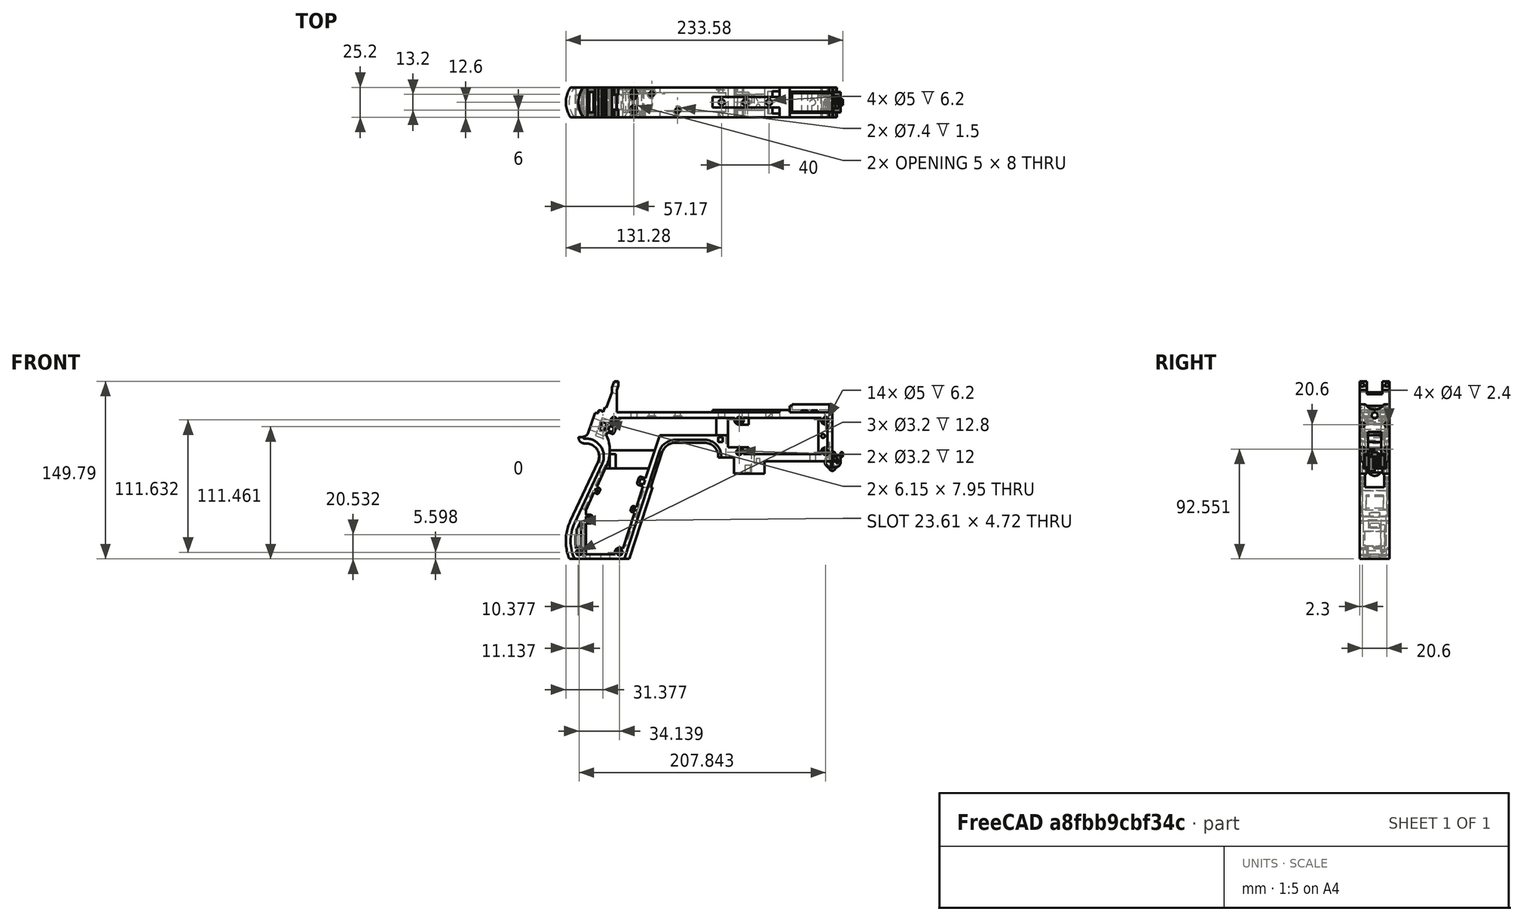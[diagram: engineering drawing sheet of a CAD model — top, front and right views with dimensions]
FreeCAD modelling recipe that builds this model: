
FCSTD DOCUMENT  (FreeCAD 1.0R39319 (Git))
Label: PICON-OF_ver_40
License: All rights reserved
LicenseURL: https://en.wikipedia.org/wiki/All_rights_reserved
objects: Sketcher::SketchObject×109, Part::Extrusion×52, Part::Cut×41, PartDesign::Pad×29, PartDesign::Pocket×18, PartDesign::Chamfer×15, PartDesign::Body×10, PartDesign::Fillet×6, PartDesign::SubtractivePipe×4, Part::Part2DObjectPython×4, PartDesign::SubtractiveLoft×4, PartDesign::Plane×2, PartDesign::SubShapeBinder×2, Part::Sweep×1, PartDesign::ShapeBinder×1, Part::MultiFuse×1, Mesh::Feature×1
note: 560 computed .brp shape members not serialized (recipe doc carries the construction recipe); baked Part::Feature solids carry a one-line shape summary decoded from their .brp

FEATURE [Sketcher::SketchObject] Sketch  label="corpo principale"
  ArcFitTolerance = 1e-06
  AttacherType = Attacher::AttachEngine3D
  AttachmentSupport = -> [XZ_Plane]
  FullyConstrained = true
  MakeInternals = false
  MapMode = 5
  Placement = pos=(0,0,0) rot=(1,0,0;1.5708rad)
  sketch-geometry (65):
    g0: LineSegment StartX=0 StartY=0 StartZ=0 EndX=-57.2 EndY=0 EndZ=0
    g1: LineSegment StartX=-57.2 StartY=0 StartZ=0 EndX=-57.2 EndY=-10.4 EndZ=0
    g2: LineSegment StartX=-57.2 StartY=-10.4 StartZ=0 EndX=-82.8 EndY=-10.4 EndZ=0
    g3: LineSegment StartX=-82.8 StartY=-10.4 StartZ=0 EndX=-82.8 EndY=3.2 EndZ=0
    g4: LineSegment StartX=-82.8 StartY=3.2 StartZ=0 EndX=-93.6 EndY=3.2 EndZ=0
    g5: LineSegment StartX=-93.6 StartY=3.2 StartZ=0 EndX=-93.6 EndY=4 EndZ=0
    g6: LineSegment StartX=-107.6 StartY=18 StartZ=0 EndX=-132.428 EndY=18 EndZ=0
    g7: LineSegment StartX=-145.743 StartY=8.32624 StartZ=0 EndX=-175.232 EndY=-82.4316 EndZ=0
    g8: LineSegment StartX=-175.232 StartY=-82.4316 StartZ=0 EndX=-217.232 EndY=-82.4316 EndZ=0
    g9: LineSegment StartX=-217.232 StartY=-52.1862 StartZ=0 EndX=-193.988 EndY=-2.33927 EndZ=0
    g10: LineSegment StartX=-206.196 StartY=23.0857 StartZ=0 EndX=-199.861 EndY=40.4914 EndZ=0
    g11: LineSegment StartX=-199.861 StartY=40.4914 StartZ=0 EndX=-197.061 EndY=40.4914 EndZ=0
    g12: LineSegment StartX=-197.061 StartY=40.4914 StartZ=0 EndX=-197.061 EndY=42.8914 EndZ=0
    g13: LineSegment StartX=-197.061 StartY=42.8914 StartZ=0 EndX=-194.261 EndY=42.8914 EndZ=0
    g14: LineSegment StartX=-194.261 StartY=42.8914 StartZ=0 EndX=-194.535 EndY=42.1397 EndZ=0
    g15: LineSegment StartX=-194.535 StartY=42.1397 StartZ=0 EndX=-193.031 EndY=41.5924 EndZ=0
    g16: LineSegment StartX=-193.031 StartY=41.5924 StartZ=0 EndX=-191.663 EndY=45.3512 EndZ=0
    g17: LineSegment StartX=-191.663 StartY=45.3512 StartZ=0 EndX=-190.536 EndY=44.9408 EndZ=0
    g18: LineSegment StartX=-190.536 StartY=44.9408 StartZ=0 EndX=-185.747 EndY=58.0965 EndZ=0
    g19: LineSegment StartX=-185.747 StartY=58.0965 StartZ=0 EndX=-185.747 EndY=62.0965 EndZ=0
    g20: LineSegment StartX=-185.747 StartY=62.0965 StartZ=0 EndX=-183.832 EndY=67.3588 EndZ=0
    g21: LineSegment StartX=-183.832 StartY=67.3588 StartZ=0 EndX=-180.232 EndY=67.3588 EndZ=0
    g22: LineSegment StartX=-180.232 StartY=67.3588 StartZ=0 EndX=-180.232 EndY=63.7588 EndZ=0
    g23: LineSegment StartX=-180.232 StartY=63.7588 StartZ=0 EndX=-181.6 EndY=60 EndZ=0
    g24: LineSegment StartX=-181.6 StartY=60 StartZ=0 EndX=-181.6 EndY=41.2 EndZ=0
    g25: LineSegment StartX=-181.6 StartY=41.2 StartZ=0 EndX=-100.8 EndY=41.2 EndZ=0
    g26: LineSegment StartX=-36 StartY=43.2 StartZ=0 EndX=-36 EndY=41.2 EndZ=0
    g27: LineSegment StartX=0 StartY=48 StartZ=0 EndX=0 EndY=0 EndZ=0
    g28: LineSegment StartX=-209.901 StartY=19.85 StartZ=0 EndX=-209.901 EndY=20.1 EndZ=0
    g29: LineSegment StartX=-208.001 StartY=22 StartZ=0 EndX=-207.747 EndY=22 EndZ=0
    g30: LineSegment StartX=-207.583 StartY=19 StartZ=0 EndX=-209.051 EndY=19 EndZ=0
    g31: ArcOfCircle CenterX=-208.001 CenterY=20.1 CenterZ=0 NormalX=0 NormalY=0 NormalZ=1 AngleXU=0 Radius=1.9 StartAngle=1.5708 EndAngle=3.14159
    g32: GeomPoint [constr] X=-209.901 Y=22 Z=0
    g33: ArcOfCircle CenterX=-209.051 CenterY=19.85 CenterZ=0 NormalX=0 NormalY=0 NormalZ=1 AngleXU=0 Radius=0.85 StartAngle=3.14159 EndAngle=4.71239
    g34: GeomPoint [constr] X=-209.901 Y=19 Z=0
    g35: ArcOfCircle CenterX=-207.747 CenterY=23.65 CenterZ=0 NormalX=0 NormalY=0 NormalZ=1 AngleXU=0 Radius=1.65 StartAngle=4.71239 EndAngle=5.93412
    g36: GeomPoint [constr] X=-206.591 Y=22 Z=0
    g37: LineSegment StartX=-4 StartY=6 StartZ=0 EndX=-4 EndY=36.4 EndZ=0
    g38: LineSegment StartX=-4 StartY=36.4 StartZ=0 EndX=-185.2 EndY=36.4 EndZ=0
    g39: LineSegment StartX=-185.2 StartY=36.4 StartZ=0 EndX=-190.441 EndY=22 EndZ=0
    g40: LineSegment StartX=-214.575 StartY=-78.4316 StartZ=0 EndX=-178.142 EndY=-78.4316 EndZ=0
    g41: LineSegment StartX=-178.142 StartY=-78.4316 StartZ=0 EndX=-145.51 EndY=22 EndZ=0
    g42: LineSegment StartX=-145.51 StartY=22 StartZ=0 EndX=-87.91 EndY=22 EndZ=0
    g43: LineSegment StartX=-87.91 StartY=22 StartZ=0 EndX=-87.91 EndY=11.6 EndZ=0
    g44: LineSegment StartX=-87.91 StartY=11.6 StartZ=0 EndX=-80.11 EndY=11.6 EndZ=0
    g45: LineSegment StartX=-80.11 StartY=11.6 StartZ=0 EndX=-80.11 EndY=6 EndZ=0
    g46: LineSegment StartX=-80.11 StartY=6 StartZ=0 EndX=-4 EndY=6 EndZ=0
    g47: LineSegment StartX=-190.363 StartY=-4.02975 StartZ=0 EndX=-213.607 EndY=-53.8767 EndZ=0
    g48: ArcOfCircle CenterX=-132.428 CenterY=4 CenterZ=0 NormalX=0 NormalY=0 NormalZ=1 AngleXU=0 Radius=14 StartAngle=1.5708 EndAngle=2.82743
    g49: GeomPoint [constr] X=-142.6 Y=18 Z=0
    g50: ArcOfCircle CenterX=-107.6 CenterY=4 CenterZ=0 NormalX=0 NormalY=0 NormalZ=1 AngleXU=0 Radius=14 StartAngle=0 EndAngle=1.5708
    g51: GeomPoint [constr] X=-93.6 Y=18 Z=0
    g52: ArcOfCircle CenterX=-184.801 CenterY=-67.3089 CenterZ=0 NormalX=0 NormalY=0 NormalZ=1 AngleXU=0 Radius=35.7833 StartAngle=2.70526 EndAngle=3.57792
    g53: ArcOfCircle CenterX=-207.583 CenterY=4 CenterZ=0 NormalX=0 NormalY=0 NormalZ=1 AngleXU=0 Radius=15 StartAngle=5.84685 EndAngle=7.85398
    g54: LineSegment [constr] StartX=-213.607 StartY=-53.8767 StartZ=0 EndX=-217.232 EndY=-52.1862 EndZ=0
    g55: ArcOfCircle CenterX=-184.801 CenterY=-67.3089 CenterZ=0 NormalX=0 NormalY=0 NormalZ=1 AngleXU=0 Radius=31.7833 StartAngle=2.70526 EndAngle=3.49911
    g56: ArcOfCircle CenterX=-218.095 CenterY=8.90192 CenterZ=0 NormalX=0 NormalY=0 NormalZ=1 AngleXU=0 Radius=30.5989 StartAngle=5.84685 EndAngle=6.72553
    g57: LineSegment StartX=-44.6 StartY=43.2 StartZ=0 EndX=-36 EndY=43.2 EndZ=0
    g58: LineSegment StartX=-100.8 StartY=41.2 StartZ=0 EndX=-44.6 EndY=41.2 EndZ=0
    g59: LineSegment StartX=-44.6 StartY=41.2 StartZ=0 EndX=-44.6 EndY=43.2 EndZ=0
    g60: LineSegment StartX=-2.4 StartY=48 StartZ=0 EndX=0 EndY=48 EndZ=0
    g61: LineSegment StartX=-36 StartY=41.2 StartZ=0 EndX=-2.4 EndY=41.2 EndZ=0
    g62: LineSegment StartX=-2.4 StartY=41.2 StartZ=0 EndX=-2.4 EndY=48 EndZ=0
    g63: LineSegment [constr] StartX=-181.6 StartY=36.4 StartZ=0 EndX=-152.209 EndY=36.4 EndZ=0
    g64: LineSegment [constr] StartX=-181.6 StartY=36.4 StartZ=0 EndX=-130.41 EndY=36.4 EndZ=0
  constraints (183):
    c: Coincident(g-1,g0)
    c: PointOnObject(g0,g-1)
    c: Coincident(g0,g1)
    c: Vertical(g1)
    c: Coincident(g1,g2)
    c: Horizontal(g2)
    c: Coincident(g2,g3)
    c: Vertical(g3)
    c: Coincident(g3,g4)
    c: Coincident(g4,g5)
    c: Vertical(g5)
    c: Horizontal(g6)
    c: Coincident(g7,g8)
    c: Horizontal(g8)
    c: Coincident(g10,g11)
    c: Horizontal(g11)
    c: Coincident(g11,g12)
    c: Vertical(g12)
    c: Coincident(g12,g13)
    c: Horizontal(g13)
    c: Coincident(g13,g14)
    c: Coincident(g14,g15)
    c: Coincident(g15,g16)
    c: Coincident(g16,g17)
    c: Coincident(g17,g18)
    c: Coincident(g18,g19)
    c: Vertical(g19)
    c: Coincident(g19,g20)
    c: Coincident(g20,g21)
    c: Horizontal(g21)
    c: Coincident(g21,g22)
    c: Vertical(g22)
    c: Coincident(g22,g23)
    c: Coincident(g23,g24)
    c: Vertical(g24)
    c: Coincident(g24,g25)
    c: Horizontal(g25)
    c: Coincident(g57,g26)
    c: Vertical(g26)
    c: Coincident(g26,g61)
    c: PointOnObject(g60,g-2)
    c: Coincident(g60,g27)
    c: Coincident(g27,g0)
    c: DistanceY(g27,g27) = 48
    c: DistanceY(g1,g1) = 10.4
    c: DistanceX(g0,g0) = 57.2
    c: DistanceX(g2,g2) = 25.6
    c: Horizontal(g4)
    c: DistanceY(g3,g3) = 13.6
    c: DistanceX(g4,g4) = 10.8
    c: DistanceY(g5,g51) = 14.8
    c: DistanceX(g49,g51) = 49
    c: Distance(g7,g49) = 105.6
    c: DistanceX(g61,g60) = 36
    c: DistanceX(g25,g25) = 80.8
    c: DistanceY(g24,g24) = 18.8
    c: DistanceY(g22,g22) = 3.6
    c: Distance(g23) = 4
    c: Angle(g-1,g23) = 1.22173
    c: DistanceX(g21,g21) = 3.6
    c: Distance(g20) = 5.6
    c: Angle(g-1,g20) = 1.22173
    c: DistanceY(g19,g19) = 4
    c: Distance(g18) = 14
    c: Angle(g-1,g18) = 1.22173
    c: Distance(g17) = 1.2
    c: Distance(g16) = 4
    c: Angle(g16) = 1.22173
    c: Perpendicular(g18,g17)
    c: Distance(g15) = 1.6
    c: Perpendicular(g16,g15)
    c: Distance(g14) = 0.8
    c: DistanceX(g13,g13) = 2.8
    c: Perpendicular(g15,g14)
    c: DistanceY(g12,g12) = 2.4
    c: DistanceX(g11,g11) = 2.8
    c: Distance(g9) = 55
    c: Angle(g9,g-1) = 2.00713
    c: Horizontal(g29)
    c: Vertical(g28)
    c: Horizontal(g30)
    c: PointOnObject(g32,g29)
    c: PointOnObject(g32,g28)
    c: Tangent(g29,g31) = 1.5708
    c: Tangent(g28,g31) = 1.5708
    c: PointOnObject(g34,g28)
    c: PointOnObject(g34,g30)
    c: Tangent(g28,g33) = 1.5708
    c: Tangent(g30,g33) = 1.5708
    c: PointOnObject(g36,g29)
    c: PointOnObject(g36,g10)
    c: Tangent(g29,g35) = -1.5708
    c: Tangent(g10,g35) = -1.5708
    c: Angle(g-1,g10) = 1.22173
    c: Radius(g35) = 1.65
    c: Vertical(g37)
    c: Coincident(g37,g38)
    c: Horizontal(g38)
    c: Coincident(g38,g39)
    c: Horizontal(g40)
    c: Coincident(g40,g41)
    c: Coincident(g41,g42)
    c: Horizontal(g42)
    c: Coincident(g42,g43)
    c: Vertical(g43)
    c: Coincident(g43,g44)
    c: Horizontal(g44)
    c: Coincident(g44,g45)
    c: Vertical(g45)
    c: Coincident(g45,g46)
    c: Coincident(g46,g37)
    c: Horizontal(g46)
    c: DistanceY(g0,g37) = 6
    c: DistanceX(g37,g0) = 4
    c: DistanceY(g37,g25) = 4.8
    c: DistanceX(g38,g38) = 181.2
    c: DistanceX(g42,g42) = 57.6
    c: DistanceY(g49,g41) = 4
    c: DistanceX(g41,g49) = 2.91
    c: DistanceY(g43,g43) = 10.4
    c: DistanceX(g44,g44) = 7.8
    c: DistanceY(g7,g40) = 4
    c: Distance(g47) = 55
    c: Angle(g-1,g39) = 1.22173
    c: PointOnObject(g49,g7)
    c: PointOnObject(g49,g6)
    c: Tangent(g7,g48) = -1.5708
    c: Tangent(g6,g48) = -1.5708
    c: PointOnObject(g51,g5)
    c: PointOnObject(g51,g6)
    c: Tangent(g5,g50) = -1.5708
    c: Tangent(g6,g50) = -1.5708
    c: Radius(g50) = 14
    c: Radius(g48) = 14
    c: DistanceX(g8,g8) = 42
    c: Angle(g7,g-1) = 1.88496
    c: Parallel(g41,g7)
    c: Parallel(g47,g9)
    c: Coincident(g52,g8)
    c: Tangent(g52,g9) = 1.5708
    c: DistanceX(g9,g8) = 0
    c: Tangent(g53,g9) = -1.5708
    c: Tangent(g53,g30) = -1.5708
    c: Diameter(g53) = 30
    c: DistanceY(g53,g0) = -4
    c: Coincident(g54,g47)
    c: Distance(g54) = 4
    c: Coincident(g54,g9)
    c: Coincident(g55,g40)
    c: Tangent(g55,g47) = -1.5708
    c: Coincident(g52,g55)
    c: Coincident(g56,g39)
    c: Tangent(g56,g47) = 1.5708
    c: Horizontal(g57)
    c: DistanceX(g57,g57) = 8.6
    c: Coincident(g58,g25)
    c: Horizontal(g58)
    c: Coincident(g59,g58)
    c: Vertical(g59)
    c: DistanceY(g58,g57) = 2
    c: DistanceX(g58,g58) = 56.2
    c: Coincident(g59,g57)
    c: DistanceY(g41,g36) = 0
    c: DistanceY(g36,g39) = 0
    c: DistanceY(g28,g28) = 0.25
    c: DistanceX(g30,g36) = 2.46
    c: DistanceX(g28,g29) = 1.9
    c: Coincident(g62,g60)
    c: Horizontal(g60)
    c: DistanceX(g62,g27) = 2.4
    c: Coincident(g61,g62)
    c: DistanceY(g26,g26) = 2
    c: Vertical(g62)
    c: DistanceY(g61,g60) = 6.8
    c: Horizontal(g61)
    c: Distance(g63) = 29.391
    c: PointOnObject(g63,g38)
    c: PointOnObject(g63,g38)
    c: Distance(g64) = 51.19
    c: PointOnObject(g64,g38)
    c: PointOnObject(g64,g38)
    c: DistanceX(g24,g63) = 0
    c: DistanceX(g24,g64) = 0
FEATURE [Part::Extrusion] Extrude  label="Extrude corpo principale"
  Base = -> Sketch
  Dir = (0,-1,2e-16)
  DirMode = 2
  FaceMakerClass = Part::FaceMakerBullseye
  FaceMakerMode = 3
  LengthFwd = 25.2
  LengthRev = 12.6
  Solid = true
  Symmetric = true
FEATURE [Sketcher::SketchObject] Sketch002  label="scavo grilletto"
  ArcFitTolerance = 1e-06
  AttachmentSupport = -> [XZ_Plane]
  ExternalGeometry = -> [Sketch]
  FullyConstrained = true
  MakeInternals = false
  MapMode = 5
  Placement = pos=(0,0,0) rot=(1,0,0;1.5708rad)
  sketch-geometry (4):
    g0: LineSegment StartX=-89.51 StartY=22 StartZ=0 EndX=-152.71 EndY=22 EndZ=0
    g1: LineSegment StartX=-152.71 StartY=22 StartZ=0 EndX=-167.006 EndY=-22 EndZ=0
    g2: LineSegment StartX=-167.006 StartY=-22 StartZ=0 EndX=-89.51 EndY=-22 EndZ=0
    g3: LineSegment StartX=-89.51 StartY=-22 StartZ=0 EndX=-89.51 EndY=22 EndZ=0
  constraints (12):
    c: Horizontal(g0)
    c: Coincident(g0,g1)
    c: Coincident(g1,g2)
    c: Horizontal(g2)
    c: Coincident(g2,g3)
    c: Coincident(g3,g0)
    c: Vertical(g3)
    c: Angle(g1,g0) = 1.88496
    c: DistanceY(g3,g3) = 44
    c: DistanceX(g0,g0) = 63.2
    c: DistanceX(g0,g-3) = 1.6
    c: DistanceY(g-3,g0) = 0
FEATURE [Sketcher::SketchObject] Sketch004  label="traiettoria arrotondamento impugnatura anteriore"
  ArcFitTolerance = 1e-06
  AttachmentSupport = -> [XZ_Plane]
  ExternalGeometry = -> [Sketch]
  FullyConstrained = true
  MakeInternals = false
  MapMode = 5
  Placement = pos=(0,0,0) rot=(1,0,0;1.5708rad)
  sketch-geometry (13):
    g0: LineSegment StartX=-175.232 StartY=-82.4316 StartZ=0 EndX=-145.743 EndY=8.32624 EndZ=0
    g1: LineSegment StartX=-93.6 StartY=3.2 StartZ=0 EndX=-93.6 EndY=4 EndZ=0
    g2: LineSegment StartX=-132.428 StartY=18 StartZ=0 EndX=-107.6 EndY=18 EndZ=0
    g3: ArcOfCircle CenterX=-132.428 CenterY=4 CenterZ=0 NormalX=0 NormalY=0 NormalZ=1 AngleXU=0 Radius=14 StartAngle=1.5708 EndAngle=2.82743
    g4: ArcOfCircle CenterX=-107.6 CenterY=4 CenterZ=0 NormalX=0 NormalY=0 NormalZ=1 AngleXU=0 Radius=14 StartAngle=0 EndAngle=1.5708
    g5: LineSegment StartX=-175.232 StartY=-82.4316 StartZ=0 EndX=-217.232 EndY=-82.4316 EndZ=0
    g6: LineSegment StartX=-217.232 StartY=-52.1862 StartZ=0 EndX=-193.988 EndY=-2.33927 EndZ=0
    g7: LineSegment StartX=-209.051 StartY=19 StartZ=0 EndX=-207.583 EndY=19 EndZ=0
    g8: LineSegment StartX=-209.901 StartY=20.1 StartZ=0 EndX=-209.901 EndY=19.85 EndZ=0
    g9: ArcOfCircle CenterX=-184.801 CenterY=-67.3089 CenterZ=0 NormalX=0 NormalY=0 NormalZ=1 AngleXU=0 Radius=35.7833 StartAngle=2.70526 EndAngle=3.57792
    g10: ArcOfCircle CenterX=-207.583 CenterY=4 CenterZ=0 NormalX=0 NormalY=0 NormalZ=1 AngleXU=0 Radius=15 StartAngle=5.84685 EndAngle=7.85398
    g11: ArcOfCircle CenterX=-209.051 CenterY=19.85 CenterZ=0 NormalX=0 NormalY=0 NormalZ=1 AngleXU=0 Radius=0.85 StartAngle=3.14159 EndAngle=4.71239
    g12: ArcOfCircle CenterX=-208.001 CenterY=20.1 CenterZ=0 NormalX=0 NormalY=0 NormalZ=1 AngleXU=0 Radius=1.9 StartAngle=1.5708 EndAngle=3.14159
  constraints (26):
    c: Coincident(g0,g-3)
    c: Coincident(g0,g-6)
    c: Coincident(g1,g-8)
    c: Coincident(g1,g-7)
    c: Coincident(g2,g-5)
    c: Coincident(g2,g-4)
    c: Coincident(g3,g2)
    c: Tangent(g3,g0) = 1.5708
    c: Coincident(g4,g1)
    c: Tangent(g4,g2) = 1.5708
    c: Coincident(g5,g0)
    c: Coincident(g5,g-9)
    c: Coincident(g6,g-12)
    c: Coincident(g6,g-11)
    c: Coincident(g7,g-15)
    c: Coincident(g7,g-14)
    c: Coincident(g8,g-16)
    c: Coincident(g8,g-17)
    c: Tangent(g9,g6) = 1.5708
    c: Coincident(g9,g5)
    c: Coincident(g10,g7)
    c: Tangent(g10,g6) = -1.5708
    c: Tangent(g11,g7) = -1.5708
    c: Coincident(g11,g8)
    c: Tangent(g12,g8) = -1.5708
    c: Coincident(g12,g-17)
FEATURE [PartDesign::Plane] DatumPlane  label="Piano per disegno arrotondamento impugnatura"
  AttachmentSupport = -> [Sketch]
  Length = 73.6581
  MapMode = 7
  Placement = pos=(-145.743,1.8e-15,8.32624) rot=(0.154555,0.154555,0.97582;1.59527rad)
  ResizeMode = 0
  Width = 303.511
FEATURE [Sketcher::SketchObject] Sketch005  label="forma arrotondamento impugnatura anteriore"
  ArcFitTolerance = 1e-06
  AttachmentSupport = -> [DatumPlane]
  FullyConstrained = true
  MakeInternals = false
  MapMode = 5
  Placement = pos=(-145.743,1.8e-15,8.32624) rot=(0.154555,0.154555,0.97582;1.59527rad)
  sketch-geometry (5):
    g0: GeomPoint [constr] X=0 Y=-4 Z=0
    g1: GeomPoint [constr] X=-12.6 Y=7.1e-15 Z=0
    g2: GeomPoint [constr] X=12.6 Y=4.97e-14 Z=0
    g3: LineSegment StartX=-12.6 StartY=7.1e-15 StartZ=0 EndX=12.6 EndY=4.97e-14 EndZ=0
    g4: ArcOfCircle CenterX=-3.88e-14 CenterY=17.845 CenterZ=0 NormalX=0 NormalY=0 NormalZ=1 AngleXU=0 Radius=21.845 StartAngle=4.09759 EndAngle=5.32718
  constraints (11):
    c: DistanceY(g0,g-1) = 4
    c: DistanceX(g-1,g0) = 0
    c: DistanceX(g1,g-1) = 12.6
    c: DistanceX(g-1,g2) = 12.6
    c: DistanceY(g-1,g2) = 0
    c: DistanceY(g-1,g1) = 0
    c: Coincident(g3,g1)
    c: Coincident(g3,g2)
    c: Coincident(g4,g1)
    c: Coincident(g4,g2)
    c: PointOnObject(g0,g4)
FEATURE [Part::Sweep] Sweep  label="Sweep impugnatura"
  Frenet = true
  Sections = -> [Sketch005]
  Solid = true
  Spine = -> Sketch [Edge32,Edge33,Edge34,Edge35,Edge36,Edge37,Edge38,Edge39,Edge40,Edge41,Edge42,Edge43,Edge44]
  Transition = 1
FEATURE [Sketcher::SketchObject] Sketch008  label="buchi e pulizie varie"
  ArcFitTolerance = 1e-06
  AttachmentSupport = -> [XZ_Plane]
  ExternalGeometry = -> [Sketch]
  FullyConstrained = true
  MakeInternals = false
  MapMode = 5
  Placement = pos=(0,0,0) rot=(1,0,0;1.5708rad)
  sketch-geometry (26):
    g0: LineSegment StartX=-96.278 StartY=20.155 StartZ=0 EndX=-92.278 EndY=20.155 EndZ=0
    g1: LineSegment StartX=-92.278 StartY=20.155 StartZ=0 EndX=-92.278 EndY=16.155 EndZ=0
    g2: LineSegment StartX=-92.278 StartY=16.155 StartZ=0 EndX=-96.278 EndY=16.155 EndZ=0
    g3: LineSegment StartX=-96.278 StartY=16.155 StartZ=0 EndX=-96.278 EndY=20.155 EndZ=0
    g4: LineSegment StartX=-222.232 StartY=-82.4316 StartZ=0 EndX=-170.232 EndY=-82.4316 EndZ=0
    g5: LineSegment StartX=-170.232 StartY=-82.4316 StartZ=0 EndX=-170.232 EndY=-86.4316 EndZ=0
    g6: LineSegment StartX=-170.232 StartY=-86.4316 StartZ=0 EndX=-222.232 EndY=-86.4316 EndZ=0
    g7: LineSegment StartX=-222.232 StartY=-86.4316 StartZ=0 EndX=-222.232 EndY=-82.4316 EndZ=0
    g8: LineSegment StartX=-213.901 StartY=20.1 StartZ=0 EndX=-213.901 EndY=26 EndZ=0
    g9: LineSegment StartX=-213.901 StartY=26 StartZ=0 EndX=-206.196 EndY=26 EndZ=0
    g10: LineSegment StartX=-17.4 StartY=42.8 StartZ=0 EndX=-12.4 EndY=42.8 EndZ=0
    g11: LineSegment StartX=-12.4 StartY=42.8 StartZ=0 EndX=-12.4 EndY=41.2 EndZ=0
    g12: LineSegment StartX=-12.4 StartY=41.2 StartZ=0 EndX=-17.4 EndY=41.2 EndZ=0
    g13: LineSegment StartX=-17.4 StartY=41.2 StartZ=0 EndX=-17.4 EndY=42.8 EndZ=0
    g14: LineSegment StartX=-25.9 StartY=42.8 StartZ=0 EndX=-20.9 EndY=42.8 EndZ=0
    g15: LineSegment StartX=-20.9 StartY=42.8 StartZ=0 EndX=-20.9 EndY=41.2 EndZ=0
    g16: LineSegment StartX=-20.9 StartY=41.2 StartZ=0 EndX=-25.9 EndY=41.2 EndZ=0
    g17: LineSegment StartX=-25.9 StartY=41.2 StartZ=0 EndX=-25.9 EndY=42.8 EndZ=0
    g18: GeomPoint [constr] X=-206.196 Y=23.0857 Z=0
    g19: GeomPoint [constr] X=-213.901 Y=20.1 Z=0
    g20: BSplineCurve PolesCount=4 KnotsCount=2 Degree=3 IsPeriodic=0
    g21-g24: Circle [constr] x4 (B-spline internal-alignment scaffolding for g20; pole/knot coordinates omitted)
    g25: LineSegment StartX=-206.196 StartY=26 StartZ=0 EndX=-206.196 EndY=23.0857 EndZ=0
  constraints (73):
    c: Horizontal(g0)
    c: Coincident(g1,g0)
    c: Vertical(g1)
    c: Coincident(g2,g1)
    c: Horizontal(g2)
    c: Coincident(g3,g2)
    c: Coincident(g3,g0)
    c: Vertical(g3)
    c: DistanceX(g0,g-4) = 4.368
    c: DistanceY(g0,g-4) = 1.845
    c: DistanceY(g1,g1) = 4
    c: DistanceX(g2,g2) = 4
    c: Horizontal(g4)
    c: Coincident(g5,g4)
    c: Vertical(g5)
    c: Coincident(g6,g5)
    c: Horizontal(g6)
    c: Coincident(g7,g6)
    c: Coincident(g7,g4)
    c: Vertical(g7)
    c: DistanceY(g7,g7) = 4
    c: DistanceX(g4,g-5) = 5
    c: DistanceX(g-5,g4) = 5
    c: DistanceY(g4,g-5) = 0
    c: Coincident(g9,g8)
    c: Parallel(g9,g-6)
    c: DistanceX(g8,g-8) = 4
    c: Horizontal(g10)
    c: Coincident(g11,g10)
    c: Vertical(g11)
    c: Coincident(g12,g11)
    c: Horizontal(g12)
    c: Coincident(g13,g12)
    c: Coincident(g13,g10)
    c: Vertical(g13)
    c: Horizontal(g14)
    c: Coincident(g15,g14)
    c: Vertical(g15)
    c: Coincident(g16,g15)
    c: Horizontal(g16)
    c: Coincident(g17,g16)
    c: Coincident(g17,g14)
    c: Vertical(g17)
    c: DistanceY(g11,g10) = 1.6
    c: DistanceX(g10,g10) = 5
    c: DistanceY(g15,g14) = 1.6
    c: DistanceX(g14,g14) = 5
    c: DistanceX(g15,g12) = 3.5
    c: DistanceX(g11,g-9) = 10
    c: DistanceY(g-9,g11) = 0
    c: DistanceY(g-9,g15) = 0
    c: Perpendicular(g8,g9)
    c: DistanceY(g-7,g9) = 4
    c: DistanceY(g8,g-8) = 0
    c: InternalAlignment(g18,g20)
    c: InternalAlignment(g19,g20)
    c: InternalAlignment(g21,g20)
    c: Weight(g21) = 1
    c: InternalAlignment(g22,g20)
    c: Equal(g22,g21)
    c: InternalAlignment(g23,g20)
    c: Equal(g23,g21)
    c: InternalAlignment(g24,g20)
    c: Equal(g24,g21)
    c: Coincident(g18,g-12)
    c: Coincident(g19,g8)
    c: Coincident(g25,g9)
    c: Coincident(g25,g20)
    c: Vertical(g25)
    c: DistanceY(g20,g23) = 0
    c: DistanceY(g22,g18) = 2.26
    c: DistanceX(g22,g18) = 0.93
    c: DistanceX(g20,g23) = 2.9
FEATURE [Part::Extrusion] Extrude004  label="Extrude Buchi e pulizie varie"
  Base = -> Sketch008
  Dir = (0,-1,2e-16)
  DirMode = 2
  FaceMakerClass = Part::FaceMakerBullseye
  FaceMakerMode = 3
  LengthFwd = 25.2
  LengthRev = 0
  Solid = true
  Symmetric = true
FEATURE [Sketcher::SketchObject] Sketch009  label="rinforzi"
  ArcFitTolerance = 1e-06
  AttachmentSupport = -> [XZ_Plane]
  ExternalGeometry = -> [Sketch]
  FullyConstrained = true
  MakeInternals = false
  MapMode = 5
  Placement = pos=(0,0,0) rot=(1,0,0;1.5708rad)
  sketch-geometry (9):
    g0: LineSegment StartX=-87.91 StartY=22 StartZ=0 EndX=-87.91 EndY=36.4 EndZ=0
    g1: LineSegment StartX=-87.91 StartY=36.4 StartZ=0 EndX=-97.91 EndY=36.4 EndZ=0
    g2: LineSegment StartX=-97.91 StartY=36.4 StartZ=0 EndX=-97.91 EndY=22 EndZ=0
    g3: LineSegment StartX=-97.91 StartY=22 StartZ=0 EndX=-87.91 EndY=22 EndZ=0
    g4: LineSegment StartX=-149.713 StartY=9.06563 StartZ=0 EndX=-154.586 EndY=-5.93437 EndZ=0
    g5: LineSegment StartX=-154.586 StartY=-5.93437 StartZ=0 EndX=-191.863 EndY=-5.93437 EndZ=0
    g6: LineSegment StartX=-191.863 StartY=-5.93437 StartZ=0 EndX=-191.863 EndY=9.06563 EndZ=0
    g7: LineSegment StartX=-191.863 StartY=9.06563 StartZ=0 EndX=-149.713 EndY=9.06563 EndZ=0
    g8: LineSegment [constr] StartX=-145.51 StartY=22 StartZ=0 EndX=-149.713 EndY=9.06563 EndZ=0
  constraints (25):
    c: Vertical(g0)
    c: Coincident(g1,g0)
    c: Horizontal(g1)
    c: Coincident(g2,g1)
    c: Vertical(g2)
    c: Coincident(g3,g2)
    c: Coincident(g3,g0)
    c: Horizontal(g3)
    c: Coincident(g0,g-4)
    c: DistanceX(g3,g3) = 10
    c: DistanceY(g0,g-3) = 0
    c: Coincident(g5,g4)
    c: Horizontal(g5)
    c: Coincident(g6,g5)
    c: Vertical(g6)
    c: Coincident(g7,g6)
    c: Coincident(g7,g4)
    c: Horizontal(g7)
    c: Distance(g8) = 13.6
    c: Parallel(g-6,g8)
    c: Coincident(g-6,g8)
    c: Parallel(g4,g-6)
    c: DistanceY(g4,g4) = 15
    c: Coincident(g4,g8)
    c: DistanceX(g-5,g5) = -1.5
FEATURE [Part::Extrusion] Extrude001  label="Extrude scavo grilletto"
  Base = -> Sketch002
  Dir = (0,-1,2e-16)
  DirMode = 2
  FaceMakerClass = Part::FaceMakerBullseye
  FaceMakerMode = 3
  LengthFwd = 16
  LengthRev = 0
  Solid = true
  Symmetric = true
FEATURE [Part::Extrusion] Extrude005  label="Extrude Rinforzi"
  Base = -> Sketch009
  Dir = (0,-1,2e-16)
  DirMode = 2
  FaceMakerClass = Part::FaceMakerBullseye
  FaceMakerMode = 3
  LengthFwd = 2
  LengthRev = 0
  Placement = pos=(0,12.6,0) rot=(0,0,1;0rad)
  Solid = true
  Symmetric = false
FEATURE [PartDesign::ShapeBinder] CopyCut
  TraceSupport = false
FEATURE [PartDesign::Plane] DatumPlane001
  AttachmentSupport = -> [CopyCut]
  Length = 283.944
  MapMode = 5
  Placement = pos=(0,12.6,0) rot=(0,0.707107,0.707107;3.14159rad)
  ResizeMode = 0
  Width = 188.15
FEATURE [Sketcher::SketchObject] Sketch010  label="buco neopixel"
  ArcFitTolerance = 1e-06
  AttachmentSupport = -> [XZ_Plane]
  ExternalGeometry = -> [Sketch]
  FullyConstrained = true
  MakeInternals = false
  MapMode = 5
  Placement = pos=(0,0,0) rot=(1,0,0;1.5708rad)
  sketch-geometry (5):
    g0: LineSegment [constr] StartX=-199.861 StartY=40.4914 StartZ=0 EndX=-201.368 EndY=36.3521 EndZ=0
    g1: LineSegment StartX=-201.368 StartY=36.3521 StartZ=0 EndX=-204.932 EndY=26.5605 EndZ=0
    g2: LineSegment StartX=-201.368 StartY=36.3521 StartZ=0 EndX=-180.2 EndY=28.6477 EndZ=0
    g3: LineSegment StartX=-180.2 StartY=28.6477 StartZ=0 EndX=-183.764 EndY=18.8561 EndZ=0
    g4: LineSegment StartX=-183.764 StartY=18.8561 StartZ=0 EndX=-204.932 EndY=26.5605 EndZ=0
  constraints (14):
    c: Parallel(g0,g-3)
    c: Distance(g0) = 4.405
    c: Coincident(g0,g-3)
    c: Coincident(g2,g1)
    c: Coincident(g3,g2)
    c: Coincident(g4,g3)
    c: Coincident(g4,g1)
    c: Parallel(g1,g-3)
    c: Distance(g1) = 10.42
    c: Coincident(g1,g0)
    c: Parallel(g2,g4)
    c: Perpendicular(g1,g2)
    c: DistanceX(g-4,g2) = 5
    c: Parallel(g3,g1)
FEATURE [Part::Extrusion] Extrude006  label="Extrude buco neopixel"
  Base = -> Sketch010
  Dir = (0,-1,2e-16)
  DirMode = 2
  FaceMakerClass = Part::FaceMakerBullseye
  FaceMakerMode = 3
  LengthFwd = 17.2
  LengthRev = 0
  Solid = true
  Symmetric = true
FEATURE [Sketcher::SketchObject] Sketch011  label="fermo grilletto"
  ArcFitTolerance = 1e-06
  AttachmentSupport = -> [XZ_Plane]
  ExternalGeometry = -> [Sketch]
  FullyConstrained = true
  MakeInternals = false
  MapMode = 5
  Placement = pos=(0,0,0) rot=(1,0,0;1.5708rad)
  sketch-geometry (18):
    g0: LineSegment [constr] StartX=-145.51 StartY=22 StartZ=0 EndX=-157.347 EndY=-14.4293 EndZ=0
    g1: LineSegment [constr] StartX=-157.347 StartY=-14.4293 StartZ=0 EndX=-157.841 EndY=-15.951 EndZ=0
    g2: LineSegment StartX=-161.151 StartY=-13.1932 StartZ=0 EndX=-155.825 EndY=-14.9237 EndZ=0
    g3: LineSegment StartX=-163.167 StartY=-14.2205 StartZ=0 EndX=-164.403 EndY=-18.0247 EndZ=0
    g4: LineSegment StartX=-163.376 StartY=-20.0408 StartZ=0 EndX=-158.05 EndY=-21.7713 EndZ=0
    g5: LineSegment StartX=-158.05 StartY=-21.7713 StartZ=0 EndX=-155.825 EndY=-14.9237 EndZ=0
    g6: LineSegment StartX=-161.645 StartY=-14.7149 StartZ=0 EndX=-157.841 EndY=-15.951 EndZ=0
    g7: LineSegment StartX=-157.841 StartY=-15.951 StartZ=0 EndX=-159.077 EndY=-19.7552 EndZ=0
    g8: LineSegment StartX=-159.077 StartY=-19.7552 StartZ=0 EndX=-162.881 EndY=-18.5191 EndZ=0
    g9: LineSegment StartX=-162.881 StartY=-18.5191 StartZ=0 EndX=-161.645 EndY=-14.7149 EndZ=0
    g10: LineSegment [constr] StartX=-161.645 StartY=-14.7149 StartZ=0 EndX=-161.151 EndY=-13.1932 EndZ=0
    g11: LineSegment [constr] StartX=-159.077 StartY=-19.7552 StartZ=0 EndX=-157.555 EndY=-20.2496 EndZ=0
    g12: LineSegment [constr] StartX=-159.077 StartY=-19.7552 StartZ=0 EndX=-159.572 EndY=-21.2769 EndZ=0
    g13: LineSegment [constr] StartX=-161.645 StartY=-14.7149 StartZ=0 EndX=-163.167 EndY=-14.2205 EndZ=0
    g14: ArcOfCircle CenterX=-161.645 CenterY=-14.7149 CenterZ=0 NormalX=0 NormalY=0 NormalZ=1 AngleXU=0 Radius=1.6 StartAngle=1.25664 EndAngle=2.82743
    g15: GeomPoint [constr] X=-162.673 Y=-12.6988 Z=0
    g16: ArcOfCircle CenterX=-162.881 CenterY=-18.5191 CenterZ=0 NormalX=0 NormalY=0 NormalZ=1 AngleXU=0 Radius=1.6 StartAngle=2.82743 EndAngle=4.39823
    g17: GeomPoint [constr] X=-164.897 Y=-19.5464 Z=0
  constraints (48):
    c: Parallel(g0,g-3)
    c: Distance(g0) = 38.304
    c: Coincident(g0,g-3)
    c: Parallel(g1,g-3)
    c: Distance(g1) = 1.6
    c: Coincident(g1,g0)
    c: Coincident(g5,g4)
    c: Coincident(g5,g2)
    c: Coincident(g7,g6)
    c: Coincident(g8,g7)
    c: Coincident(g9,g8)
    c: Coincident(g9,g6)
    c: Parallel(g7,g-3)
    c: Parallel(g9,g7)
    c: Perpendicular(g6,g7)
    c: Parallel(g6,g8)
    c: Distance(g6) = 4
    c: Distance(g9) = 4
    c: Parallel(g5,g7)
    c: Parallel(g9,g3)
    c: Parallel(g2,g6)
    c: Parallel(g4,g8)
    c: Parallel(g13,g6)
    c: Parallel(g10,g9)
    c: Parallel(g11,g8)
    c: Parallel(g12,g7)
    c: Distance(g10) = 1.6
    c: Distance(g13) = 1.6
    c: Distance(g12) = 1.6
    c: Distance(g11) = 1.6
    c: Coincident(g10,g6)
    c: Coincident(g13,g6)
    c: Coincident(g12,g7)
    c: Coincident(g11,g7)
    c: Distance(g10,g15) = 1.6
    c: Distance(g15,g13) = 1.6
    c: Distance(g4,g12) = 1.6
    c: Distance(g4,g11) = 1.6
    c: PointOnObject(g15,g2)
    c: Tangent(g3,g14) = -1.5708
    c: Tangent(g2,g14) = 1.5708
    c: PointOnObject(g17,g4)
    c: PointOnObject(g17,g3)
    c: Tangent(g4,g16) = -1.5708
    c: Tangent(g3,g16) = -1.5708
    c: Equal(g16,g14)
    c: Coincident(g16,g8)
    c: Coincident(g6,g1)
FEATURE [Part::Extrusion] Extrude007  label="Extrude fermo grilletto"
  Base = -> Sketch011
  Dir = (0,-1,2e-16)
  DirMode = 2
  FaceMakerClass = Part::FaceMakerBullseye
  FaceMakerMode = 3
  LengthFwd = 25.2
  LengthRev = 0
  Solid = true
  Symmetric = true
FEATURE [Sketcher::SketchObject] Sketch012  label="buco oled"
  ArcFitTolerance = 1e-06
  AttachmentSupport = -> [XZ_Plane]
  ExternalGeometry = -> [Sketch]
  FullyConstrained = true
  MakeInternals = false
  MapMode = 5
  Placement = pos=(0,0,0) rot=(1,0,0;1.5708rad)
  sketch-geometry (4):
    g0: LineSegment StartX=-185.747 StartY=58.0965 StartZ=0 EndX=-180.232 EndY=56.0891 EndZ=0
    g1: LineSegment StartX=-185.747 StartY=58.0965 StartZ=0 EndX=-185.747 EndY=67.3588 EndZ=0
    g2: LineSegment StartX=-185.747 StartY=67.3588 StartZ=0 EndX=-180.232 EndY=67.3588 EndZ=0
    g3: LineSegment StartX=-180.232 StartY=67.3588 StartZ=0 EndX=-180.232 EndY=56.0891 EndZ=0
  constraints (10):
    c: Coincident(g1,g0)
    c: Coincident(g2,g1)
    c: Coincident(g3,g2)
    c: Coincident(g3,g0)
    c: Parallel(g1,g-5)
    c: Perpendicular(g-3,g0)
    c: Parallel(g2,g-6)
    c: Parallel(g3,g-4)
    c: Coincident(g0,g-5)
    c: Coincident(g2,g-6)
FEATURE [Part::Extrusion] Extrude008  label="Extrude buco oled"
  Base = -> Sketch012
  Dir = (0,-1,2e-16)
  DirMode = 2
  FaceMakerClass = Part::FaceMakerBullseye
  FaceMakerMode = 3
  LengthFwd = 12.8
  LengthRev = 0
  Solid = true
  Symmetric = true
FEATURE [Sketcher::SketchObject] Sketch013  label="buco pompa"
  ArcFitTolerance = 1e-06
  AttachmentSupport = -> [XZ_Plane]
  ExternalGeometry = -> [Sketch]
  FullyConstrained = true
  MakeInternals = false
  MapMode = 5
  Placement = pos=(0,0,0) rot=(1,0,0;1.5708rad)
  sketch-geometry (8):
    g0: LineSegment StartX=-82.8 StartY=-10.4 StartZ=0 EndX=-82.8 EndY=-9.6 EndZ=0
    g1: LineSegment StartX=-82.8 StartY=-9.6 StartZ=0 EndX=-67.9 EndY=-9.6 EndZ=0
    g2: LineSegment StartX=-67.9 StartY=-9.6 StartZ=0 EndX=-67.9 EndY=6 EndZ=0
    g3: LineSegment StartX=-67.9 StartY=6 StartZ=0 EndX=-65.9 EndY=6 EndZ=0
    g4: LineSegment StartX=-65.9 StartY=6 StartZ=0 EndX=-65.9 EndY=-1.7 EndZ=0
    g5: LineSegment StartX=-65.9 StartY=-1.7 StartZ=0 EndX=-57.2 EndY=-1.7 EndZ=0
    g6: LineSegment StartX=-57.2 StartY=-1.7 StartZ=0 EndX=-57.2 EndY=-10.4 EndZ=0
    g7: LineSegment StartX=-57.2 StartY=-10.4 StartZ=0 EndX=-82.8 EndY=-10.4 EndZ=0
  constraints (22):
    c: Vertical(g0)
    c: Coincident(g1,g0)
    c: Horizontal(g1)
    c: Coincident(g2,g1)
    c: Vertical(g2)
    c: Coincident(g3,g2)
    c: Horizontal(g3)
    c: Coincident(g4,g3)
    c: Vertical(g4)
    c: Coincident(g5,g4)
    c: Horizontal(g5)
    c: Coincident(g6,g5)
    c: Vertical(g6)
    c: Coincident(g7,g6)
    c: Coincident(g7,g0)
    c: DistanceY(g0,g0) = 0.8
    c: DistanceY(g6,g6) = 8.7
    c: DistanceX(g1,g1) = 14.9
    c: DistanceX(g3,g3) = 2
    c: Coincident(g0,g-4)
    c: DistanceY(g2,g-6) = 0
    c: Coincident(g6,g-5)
FEATURE [Part::Extrusion] Extrude009  label="Extrude buco pompa"
  Base = -> Sketch013
  Dir = (0,-1,2e-16)
  DirMode = 2
  FaceMakerClass = Part::FaceMakerBullseye
  FaceMakerMode = 3
  LengthFwd = 13.2
  LengthRev = 0
  Solid = true
  Symmetric = true
FEATURE [Sketcher::SketchObject] Sketch014  label="buco frontale"
  ArcFitTolerance = 1e-06
  AttachmentSupport = -> [XZ_Plane]
  ExternalGeometry = -> [Sketch]
  FullyConstrained = true
  MakeInternals = false
  MapMode = 5
  Placement = pos=(0,0,0) rot=(1,0,0;1.5708rad)
  sketch-geometry (10):
    g0: LineSegment StartX=0 StartY=0 StartZ=0 EndX=0 EndY=24.671 EndZ=0
    g1: LineSegment StartX=0 StartY=24.671 StartZ=0 EndX=-4 EndY=24.671 EndZ=0
    g2: LineSegment StartX=-4 StartY=24.671 StartZ=0 EndX=-4 EndY=16 EndZ=0
    g3: LineSegment StartX=-4 StartY=16 StartZ=0 EndX=-2.4 EndY=16 EndZ=0
    g4: LineSegment StartX=-2.4 StartY=16 StartZ=0 EndX=-2.4 EndY=10 EndZ=0
    g5: LineSegment StartX=-2.4 StartY=10 StartZ=0 EndX=-12 EndY=10 EndZ=0
    g6: LineSegment StartX=-12 StartY=10 StartZ=0 EndX=-12 EndY=6 EndZ=0
    g7: LineSegment StartX=-12 StartY=6 StartZ=0 EndX=-2.4 EndY=6 EndZ=0
    g8: LineSegment StartX=-2.4 StartY=6 StartZ=0 EndX=-2.4 EndY=0 EndZ=0
    g9: LineSegment StartX=-2.4 StartY=0 StartZ=0 EndX=0 EndY=0 EndZ=0
  constraints (29):
    c: Vertical(g0)
    c: Coincident(g1,g0)
    c: Horizontal(g1)
    c: Coincident(g2,g1)
    c: Vertical(g2)
    c: Coincident(g3,g2)
    c: Horizontal(g3)
    c: Coincident(g4,g3)
    c: Vertical(g4)
    c: Coincident(g5,g4)
    c: Horizontal(g5)
    c: Coincident(g6,g5)
    c: Vertical(g6)
    c: Coincident(g7,g6)
    c: Coincident(g8,g7)
    c: Vertical(g8)
    c: Coincident(g9,g8)
    c: Coincident(g9,g0)
    c: Horizontal(g9)
    c: DistanceY(g0,g0) = 24.671
    c: Horizontal(g7)
    c: DistanceY(g6,g6) = 4
    c: DistanceY(g4,g4) = 6
    c: DistanceX(g9,g9) = 2.4
    c: Coincident(g0,g-1)
    c: DistanceY(g-3,g7) = 0
    c: DistanceX(g8,g4) = 0
    c: DistanceX(g-3,g1) = 0
    c: DistanceX(g6,g-3) = 8
FEATURE [Part::Extrusion] Extrude010  label="Extrude buco frontale"
  Base = -> Sketch014
  Dir = (0,-1,2e-16)
  DirMode = 2
  FaceMakerClass = Part::FaceMakerBullseye
  FaceMakerMode = 3
  LengthFwd = 11.2
  LengthRev = 0
  Solid = true
  Symmetric = true
FEATURE [Sketcher::SketchObject] Sketch015  label="guida rail"
  ArcFitTolerance = 1e-06
  AttachmentSupport = -> [XZ_Plane]
  ExternalGeometry = -> [Sketch]
  FullyConstrained = true
  MakeInternals = false
  MapMode = 5
  Placement = pos=(0,0,0) rot=(1,0,0;1.5708rad)
  sketch-geometry (4):
    g0: LineSegment StartX=-100.8 StartY=43.2 StartZ=0 EndX=-44.6 EndY=43.2 EndZ=0
    g1: LineSegment StartX=-44.6 StartY=43.2 StartZ=0 EndX=-44.6 EndY=41.2 EndZ=0
    g2: LineSegment StartX=-44.6 StartY=41.2 StartZ=0 EndX=-100.8 EndY=41.2 EndZ=0
    g3: LineSegment StartX=-100.8 StartY=41.2 StartZ=0 EndX=-100.8 EndY=43.2 EndZ=0
  constraints (9):
    c: Horizontal(g0)
    c: Coincident(g1,g0)
    c: Coincident(g2,g1)
    c: Coincident(g3,g2)
    c: Coincident(g3,g0)
    c: Vertical(g3)
    c: Coincident(g2,g-3)
    c: Coincident(g1,g-3)
    c: Coincident(g0,g-4)
FEATURE [Part::Extrusion] Extrude011  label="Extrude guida rail"
  Base = -> Sketch015
  Dir = (0,-1,2e-16)
  DirMode = 2
  FaceMakerClass = Part::FaceMakerBullseye
  FaceMakerMode = 3
  LengthFwd = 9
  LengthRev = 0
  Solid = true
  Symmetric = true
FEATURE [Sketcher::SketchObject] Sketch016  label="guide per coperture laterali"
  ArcFitTolerance = 1e-06
  AttachmentSupport = -> [XZ_Plane]
  ExternalGeometry = -> [Sketch]
  FullyConstrained = true
  MakeInternals = false
  MapMode = 5
  Placement = pos=(0,0,0) rot=(1,0,0;1.5708rad)
  sketch-geometry (14):
    g0: Circle CenterX=-5.6 CenterY=7.6 CenterZ=0 NormalX=0 NormalY=0 NormalZ=1 AngleXU=0 Radius=1.6
    g1: Circle CenterX=-5.6 CenterY=7.6 CenterZ=0 NormalX=0 NormalY=0 NormalZ=1 AngleXU=0 Radius=4
    g2: Circle CenterX=-5.6 CenterY=34.8 CenterZ=0 NormalX=0 NormalY=0 NormalZ=1 AngleXU=0 Radius=1.6
    g3: Circle CenterX=-5.6 CenterY=34.8 CenterZ=0 NormalX=0 NormalY=0 NormalZ=1 AngleXU=0 Radius=4
    g4: Circle CenterX=-184.08 CenterY=34.8 CenterZ=0 NormalX=0 NormalY=0 NormalZ=1 AngleXU=0 Radius=1.6
    g5: Circle CenterX=-184.08 CenterY=34.8 CenterZ=0 NormalX=0 NormalY=0 NormalZ=1 AngleXU=0 Radius=4
    g6: Circle CenterX=-179.305 CenterY=-76.8316 CenterZ=0 NormalX=0 NormalY=0 NormalZ=1 AngleXU=0 Radius=1.6
    g7: Circle CenterX=-179.305 CenterY=-76.8316 CenterZ=0 NormalX=0 NormalY=0 NormalZ=1 AngleXU=0 Radius=4
    g8: Circle CenterX=-213.443 CenterY=-76.8316 CenterZ=0 NormalX=0 NormalY=0 NormalZ=1 AngleXU=0 Radius=1.6
    g9: Circle CenterX=-213.443 CenterY=-76.8316 CenterZ=0 NormalX=0 NormalY=0 NormalZ=1 AngleXU=0 Radius=4
    g10: Circle CenterX=-78.51 CenterY=7.6 CenterZ=0 NormalX=0 NormalY=0 NormalZ=1 AngleXU=0 Radius=1.6
    g11: Circle CenterX=-78.51 CenterY=7.6 CenterZ=0 NormalX=0 NormalY=0 NormalZ=1 AngleXU=0 Radius=4
    g12: Circle CenterX=-78.51 CenterY=34.8 CenterZ=0 NormalX=0 NormalY=0 NormalZ=1 AngleXU=0 Radius=1.6
    g13: Circle CenterX=-78.51 CenterY=34.8 CenterZ=0 NormalX=0 NormalY=0 NormalZ=1 AngleXU=0 Radius=4
  constraints (35):
    c: Diameter(g0) = 3.2
    c: Diameter(g1) = 8
    c: Coincident(g0,g1)
    c: Diameter(g2) = 3.2
    c: Diameter(g3) = 8
    c: Coincident(g3,g2)
    c: Tangent(g2,g-7)
    c: Diameter(g4) = 3.2
    c: Diameter(g5) = 8
    c: Coincident(g5,g4)
    c: Tangent(g4,g-7)
    c: Tangent(g4,g-8)
    c: Diameter(g6) = 3.2
    c: Diameter(g7) = 8
    c: Coincident(g7,g6)
    c: Tangent(g6,g-9)
    c: Tangent(g6,g-10)
    c: Diameter(g8) = 3.2
    c: Diameter(g9) = 8
    c: Coincident(g9,g8)
    c: Tangent(g8,g-10)
    c: Tangent(g8,g-11)
    c: Diameter(g10) = 3.2
    c: Diameter(g11) = 8
    c: Diameter(g12) = 3.2
    c: Diameter(g13) = 8
    c: Coincident(g12,g13)
    c: Coincident(g10,g11)
    c: Tangent(g12,g-7)
    c: DistanceX(g12,g10) = 0
    c: Tangent(g2,g-6)
    c: Tangent(g0,g-6)
    c: Tangent(g0,g-3)
    c: Tangent(g10,g-3)
    c: Tangent(g10,g-4)
FEATURE [Part::Extrusion] Extrude012  label="extrude guide per coperture laterali"
  Base = -> Sketch016
  Dir = (0,-1,2e-16)
  DirMode = 2
  FaceMakerClass = Part::FaceMakerBullseye
  FaceMakerMode = 3
  LengthFwd = 25.2
  LengthRev = 0
  Solid = true
  Symmetric = true
FEATURE [Sketcher::SketchObject] Sketch017  label="supporto CAM"
  ArcFitTolerance = 1e-06
  AttachmentSupport = -> [XZ_Plane]
  ExternalGeometry = -> [Sketch]
  FullyConstrained = true
  MakeInternals = false
  MapMode = 5
  Placement = pos=(0,0,0) rot=(1,0,0;1.5708rad)
  sketch-geometry (6):
    g0: LineSegment StartX=-2.4 StartY=48 StartZ=0 EndX=-2.4 EndY=41.2 EndZ=0
    g1: LineSegment StartX=-2.4 StartY=48 StartZ=0 EndX=-34 EndY=48 EndZ=0
    g2: LineSegment StartX=-34 StartY=48 StartZ=0 EndX=-34 EndY=46.72 EndZ=0
    g3: LineSegment StartX=-34 StartY=46.72 StartZ=0 EndX=-36 EndY=46.72 EndZ=0
    g4: LineSegment StartX=-36 StartY=46.72 StartZ=0 EndX=-36 EndY=41.2 EndZ=0
    g5: LineSegment StartX=-36 StartY=41.2 StartZ=0 EndX=-2.4 EndY=41.2 EndZ=0
  constraints (15):
    c: Coincident(g1,g0)
    c: Horizontal(g1)
    c: Coincident(g2,g1)
    c: Vertical(g2)
    c: Coincident(g3,g2)
    c: Horizontal(g3)
    c: Coincident(g4,g3)
    c: Coincident(g5,g4)
    c: DistanceX(g1,g0) = 31.6
    c: Coincident(g5,g0)
    c: Vertical(g4)
    c: DistanceY(g2,g1) = 1.28
    c: Coincident(g0,g-3)
    c: Coincident(g0,g-3)
    c: Coincident(g4,g-4)
FEATURE [Part::Extrusion] Extrude013  label="Extrude supporto CAM"
  Base = -> Sketch017
  Dir = (0,-1,2e-16)
  DirMode = 2
  FaceMakerClass = Part::FaceMakerBullseye
  FaceMakerMode = 3
  LengthFwd = 17.8
  LengthRev = 0
  Solid = true
  Symmetric = true
FEATURE [Sketcher::SketchObject] Sketch018  label="Scavo CAM"
  ArcFitTolerance = 1e-06
  AttachmentSupport = -> [YZ_Plane]
  ExternalGeometry = -> [Sketch]
  FullyConstrained = true
  MakeInternals = false
  MapMode = 5
  Placement = pos=(0,0,0) rot=(0.57735,0.57735,0.57735;2.0944rad)
  sketch-geometry (4):
    g0: LineSegment StartX=-7.73 StartY=48 StartZ=0 EndX=7.73 EndY=48 EndZ=0
    g1: LineSegment [constr] StartX=1.07e-14 StartY=48 StartZ=0 EndX=0 EndY=43.5155 EndZ=0
    g2: ArcOfCircle CenterX=9e-15 CenterY=52.42 CenterZ=0 NormalX=0 NormalY=0 NormalZ=1 AngleXU=0 Radius=8.90445 StartAngle=3.66102 EndAngle=5.76376
    g3: Circle [constr] CenterX=9e-15 CenterY=52.42 CenterZ=0 NormalX=0 NormalY=0 NormalZ=1 AngleXU=0 Radius=8.9
  constraints (13):
    c: Horizontal(g0)
    c: DistanceY(g-3,g0) = 0
    c: DistanceX(g0,g0) = 15.46
    c: DistanceX(g0,g-3) = 7.73
    c: DistanceX(g-3) = 0
    c: Coincident(g1,g-3)
    c: PointOnObject(g1,g-2)
    c: Coincident(g2,g0)
    c: Coincident(g2,g0)
    c: PointOnObject(g1,g2)
    c: Diameter(g3) = 17.8
    c: DistanceY(g1,g3) = 4.42
    c: Coincident(g2,g3)
FEATURE [Part::Extrusion] Extrude014  label="Extrude Scavo CAM"
  Base = -> Sketch018
  Dir = (1,0,0)
  DirMode = 2
  FaceMakerClass = Part::FaceMakerBullseye
  FaceMakerMode = 3
  LengthFwd = -34
  LengthRev = 0
  Solid = true
  Symmetric = false
FEATURE [Sketcher::SketchObject] Sketch019  label="scavo rumble"
  ArcFitTolerance = 1e-06
  AttachmentSupport = -> [XZ_Plane]
  ExternalGeometry = -> [Sketch]
  FullyConstrained = true
  MakeInternals = false
  MapMode = 5
  Placement = pos=(0,0,0) rot=(1,0,0;1.5708rad)
  sketch-geometry (6):
    g0: LineSegment StartX=-164.266 StartY=-23.4275 StartZ=0 EndX=-159.13 EndY=-25.0962 EndZ=0
    g1: LineSegment StartX=-159.13 StartY=-25.0962 StartZ=0 EndX=-166.238 EndY=-46.9705 EndZ=0
    g2: LineSegment StartX=-166.238 StartY=-46.9705 StartZ=0 EndX=-171.373 EndY=-45.3018 EndZ=0
    g3: LineSegment StartX=-171.373 StartY=-45.3018 StartZ=0 EndX=-164.266 EndY=-23.4275 EndZ=0
    g4: LineSegment [constr] StartX=-145.51 StartY=22 StartZ=0 EndX=-160.652 EndY=-24.6018 EndZ=0
    g5: LineSegment [constr] StartX=-159.13 StartY=-25.0962 StartZ=0 EndX=-160.652 EndY=-24.6018 EndZ=0
  constraints (17):
    c: Coincident(g1,g0)
    c: Coincident(g2,g1)
    c: Coincident(g3,g2)
    c: Coincident(g3,g0)
    c: Parallel(g3,g-3)
    c: Parallel(g3,g1)
    c: Perpendicular(g3,g0)
    c: Perpendicular(g2,g3)
    c: Distance(g2,g0) = 23
    c: Parallel(g4,g-3)
    c: Distance(g4) = 49
    c: Coincident(g4,g-3)
    c: Parallel(g5,g0)
    c: Distance(g5) = 1.6
    c: Coincident(g5,g0)
    c: Distance(g5,g0) = 3.8
    c: Coincident(g5,g4)
FEATURE [Part::Extrusion] Extrude015  label="scavo rumble001"
  Base = -> Sketch019
  Dir = (0,-1,2e-16)
  DirMode = 2
  FaceMakerClass = Part::FaceMakerBullseye
  FaceMakerMode = 3
  LengthFwd = 21
  LengthRev = 0
  Solid = true
  Symmetric = true
FEATURE [Sketcher::SketchObject] Sketch020  label="fermo rumble"
  ArcFitTolerance = 1e-06
  AttachmentSupport = -> [XZ_Plane]
  ExternalGeometry = -> [Sketch019,Sketch]
  FullyConstrained = true
  MakeInternals = false
  MapMode = 5
  Placement = pos=(0,0,0) rot=(1,0,0;1.5708rad)
  sketch-geometry (16):
    g0: LineSegment [constr] StartX=-166.4 StartY=-42.2914 StartZ=0 EndX=-167.759 EndY=-46.4761 EndZ=0
    g1: LineSegment [constr] StartX=-167.759 StartY=-46.4761 StartZ=0 EndX=-166.238 EndY=-46.9705 EndZ=0
    g2: LineSegment StartX=-167.812 StartY=-39.5193 StartZ=0 EndX=-165.72 EndY=-40.1991 EndZ=0
    g3: LineSegment StartX=-165.72 StartY=-40.1991 StartZ=0 EndX=-166.4 EndY=-42.2914 EndZ=0
    g4: LineSegment StartX=-166.4 StartY=-42.2914 StartZ=0 EndX=-168.492 EndY=-41.6116 EndZ=0
    g5: LineSegment StartX=-168.492 StartY=-41.6116 StartZ=0 EndX=-167.812 EndY=-39.5193 EndZ=0
    g6: LineSegment StartX=-167.318 StartY=-37.9976 StartZ=0 EndX=-163.894 EndY=-39.11 EndZ=0
    g7: LineSegment StartX=-163.894 StartY=-39.11 StartZ=0 EndX=-165.501 EndY=-44.0555 EndZ=0
    g8: LineSegment StartX=-165.501 StartY=-44.0555 StartZ=0 EndX=-168.924 EndY=-42.9431 EndZ=0
    g9: LineSegment StartX=-169.952 StartY=-40.9269 StartZ=0 EndX=-169.334 EndY=-39.0248 EndZ=0
    g10: LineSegment [constr] StartX=-169.334 StartY=-39.0248 StartZ=0 EndX=-168.839 EndY=-37.5031 EndZ=0
    g11: LineSegment [constr] StartX=-168.839 StartY=-37.5031 StartZ=0 EndX=-167.318 EndY=-37.9976 EndZ=0
    g12: ArcOfCircle CenterX=-168.43 CenterY=-41.4214 CenterZ=0 NormalX=0 NormalY=0 NormalZ=1 AngleXU=0 Radius=1.6 StartAngle=2.82743 EndAngle=4.39823
    g13: GeomPoint [constr] X=-170.446 Y=-42.4486 Z=0
    g14: ArcOfCircle CenterX=-167.812 CenterY=-39.5193 CenterZ=0 NormalX=0 NormalY=0 NormalZ=1 AngleXU=0 Radius=1.6 StartAngle=1.25664 EndAngle=2.82743
    g15: GeomPoint [constr] X=-168.839 Y=-37.5031 Z=0
  constraints (42):
    c: Parallel(g0,g-4)
    c: Distance(g0) = 4.4
    c: Coincident(g1,g0)
    c: Perpendicular(g0,g1)
    c: Distance(g1) = 1.6
    c: Coincident(g1,g-5)
    c: Coincident(g3,g2)
    c: Coincident(g4,g3)
    c: Coincident(g5,g4)
    c: Coincident(g5,g2)
    c: Parallel(g3,g-4)
    c: Parallel(g3,g5)
    c: Perpendicular(g2,g3)
    c: Parallel(g4,g2)
    c: Distance(g2) = 2.2
    c: Distance(g3) = 2.2
    c: Coincident(g7,g6)
    c: Coincident(g8,g7)
    c: Parallel(g7,g-4)
    c: Parallel(g7,g9)
    c: Perpendicular(g6,g7)
    c: Parallel(g6,g8)
    c: Distance(g6,g15) = 5.2
    c: Distance(g7) = 5.2
    c: Coincident(g11,g10)
    c: Parallel(g10,g9)
    c: Parallel(g11,g6)
    c: Distance(g10) = 1.6
    c: Distance(g11) = 1.6
    c: Coincident(g10,g15)
    c: Distance(g11,g2) = 1.6
    c: Distance(g2,g10) = 1.6
    c: PointOnObject(g13,g8)
    c: PointOnObject(g13,g9)
    c: Tangent(g8,g12) = 1.5708
    c: Tangent(g9,g12) = 1.5708
    c: PointOnObject(g15,g9)
    c: Tangent(g6,g14) = 1.5708
    c: Tangent(g9,g14) = 1.5708
    c: Equal(g12,g14)
    c: Coincident(g6,g11)
    c: Coincident(g3,g0)
FEATURE [Part::Extrusion] Extrude016  label="Extrude fermo rumble"
  Base = -> Sketch020
  Dir = (0,-1,2e-16)
  DirMode = 2
  FaceMakerClass = Part::FaceMakerBullseye
  FaceMakerMode = 3
  LengthFwd = 25.2
  LengthRev = 0
  Solid = true
  Symmetric = true
FEATURE [Sketcher::SketchObject] Sketch021  label="perno fermo rumble001"
  ArcFitTolerance = 1e-06
  AttachmentSupport = -> [XZ_Plane001]
  FullyConstrained = true
  MakeInternals = false
  MapMode = 5
  Placement = pos=(0,0,0) rot=(1,0,0;1.5708rad)
  sketch-geometry (16):
    g0: LineSegment StartX=0 StartY=0.45 StartZ=0 EndX=0 EndY=1.55 EndZ=0
    g1: LineSegment StartX=0.45 StartY=2 StartZ=0 EndX=1.55 EndY=2 EndZ=0
    g2: LineSegment StartX=2 StartY=1.55 StartZ=0 EndX=2 EndY=0.45 EndZ=0
    g3: LineSegment StartX=1.55 StartY=0 StartZ=0 EndX=0.45 EndY=0 EndZ=0
    g4: ArcOfCircle [constr] CenterX=0.45 CenterY=1.55 CenterZ=0 NormalX=0 NormalY=0 NormalZ=1 AngleXU=0 Radius=0.45 StartAngle=1.5708 EndAngle=3.14159
    g5: GeomPoint [constr] X=0 Y=2 Z=0
    g6: LineSegment StartX=0.45 StartY=2 StartZ=0 EndX=0 EndY=1.55 EndZ=0
    g7: ArcOfCircle [constr] CenterX=1.55 CenterY=1.55 CenterZ=0 NormalX=0 NormalY=0 NormalZ=1 AngleXU=0 Radius=0.45 StartAngle=0 EndAngle=1.5708
    g8: GeomPoint [constr] X=2 Y=2 Z=0
    g9: LineSegment StartX=2 StartY=1.55 StartZ=0 EndX=1.55 EndY=2 EndZ=0
    g10: ArcOfCircle [constr] CenterX=1.55 CenterY=0.45 CenterZ=0 NormalX=0 NormalY=0 NormalZ=1 AngleXU=0 Radius=0.45 StartAngle=4.71239 EndAngle=6.28319
    g11: GeomPoint [constr] X=2 Y=0 Z=0
    g12: LineSegment StartX=1.55 StartY=0 StartZ=0 EndX=2 EndY=0.45 EndZ=0
    g13: ArcOfCircle [constr] CenterX=0.45 CenterY=0.45 CenterZ=0 NormalX=0 NormalY=0 NormalZ=1 AngleXU=0 Radius=0.45 StartAngle=3.14159 EndAngle=4.71239
    g14: GeomPoint [constr] X=0 Y=0 Z=0
    g15: LineSegment StartX=0 StartY=0.45 StartZ=0 EndX=0.45 EndY=0 EndZ=0
  constraints (35):
    c: Coincident(g14,g-1)
    c: PointOnObject(g5,g-2)
    c: Horizontal(g1)
    c: Vertical(g2)
    c: Horizontal(g3)
    c: DistanceX(g5,g8) = 2
    c: DistanceY(g11,g8) = 2
    c: PointOnObject(g5,g0)
    c: PointOnObject(g5,g1)
    c: Tangent(g0,g4) = 1.5708
    c: Tangent(g1,g4) = 1.5708
    c: Coincident(g6,g0)
    c: Coincident(g6,g1)
    c: PointOnObject(g8,g2)
    c: PointOnObject(g8,g1)
    c: Tangent(g2,g7) = 1.5708
    c: Tangent(g1,g7) = 1.5708
    c: Coincident(g9,g2)
    c: Coincident(g9,g1)
    c: PointOnObject(g11,g2)
    c: PointOnObject(g11,g3)
    c: Tangent(g2,g10) = 1.5708
    c: Tangent(g3,g10) = 1.5708
    c: Coincident(g12,g2)
    c: Coincident(g12,g3)
    c: PointOnObject(g14,g0)
    c: PointOnObject(g14,g3)
    c: Tangent(g0,g13) = 1.5708
    c: Tangent(g3,g13) = 1.5708
    c: Coincident(g15,g0)
    c: Coincident(g15,g3)
    c: Equal(g6,g9)
    c: Equal(g9,g12)
    c: Equal(g12,g15)
    c: DistanceX(g14,g3) = 0.45
FEATURE [Sketcher::SketchObject] Sketch022  label="fori per M3x5(OD)x6(L)"
  ArcFitTolerance = 1e-06
  AttachmentSupport = -> [XZ_Plane]
  ExternalGeometry = -> [Sketch016]
  FullyConstrained = true
  MakeInternals = false
  MapMode = 5
  Placement = pos=(0,0,0) rot=(1,0,0;1.5708rad)
  sketch-geometry (7):
    g0: Circle CenterX=-5.6 CenterY=34.8 CenterZ=0 NormalX=0 NormalY=0 NormalZ=1 AngleXU=0 Radius=2.5
    g1: Circle CenterX=-5.6 CenterY=7.6 CenterZ=0 NormalX=0 NormalY=0 NormalZ=1 AngleXU=0 Radius=2.5
    g2: Circle CenterX=-78.51 CenterY=34.8 CenterZ=0 NormalX=0 NormalY=0 NormalZ=1 AngleXU=0 Radius=2.5
    g3: Circle CenterX=-78.51 CenterY=7.6 CenterZ=0 NormalX=0 NormalY=0 NormalZ=1 AngleXU=0 Radius=2.5
    g4: Circle CenterX=-184.08 CenterY=34.8 CenterZ=0 NormalX=0 NormalY=0 NormalZ=1 AngleXU=0 Radius=2.5
    g5: Circle CenterX=-179.305 CenterY=-76.8316 CenterZ=0 NormalX=0 NormalY=0 NormalZ=1 AngleXU=0 Radius=2.5
    g6: Circle CenterX=-213.443 CenterY=-76.8316 CenterZ=0 NormalX=0 NormalY=0 NormalZ=1 AngleXU=0 Radius=2.5
  constraints (14):
    c: Diameter(g0) = 5
    c: Diameter(g1) = 5
    c: Diameter(g2) = 5
    c: Diameter(g3) = 5
    c: Diameter(g4) = 5
    c: Diameter(g5) = 5
    c: Diameter(g6) = 5
    c: Coincident(g0,g-8)
    c: Coincident(g1,g-9)
    c: Coincident(g2,g-6)
    c: Coincident(g3,g-7)
    c: Coincident(g4,g-5)
    c: Coincident(g5,g-4)
    c: Coincident(g6,g-3)
FEATURE [Part::Extrusion] Extrude018  label="Extrude fori M3x5x6 - dx"
  Base = -> Sketch022
  Dir = (0,-1,2e-16)
  DirMode = 2
  FaceMakerClass = Part::FaceMakerBullseye
  FaceMakerMode = 3
  LengthFwd = 6.2
  LengthRev = 0
  Placement = pos=(0,-9.5,0) rot=(0,0,1;0rad)
  Solid = true
  Symmetric = true
FEATURE [Part::Extrusion] Extrude019  label="Extrude fori M3x5x6 - sx"
  Base = -> Sketch022
  Dir = (0,-1,2e-16)
  DirMode = 2
  FaceMakerClass = Part::FaceMakerBullseye
  FaceMakerMode = 3
  LengthFwd = 6.2
  LengthRev = 0
  Placement = pos=(0,9.5,0) rot=(0,0,1;0rad)
  Solid = true
  Symmetric = true
FEATURE [Sketcher::SketchObject] Sketch023  label="foro anteriore M3x5x6"
  ArcFitTolerance = 1e-06
  AttachmentSupport = -> [YZ_Plane]
  FullyConstrained = true
  MakeInternals = false
  MapMode = 5
  Placement = pos=(0,0,0) rot=(0.57735,0.57735,0.57735;2.0944rad)
  sketch-geometry (2):
    g0: LineSegment [constr] StartX=0 StartY=0 StartZ=0 EndX=0 EndY=38.6 EndZ=0
    g1: Circle CenterX=0 CenterY=38.6 CenterZ=0 NormalX=0 NormalY=0 NormalZ=1 AngleXU=0 Radius=2.5
  constraints (5):
    c: Coincident(g0,g-1)
    c: PointOnObject(g0,g-2)
    c: DistanceY(g0,g0) = 38.6
    c: Diameter(g1) = 5
    c: Coincident(g1,g0)
FEATURE [Part::Extrusion] Extrude020  label="Extrude foro anteriore M3x5x6"
  Base = -> Sketch023
  Dir = (1,0,0)
  DirMode = 2
  FaceMakerClass = Part::FaceMakerBullseye
  FaceMakerMode = 3
  LengthFwd = -6.2
  LengthRev = 0
  Solid = true
  Symmetric = false
FEATURE [Sketcher::SketchObject] Sketch024  label="fori per viti frontale"
  ArcFitTolerance = 1e-06
  AttachmentSupport = -> [YZ_Plane]
  FullyConstrained = true
  MakeInternals = false
  MapMode = 5
  Placement = pos=(0,0,0) rot=(0.57735,0.57735,0.57735;2.0944rad)
  sketch-geometry (9):
    g0: LineSegment [constr] StartX=-10.3 StartY=30.721 StartZ=0 EndX=10.3 EndY=30.721 EndZ=0
    g1: LineSegment [constr] StartX=10.3 StartY=30.721 StartZ=0 EndX=10.3 EndY=10.121 EndZ=0
    g2: LineSegment [constr] StartX=10.3 StartY=10.121 StartZ=0 EndX=-10.3 EndY=10.121 EndZ=0
    g3: LineSegment [constr] StartX=-10.3 StartY=10.121 StartZ=0 EndX=-10.3 EndY=30.721 EndZ=0
    g4: LineSegment [constr] StartX=0 StartY=0 StartZ=0 EndX=0 EndY=10.121 EndZ=0
    g5: Circle CenterX=-10.3 CenterY=30.721 CenterZ=0 NormalX=0 NormalY=0 NormalZ=1 AngleXU=0 Radius=2
    g6: Circle CenterX=10.3 CenterY=30.721 CenterZ=0 NormalX=0 NormalY=0 NormalZ=1 AngleXU=0 Radius=2
    g7: Circle CenterX=-10.3 CenterY=10.121 CenterZ=0 NormalX=0 NormalY=0 NormalZ=1 AngleXU=0 Radius=2
    g8: Circle CenterX=10.3 CenterY=10.121 CenterZ=0 NormalX=0 NormalY=0 NormalZ=1 AngleXU=0 Radius=2
  constraints (22):
    c: Horizontal(g0)
    c: Coincident(g1,g0)
    c: Vertical(g1)
    c: Coincident(g2,g1)
    c: Horizontal(g2)
    c: Coincident(g3,g2)
    c: Coincident(g3,g0)
    c: Vertical(g3)
    c: DistanceX(g0,g0) = 20.6
    c: DistanceY(g3,g3) = 20.6
    c: Coincident(g4,g-1)
    c: PointOnObject(g4,g-2)
    c: DistanceY(g4,g4) = 10.121
    c: Symmetric(g2,g2,g4)
    c: Diameter(g5) = 4
    c: Diameter(g6) = 4
    c: Diameter(g7) = 4
    c: Diameter(g8) = 4
    c: Coincident(g5,g0)
    c: Coincident(g6,g0)
    c: Coincident(g7,g2)
    c: Coincident(g8,g1)
FEATURE [Part::Extrusion] Extrude021  label="Extrude fori per viti frontale"
  Base = -> Sketch024
  Dir = (1,0,0)
  DirMode = 2
  FaceMakerClass = Part::FaceMakerBullseye
  FaceMakerMode = 3
  LengthFwd = -2.4
  LengthRev = 0
  Solid = true
  Symmetric = false
FEATURE [Sketcher::SketchObject] Sketch025  label="foro per filo CAM"
  ArcFitTolerance = 1e-06
  AttachmentSupport = -> [XZ_Plane]
  ExternalGeometry = -> [Sketch]
  FullyConstrained = true
  MakeInternals = false
  MapMode = 5
  Placement = pos=(0,0,0) rot=(1,0,0;1.5708rad)
  sketch-geometry (4):
    g0: LineSegment StartX=-44.6 StartY=41.2 StartZ=0 EndX=-44.6 EndY=36.4 EndZ=0
    g1: LineSegment StartX=-44.6 StartY=36.4 StartZ=0 EndX=-54.6 EndY=36.4 EndZ=0
    g2: LineSegment StartX=-54.6 StartY=36.4 StartZ=0 EndX=-50.4 EndY=41.2 EndZ=0
    g3: LineSegment StartX=-50.4 StartY=41.2 StartZ=0 EndX=-44.6 EndY=41.2 EndZ=0
  constraints (11):
    c: Vertical(g0)
    c: Coincident(g1,g0)
    c: Horizontal(g1)
    c: Coincident(g2,g1)
    c: Coincident(g3,g2)
    c: Coincident(g3,g0)
    c: Horizontal(g3)
    c: Coincident(g0,g-3)
    c: DistanceY(g0,g-4) = 0
    c: DistanceX(g3,g3) = 5.8
    c: DistanceX(g1,g1) = 10
FEATURE [Part::Extrusion] Extrude022  label="Extrude foro per filo CAM dx"
  Base = -> Sketch025
  Dir = (0,-1,2e-16)
  DirMode = 2
  FaceMakerClass = Part::FaceMakerBullseye
  FaceMakerMode = 3
  LengthFwd = 4.9
  LengthRev = 0
  Placement = pos=(0,6.95,0) rot=(0,0,1;0rad)
  Solid = true
  Symmetric = true
FEATURE [Part::Extrusion] Extrude023  label="Extrude foro per filo CAM sx"
  Base = -> Sketch025
  Dir = (0,-1,2e-16)
  DirMode = 2
  FaceMakerClass = Part::FaceMakerBullseye
  FaceMakerMode = 3
  LengthFwd = 4.9
  LengthRev = 0
  Placement = pos=(0,-6.95,0) rot=(0,0,1;0rad)
  Solid = true
  Symmetric = true
FEATURE [Sketcher::SketchObject] Sketch026  label="foro sotto anteriore M3x5x6"
  ArcFitTolerance = 1e-06
  AttachmentSupport = -> [XY_Plane]
  FullyConstrained = true
  MakeInternals = false
  MapMode = 5
  sketch-geometry (2):
    g0: LineSegment [constr] StartX=0 StartY=0 StartZ=0 EndX=-16.5 EndY=0 EndZ=0
    g1: Circle CenterX=-16.5 CenterY=0 CenterZ=0 NormalX=0 NormalY=0 NormalZ=1 AngleXU=0 Radius=2.5
  constraints (5):
    c: Distance(g0) = 16.5
    c: Coincident(g0,g-1)
    c: PointOnObject(g0,g-1)
    c: Diameter(g1) = 5
    c: Coincident(g0,g1)
FEATURE [Sketcher::SketchObject] Sketch027  label="foro sotto posteriore M3x5x6"
  ArcFitTolerance = 1e-06
  AttachmentSupport = -> [XY_Plane]
  ExternalGeometry = -> [Sketch]
  FullyConstrained = true
  MakeInternals = false
  MapMode = 5
  sketch-geometry (2):
    g0: LineSegment [constr] StartX=-82.8 StartY=2e-16 StartZ=0 EndX=-71.3 EndY=2e-16 EndZ=0
    g1: Circle CenterX=-71.3 CenterY=2e-16 CenterZ=0 NormalX=0 NormalY=0 NormalZ=1 AngleXU=0 Radius=2.5
  constraints (5):
    c: Distance(g0) = 11.5
    c: Coincident(g0,g-3)
    c: PointOnObject(g0,g-3)
    c: Diameter(g1) = 5
    c: Coincident(g1,g0)
FEATURE [Sketcher::SketchObject] Sketch029  label="fori sotto impugnatura"
  ArcFitTolerance = 1e-06
  AttachmentSupport = -> [XY_Plane]
  ExternalGeometry = -> [Sketch]
  FullyConstrained = true
  MakeInternals = false
  MapMode = 5
  sketch-geometry (15):
    g0: LineSegment [constr] StartX=-175.232 StartY=-1.83e-14 StartZ=0 EndX=-191.232 EndY=0 EndZ=0
    g1: Circle CenterX=-191.232 CenterY=0 CenterZ=0 NormalX=0 NormalY=0 NormalZ=1 AngleXU=0 Radius=3.95
    g2: LineSegment [constr] StartX=-175.232 StartY=-1.83e-14 StartZ=0 EndX=-204.275 EndY=0 EndZ=0
    g3: LineSegment StartX=-204.275 StartY=3.525 StartZ=0 EndX=-204.275 EndY=-3.525 EndZ=0
    g4: LineSegment StartX=-205.4 StartY=-4.65 StartZ=0 EndX=-206.65 EndY=-4.65 EndZ=0
    g5: LineSegment StartX=-207.775 StartY=-3.525 StartZ=0 EndX=-207.775 EndY=3.525 EndZ=0
    g6: LineSegment StartX=-206.65 StartY=4.65 StartZ=0 EndX=-205.4 EndY=4.65 EndZ=0
    g7: ArcOfCircle CenterX=-206.65 CenterY=3.525 CenterZ=0 NormalX=0 NormalY=0 NormalZ=1 AngleXU=0 Radius=1.125 StartAngle=1.5708 EndAngle=3.14159
    g8: GeomPoint [constr] X=-207.775 Y=4.65 Z=0
    g9: ArcOfCircle CenterX=-205.4 CenterY=3.525 CenterZ=0 NormalX=0 NormalY=0 NormalZ=1 AngleXU=0 Radius=1.125 StartAngle=0 EndAngle=1.5708
    g10: GeomPoint [constr] X=-204.275 Y=4.65 Z=0
    g11: ArcOfCircle CenterX=-205.4 CenterY=-3.525 CenterZ=0 NormalX=0 NormalY=0 NormalZ=1 AngleXU=0 Radius=1.125 StartAngle=4.71239 EndAngle=6.28319
    g12: GeomPoint [constr] X=-204.275 Y=-4.65 Z=0
    g13: ArcOfCircle CenterX=-206.65 CenterY=-3.525 CenterZ=0 NormalX=0 NormalY=0 NormalZ=1 AngleXU=0 Radius=1.125 StartAngle=3.14159 EndAngle=4.71239
    g14: GeomPoint [constr] X=-207.775 Y=-4.65 Z=0
  constraints (35):
    c: Distance(g0) = 16
    c: Coincident(g0,g-3)
    c: PointOnObject(g0,g-1)
    c: Diameter(g1) = 7.9
    c: Coincident(g1,g0)
    c: Coincident(g2,g0)
    c: PointOnObject(g2,g-1)
    c: Vertical(g3)
    c: Horizontal(g4)
    c: Vertical(g5)
    c: Horizontal(g6)
    c: DistanceY(g12,g10) = 9.3
    c: DistanceX(g8,g10) = 3.5
    c: Symmetric(g10,g12,g2)
    c: PointOnObject(g8,g5)
    c: PointOnObject(g8,g6)
    c: Tangent(g5,g7) = 1.5708
    c: Tangent(g6,g7) = 1.5708
    c: PointOnObject(g10,g3)
    c: PointOnObject(g10,g6)
    c: Tangent(g3,g9) = 1.5708
    c: Tangent(g6,g9) = 1.5708
    c: PointOnObject(g12,g3)
    c: PointOnObject(g12,g4)
    c: Tangent(g3,g11) = 1.5708
    c: Tangent(g4,g11) = 1.5708
    c: PointOnObject(g14,g4)
    c: PointOnObject(g14,g5)
    c: Tangent(g4,g13) = 1.5708
    c: Tangent(g5,g13) = 1.5708
    c: Equal(g7,g9)
    c: Equal(g9,g11)
    c: Equal(g11,g13)
    c: DistanceX(g6,g6) = 1.25
    c: DistanceX(g-5,g5) = 6.8
FEATURE [Sketcher::SketchObject] Sketch030  label="fori superiori per solenoide e oled"
  ArcFitTolerance = 1e-06
  AttachmentSupport = -> [XY_Plane]
  ExternalGeometry = -> [Sketch]
  FullyConstrained = true
  MakeInternals = false
  MapMode = 5
  sketch-geometry (33):
    g0: LineSegment [constr] StartX=-181.6 StartY=1.12e-14 StartZ=0 EndX=-169.91 EndY=0 EndZ=0
    g1: LineSegment [constr] StartX=-169.91 StartY=0 StartZ=0 EndX=-169.91 EndY=-2.6 EndZ=0
    g2: LineSegment [constr] StartX=-169.91 StartY=0 StartZ=0 EndX=-169.91 EndY=2.6 EndZ=0
    g3: LineSegment StartX=-169.91 StartY=4.975 StartZ=0 EndX=-169.91 EndY=8.225 EndZ=0
    g4: LineSegment StartX=-167.535 StartY=10.6 StartZ=0 EndX=-167.285 EndY=10.6 EndZ=0
    g5: LineSegment StartX=-164.91 StartY=8.225 StartZ=0 EndX=-164.91 EndY=4.975 EndZ=0
    g6: LineSegment StartX=-167.285 StartY=2.6 StartZ=0 EndX=-167.535 EndY=2.6 EndZ=0
    g7: LineSegment StartX=-169.91 StartY=-4.975 StartZ=0 EndX=-169.91 EndY=-8.225 EndZ=0
    g8: LineSegment StartX=-167.535 StartY=-10.6 StartZ=0 EndX=-167.285 EndY=-10.6 EndZ=0
    g9: LineSegment StartX=-164.91 StartY=-8.225 StartZ=0 EndX=-164.91 EndY=-4.975 EndZ=0
    g10: LineSegment StartX=-167.285 StartY=-2.6 StartZ=0 EndX=-167.535 EndY=-2.6 EndZ=0
    g11: ArcOfCircle CenterX=-167.535 CenterY=8.225 CenterZ=0 NormalX=0 NormalY=0 NormalZ=1 AngleXU=0 Radius=2.375 StartAngle=1.5708 EndAngle=3.14159
    g12: GeomPoint [constr] X=-169.91 Y=10.6 Z=0
    g13: ArcOfCircle CenterX=-167.285 CenterY=8.225 CenterZ=0 NormalX=0 NormalY=0 NormalZ=1 AngleXU=0 Radius=2.375 StartAngle=0 EndAngle=1.5708
    g14: GeomPoint [constr] X=-164.91 Y=10.6 Z=0
    g15: ArcOfCircle CenterX=-167.285 CenterY=4.975 CenterZ=0 NormalX=0 NormalY=0 NormalZ=1 AngleXU=0 Radius=2.375 StartAngle=4.71239 EndAngle=6.28319
    g16: GeomPoint [constr] X=-164.91 Y=2.6 Z=0
    g17: ArcOfCircle CenterX=-167.535 CenterY=4.975 CenterZ=0 NormalX=0 NormalY=0 NormalZ=1 AngleXU=0 Radius=2.375 StartAngle=3.14159 EndAngle=4.71239
    g18: GeomPoint [constr] X=-169.91 Y=2.6 Z=0
    g19: ArcOfCircle CenterX=-167.535 CenterY=-4.975 CenterZ=0 NormalX=0 NormalY=0 NormalZ=1 AngleXU=0 Radius=2.375 StartAngle=1.5708 EndAngle=3.14159
    g20: GeomPoint [constr] X=-169.91 Y=-2.6 Z=0
    g21: ArcOfCircle CenterX=-167.285 CenterY=-4.975 CenterZ=0 NormalX=0 NormalY=0 NormalZ=1 AngleXU=0 Radius=2.375 StartAngle=0 EndAngle=1.5708
    g22: GeomPoint [constr] X=-164.91 Y=-2.6 Z=0
    g23: ArcOfCircle CenterX=-167.285 CenterY=-8.225 CenterZ=0 NormalX=0 NormalY=0 NormalZ=1 AngleXU=0 Radius=2.375 StartAngle=4.71239 EndAngle=6.28319
    g24: GeomPoint [constr] X=-164.91 Y=-10.6 Z=0
    g25: ArcOfCircle CenterX=-167.535 CenterY=-8.225 CenterZ=0 NormalX=0 NormalY=0 NormalZ=1 AngleXU=0 Radius=2.375 StartAngle=3.14159 EndAngle=4.71239
    g26: GeomPoint [constr] X=-169.91 Y=-10.6 Z=0
    g27: LineSegment [constr] StartX=-181.6 StartY=1.12e-14 StartZ=0 EndX=-152.209 EndY=0 EndZ=0
    g28: LineSegment [constr] StartX=-181.6 StartY=1.12e-14 StartZ=0 EndX=-130.41 EndY=0 EndZ=0
    g29: LineSegment [constr] StartX=-152.209 StartY=0 StartZ=0 EndX=-152.209 EndY=6.95 EndZ=0
    g30: LineSegment [constr] StartX=-130.41 StartY=0 StartZ=0 EndX=-130.41 EndY=-6.95 EndZ=0
    g31: Circle CenterX=-152.209 CenterY=6.95 CenterZ=0 NormalX=0 NormalY=0 NormalZ=1 AngleXU=0 Radius=2.1
    g32: Circle CenterX=-130.41 CenterY=-6.95 CenterZ=0 NormalX=0 NormalY=0 NormalZ=1 AngleXU=0 Radius=2.1
  constraints (79):
    c: Distance(g0) = 11.69
    c: PointOnObject(g0,g-1)
    c: Coincident(g-4,g0)
    c: Distance(g1) = 2.6
    c: Coincident(g1,g0)
    c: Vertical(g1)
    c: Distance(g2) = 2.6
    c: Coincident(g2,g0)
    c: Vertical(g2)
    c: Distance(g18,g12) = 8
    c: Coincident(g18,g2)
    c: Vertical(g3)
    c: Distance(g14,g12) = 5
    c: Horizontal(g4)
    c: Distance(g16,g14) = 8
    c: Vertical(g5)
    c: Distance(g26,g20) = 8
    c: Coincident(g20,g1)
    c: Vertical(g7)
    c: Distance(g26,g24) = 5
    c: Horizontal(g8)
    c: Distance(g24,g22) = 8
    c: Vertical(g9)
    c: PointOnObject(g12,g3)
    c: PointOnObject(g12,g4)
    c: Tangent(g3,g11) = 1.5708
    c: Tangent(g4,g11) = 1.5708
    c: PointOnObject(g14,g5)
    c: PointOnObject(g14,g4)
    c: Tangent(g5,g13) = 1.5708
    c: Tangent(g4,g13) = 1.5708
    c: PointOnObject(g16,g5)
    c: PointOnObject(g16,g6)
    c: Tangent(g5,g15) = 1.5708
    c: Tangent(g6,g15) = 1.5708
    c: PointOnObject(g18,g3)
    c: PointOnObject(g18,g6)
    c: Tangent(g3,g17) = 1.5708
    c: Tangent(g6,g17) = 1.5708
    c: Equal(g11,g13)
    c: Equal(g13,g15)
    c: Equal(g15,g17)
    c: DistanceX(g4,g4) = 0.25
    c: PointOnObject(g20,g7)
    c: PointOnObject(g20,g10)
    c: Tangent(g7,g19) = -1.5708
    c: Tangent(g10,g19) = -1.5708
    c: PointOnObject(g22,g9)
    c: PointOnObject(g22,g10)
    c: Tangent(g9,g21) = -1.5708
    c: Tangent(g10,g21) = -1.5708
    c: PointOnObject(g24,g9)
    c: PointOnObject(g24,g8)
    c: Tangent(g9,g23) = -1.5708
    c: Tangent(g8,g23) = -1.5708
    c: PointOnObject(g26,g8)
    c: PointOnObject(g26,g7)
    c: Tangent(g8,g25) = -1.5708
    c: Tangent(g7,g25) = -1.5708
    c: Equal(g19,g21)
    c: Equal(g21,g23)
    c: Equal(g23,g25)
    c: DistanceX(g10,g10) = 0.25
    c: Distance(g27) = 29.391
    c: Coincident(g27,g0)
    c: PointOnObject(g27,g-1)
    c: Distance(g28) = 51.19
    c: Coincident(g28,g0)
    c: PointOnObject(g28,g-1)
    c: Distance(g29) = 6.95
    c: Coincident(g29,g27)
    c: Vertical(g29)
    c: Distance(g30) = 6.95
    c: Coincident(g30,g28)
    c: Vertical(g30)
    c: Diameter(g31) = 4.2
    c: Diameter(g32) = 4.2
    c: Coincident(g32,g30)
    c: Coincident(g31,g29)
FEATURE [Sketcher::SketchObject] Sketch031  label="fori inferiori switch pompa"
  ArcFitTolerance = 1e-06
  AttachmentSupport = -> [XY_Plane]
  ExternalGeometry = -> [Sketch]
  FullyConstrained = true
  MakeInternals = false
  MapMode = 5
  sketch-geometry (4):
    g0: LineSegment [constr] StartX=-57.2 StartY=1.9e-15 StartZ=0 EndX=-62.45 EndY=1.9e-15 EndZ=0
    g1: LineSegment [constr] StartX=-62.45 StartY=3.25 StartZ=0 EndX=-62.45 EndY=-3.25 EndZ=0
    g2: Circle CenterX=-62.45 CenterY=3.25 CenterZ=0 NormalX=0 NormalY=0 NormalZ=1 AngleXU=0 Radius=1.6
    g3: Circle CenterX=-62.45 CenterY=-3.25 CenterZ=0 NormalX=0 NormalY=0 NormalZ=1 AngleXU=0 Radius=1.6
  constraints (10):
    c: Distance(g0) = 5.25
    c: Coincident(g0,g-3)
    c: PointOnObject(g0,g-3)
    c: Vertical(g1)
    c: DistanceY(g1,g1) = 6.5
    c: Symmetric(g1,g1,g0)
    c: Diameter(g2) = 3.2
    c: Diameter(g3) = 3.2
    c: Coincident(g2,g1)
    c: Coincident(g3,g1)
FEATURE [Sketcher::SketchObject] Sketch032  label="spazio per PILA 18650"
  ArcFitTolerance = 1e-06
  AttachmentSupport = -> [XY_Plane]
  ExternalGeometry = -> [Sketch]
  FullyConstrained = true
  MakeInternals = false
  MapMode = 5
  sketch-geometry (2):
    g0: LineSegment [constr] StartX=-178.142 StartY=-1.74e-14 StartZ=0 EndX=-191.142 EndY=-1.83e-14 EndZ=0
    g1: Circle CenterX=-191.142 CenterY=-1.83e-14 CenterZ=0 NormalX=0 NormalY=0 NormalZ=1 AngleXU=0 Radius=10.9
  constraints (5):
    c: Distance(g0) = 13
    c: Coincident(g0,g-3)
    c: PointOnObject(g0,g-4)
    c: Diameter(g1) = 21.8
    c: Coincident(g1,g0)
FEATURE [Part::Extrusion] Extrude030  label="Extrude spazio per PILA 18650"
  Base = -> Sketch032
  Dir = (0,0,1)
  DirLink = -> Sketch [Edge45]
  DirMode = 2
  FaceMakerClass = Part::FaceMakerBullseye
  FaceMakerMode = 3
  LengthFwd = 76
  LengthRev = 0
  Placement = pos=(6,0,-70) rot=(0,0,1;0rad)
  Solid = true
  Symmetric = false
FEATURE [Sketcher::SketchObject] Sketch033  label="fermo per scheda micro"
  ArcFitTolerance = 1e-06
  AttachmentSupport = -> [XZ_Plane]
  ExternalGeometry = -> [Sketch]
  FullyConstrained = true
  MakeInternals = false
  MapMode = 5
  Placement = pos=(0,0,0) rot=(1,0,0;1.5708rad)
  sketch-geometry (12):
    g0: LineSegment StartX=-11.6 StartY=6 StartZ=0 EndX=-4 EndY=6 EndZ=0
    g1: LineSegment StartX=-4 StartY=6 StartZ=0 EndX=-4 EndY=36.4 EndZ=0
    g2: LineSegment StartX=-4 StartY=36.4 StartZ=0 EndX=-11.6 EndY=36.4 EndZ=0
    g3: LineSegment StartX=-11.6 StartY=36.4 StartZ=0 EndX=-11.6 EndY=6 EndZ=0
    g4: LineSegment StartX=-80.11 StartY=11.6 StartZ=0 EndX=-70.51 EndY=11.6 EndZ=0
    g5: LineSegment StartX=-70.51 StartY=11.6 StartZ=0 EndX=-70.51 EndY=6 EndZ=0
    g6: LineSegment StartX=-70.51 StartY=6 StartZ=0 EndX=-80.11 EndY=6 EndZ=0
    g7: LineSegment StartX=-80.11 StartY=6 StartZ=0 EndX=-80.11 EndY=11.6 EndZ=0
    g8: LineSegment StartX=-78.51 StartY=36.4 StartZ=0 EndX=-70.51 EndY=36.4 EndZ=0
    g9: LineSegment StartX=-70.51 StartY=36.4 StartZ=0 EndX=-70.51 EndY=30.8 EndZ=0
    g10: LineSegment StartX=-70.51 StartY=30.8 StartZ=0 EndX=-78.51 EndY=30.8 EndZ=0
    g11: LineSegment StartX=-78.51 StartY=30.8 StartZ=0 EndX=-78.51 EndY=36.4 EndZ=0
  constraints (33):
    c: Horizontal(g0)
    c: Coincident(g1,g0)
    c: Coincident(g2,g1)
    c: Horizontal(g2)
    c: Coincident(g3,g2)
    c: Coincident(g3,g0)
    c: Vertical(g3)
    c: DistanceX(g2,g2) = 7.6
    c: Coincident(g1,g-3)
    c: Coincident(g0,g-3)
    c: Horizontal(g4)
    c: Coincident(g5,g4)
    c: Vertical(g5)
    c: Coincident(g6,g5)
    c: Horizontal(g6)
    c: Coincident(g7,g6)
    c: Coincident(g7,g4)
    c: Vertical(g7)
    c: DistanceY(g5,g5) = 5.6
    c: DistanceX(g4,g4) = 9.6
    c: Coincident(g9,g8)
    c: Vertical(g9)
    c: Coincident(g10,g9)
    c: Horizontal(g10)
    c: Coincident(g11,g10)
    c: Coincident(g11,g8)
    c: Vertical(g11)
    c: DistanceY(g9,g9) = 5.6
    c: DistanceX(g10,g10) = 8
    c: Coincident(g4,g-4)
    c: DistanceX(g4,g10) = 1.6
    c: Horizontal(g8)
    c: DistanceY(g8,g1) = 0
FEATURE [Sketcher::SketchObject] Sketch034  label="buchi guida rail"
  ArcFitTolerance = 1e-06
  AttachmentSupport = -> [XY_Plane]
  ExternalGeometry = -> [Sketch]
  FullyConstrained = true
  MakeInternals = false
  MapMode = 5
  sketch-geometry (6):
    g0: LineSegment [constr] StartX=-100.8 StartY=9.1e-15 StartZ=0 EndX=-93.3 EndY=0 EndZ=0
    g1: LineSegment [constr] StartX=-93.3 StartY=0 StartZ=0 EndX=-73.3 EndY=0 EndZ=0
    g2: LineSegment [constr] StartX=-73.3 StartY=0 StartZ=0 EndX=-53.3 EndY=0 EndZ=0
    g3: Circle CenterX=-93.3 CenterY=0 CenterZ=0 NormalX=0 NormalY=0 NormalZ=1 AngleXU=0 Radius=2.5
    g4: Circle CenterX=-73.3 CenterY=0 CenterZ=0 NormalX=0 NormalY=0 NormalZ=1 AngleXU=0 Radius=2.5
    g5: Circle CenterX=-53.3 CenterY=0 CenterZ=0 NormalX=0 NormalY=0 NormalZ=1 AngleXU=0 Radius=2.5
  constraints (15):
    c: Distance(g0) = 7.5
    c: Coincident(g0,g-3)
    c: PointOnObject(g0,g-1)
    c: Distance(g1) = 20
    c: Coincident(g1,g0)
    c: PointOnObject(g1,g-1)
    c: Distance(g2) = 20
    c: Coincident(g2,g1)
    c: PointOnObject(g2,g-1)
    c: Diameter(g3) = 5
    c: Diameter(g4) = 5
    c: Diameter(g5) = 5
    c: Coincident(g3,g0)
    c: Coincident(g4,g1)
    c: Coincident(g5,g2)
FEATURE [Part::Extrusion] Extrude032  label="Extrude buchi guida rail"
  Base = -> Sketch034
  Dir = (0,0,1)
  DirMode = 2
  FaceMakerClass = Part::FaceMakerBullseye
  FaceMakerMode = 3
  LengthFwd = -6.2
  LengthRev = 0
  Placement = pos=(0,0,43.2) rot=(0,0,1;0rad)
  Solid = true
  Symmetric = false
FEATURE [Part::Extrusion] Extrude033  label="Extrude fori superiori per solenoide e oled001"
  Base = -> Sketch030
  Dir = (0,0,1)
  DirMode = 2
  FaceMakerClass = Part::FaceMakerBullseye
  FaceMakerMode = 3
  LengthFwd = -4.8
  LengthRev = 0
  Placement = pos=(0,0,41.2) rot=(0,0,1;0rad)
  Solid = true
  Symmetric = false
FEATURE [Part::Extrusion] Extrude034  label="Extrude fori sotto impugnatura001"
  Base = -> Sketch029
  Dir = (0,0,1)
  DirMode = 2
  FaceMakerClass = Part::FaceMakerBullseye
  FaceMakerMode = 3
  LengthFwd = 5
  LengthRev = 0
  Placement = pos=(0,0,-83) rot=(0,0,1;0rad)
  Solid = true
  Symmetric = false
FEATURE [Part::Extrusion] Extrude035  label="Extrude fori inferiori switch pompa001"
  Base = -> Sketch031
  Dir = (0,0,1)
  DirMode = 2
  FaceMakerClass = Part::FaceMakerBullseye
  FaceMakerMode = 3
  LengthFwd = 4
  LengthRev = 0
  Placement = pos=(0,0,-1.7) rot=(0,0,1;0rad)
  Solid = true
  Symmetric = false
FEATURE [Part::Extrusion] Extrude036  label="Extrude foro sotto posteriore M3x5x007"
  Base = -> Sketch027
  Dir = (0,0,1)
  DirMode = 2
  FaceMakerClass = Part::FaceMakerBullseye
  FaceMakerMode = 3
  LengthFwd = 6.2
  LengthRev = 0
  Placement = pos=(0,0,-9.6) rot=(0,0,1;0rad)
  Solid = true
  Symmetric = false
FEATURE [Part::Extrusion] Extrude037  label="Extrude foro sotto anteriore M3x5x007"
  Base = -> Sketch026
  Dir = (0,0,1)
  DirMode = 2
  FaceMakerClass = Part::FaceMakerBullseye
  FaceMakerMode = 3
  LengthFwd = 6.2
  LengthRev = 0
  Solid = true
  Symmetric = false
FEATURE [Sketcher::SketchObject] Sketch035  label="foro per fissaggio micro"
  ArcFitTolerance = 1e-06
  AttachmentSupport = -> [XZ_Plane]
  ExternalGeometry = -> [Sketch,Sketch033]
  FullyConstrained = true
  MakeInternals = false
  MapMode = 5
  Placement = pos=(0,0,0) rot=(1,0,0;1.5708rad)
  sketch-geometry (3):
    g0: Circle CenterX=-7.8 CenterY=21.2 CenterZ=0 NormalX=0 NormalY=0 NormalZ=1 AngleXU=0 Radius=1.6
    g1: GeomPoint [constr] X=-4 Y=21.2 Z=0
    g2: LineSegment [constr] StartX=-4 StartY=21.2 StartZ=0 EndX=-11.6 EndY=21.2 EndZ=0
  constraints (6):
    c: Diameter(g0) = 3.2
    c: Symmetric(g-3,g-3,g1)
    c: Coincident(g2,g1)
    c: Horizontal(g2)
    c: DistanceX(g-4,g2) = 0
    c: Symmetric(g2,g1,g0)
FEATURE [Part::Extrusion] Extrude038  label="Extrude foro per fissaggio micro"
  Base = -> Sketch035
  Dir = (0,-1,2e-16)
  DirMode = 2
  FaceMakerClass = Part::FaceMakerBullseye
  FaceMakerMode = 3
  LengthFwd = 3
  LengthRev = 0
  Placement = pos=(0,8.6,0) rot=(0,0,1;0rad)
  Solid = true
  Symmetric = false
FEATURE [Sketcher::SketchObject] Sketch036  label="supporto per alimentatore"
  ArcFitTolerance = 1e-06
  AttachmentSupport = -> [XZ_Plane]
  ExternalGeometry = -> [Sketch,Sketch016,Sketch022]
  FullyConstrained = true
  MakeInternals = false
  MapMode = 5
  Placement = pos=(0,0,0) rot=(1,0,0;1.5708rad)
  sketch-geometry (5):
    g0: LineSegment StartX=-211.843 StartY=-50.0944 StartZ=0 EndX=-211.843 EndY=-80.4316 EndZ=0
    g1: LineSegment StartX=-211.843 StartY=-50.0944 StartZ=0 EndX=-207.775 EndY=-41.3701 EndZ=0
    g2: LineSegment [constr] StartX=-209.443 StartY=-50.0944 StartZ=0 EndX=-209.443 EndY=-80.4316 EndZ=0
    g3: LineSegment StartX=-207.775 StartY=-41.3701 StartZ=0 EndX=-207.775 EndY=-80.4316 EndZ=0
    g4: LineSegment StartX=-211.843 StartY=-80.4316 StartZ=0 EndX=-207.775 EndY=-80.4316 EndZ=0
  constraints (15):
    c: Vertical(g0)
    c: Coincident(g1,g0)
    c: Vertical(g2)
    c: Tangent(g2,g-5)
    c: Coincident(g3,g1)
    c: Vertical(g3)
    c: DistanceY(g-3,g3) = -2
    c: Tangent(g1,g-8)
    c: DistanceY(g-3,g0) = -2
    c: Coincident(g4,g0)
    c: Coincident(g4,g3)
    c: Tangent(g0,g-6)
    c: DistanceY(g-3,g2) = -2
    c: DistanceY(g2,g0) = 0
    c: DistanceX(g-3,g3) = 6.8
FEATURE [Part::Extrusion] Extrude039  label="Extrude039 supporto alimentatore"
  Base = -> Sketch036
  Dir = (0,-1,2e-16)
  DirMode = 2
  FaceMakerClass = Part::FaceMakerBullseye
  FaceMakerMode = 3
  LengthFwd = 25.2
  LengthRev = 0
  Solid = true
  Symmetric = true
FEATURE [Sketcher::SketchObject] Sketch037  label="scavo per alimentatore"
  ArcFitTolerance = 1e-06
  AttachmentSupport = -> [XZ_Plane]
  ExternalGeometry = -> [Sketch036]
  FullyConstrained = true
  MakeInternals = false
  MapMode = 5
  Placement = pos=(0,0,0) rot=(1,0,0;1.5708rad)
  sketch-geometry (4):
    g0: LineSegment StartX=-209.575 StartY=-50.4316 StartZ=0 EndX=-209.575 EndY=-80.4316 EndZ=0
    g1: LineSegment StartX=-209.575 StartY=-50.4316 StartZ=0 EndX=-207.775 EndY=-50.4316 EndZ=0
    g2: LineSegment StartX=-207.775 StartY=-50.4316 StartZ=0 EndX=-207.775 EndY=-80.4316 EndZ=0
    g3: LineSegment StartX=-207.775 StartY=-80.4316 StartZ=0 EndX=-209.575 EndY=-80.4316 EndZ=0
  constraints (11):
    c: Vertical(g0)
    c: Coincident(g1,g0)
    c: Horizontal(g1)
    c: Coincident(g2,g1)
    c: Vertical(g2)
    c: Coincident(g3,g2)
    c: Coincident(g3,g0)
    c: Horizontal(g3)
    c: DistanceX(g1,g1) = 1.8
    c: Coincident(g2,g-3)
    c: DistanceY(g2,g2) = 30
FEATURE [Part::Extrusion] Extrude040  label="Extrude040 scavo alimentatore"
  Base = -> Sketch037
  Dir = (0,-1,2e-16)
  DirMode = 2
  FaceMakerClass = Part::FaceMakerBullseye
  FaceMakerMode = 3
  LengthFwd = 19.5
  LengthRev = 0
  Solid = true
  Symmetric = true
FEATURE [Part::Extrusion] Extrude031  label="Extrude fermo per scheda micro"
  Base = -> Sketch033
  Dir = (0,-1,2e-16)
  DirMode = 2
  FaceMakerClass = Part::FaceMakerBullseye
  FaceMakerMode = 3
  LengthFwd = 3
  LengthRev = 0
  Placement = pos=(0,8.6,0) rot=(0,0,1;0rad)
  Solid = true
  Symmetric = false
FEATURE [Sketcher::SketchObject] Sketch038  label="scavo driver solenoide"
  ArcFitTolerance = 1e-06
  AttachmentSupport = -> [XZ_Plane]
  ExternalGeometry = -> [Sketch,Sketch036]
  FullyConstrained = true
  MakeInternals = false
  MapMode = 5
  Placement = pos=(0,0,0) rot=(1,0,0;1.5708rad)
  sketch-geometry (7):
    g0: LineSegment StartX=-190.448 StartY=-4.2115 StartZ=0 EndX=-191.898 EndY=-3.53531 EndZ=0
    g1: LineSegment StartX=-191.898 StartY=-3.53531 StartZ=0 EndX=-209.225 EndY=-40.6939 EndZ=0
    g2: LineSegment StartX=-190.448 StartY=-4.2115 StartZ=0 EndX=-187.004 EndY=-5.81745 EndZ=0
    g3: LineSegment StartX=-187.004 StartY=-5.81745 StartZ=0 EndX=-204.331 EndY=-42.9761 EndZ=0
    g4: LineSegment StartX=-204.331 StartY=-42.9761 StartZ=0 EndX=-207.775 EndY=-41.3701 EndZ=0
    g5: LineSegment [constr] StartX=-209.225 StartY=-40.6939 StartZ=0 EndX=-207.775 EndY=-41.3701 EndZ=0
    g6: LineSegment StartX=-209.225 StartY=-40.6939 StartZ=0 EndX=-207.775 EndY=-41.3701 EndZ=0
  constraints (19):
    c: Coincident(g1,g0)
    c: Coincident(g3,g2)
    c: Coincident(g4,g3)
    c: Distance(g2) = 3.8
    c: Distance(g1) = 41
    c: Coincident(g5,g1)
    c: Distance(g5) = 1.6
    c: Coincident(g-4,g5)
    c: Perpendicular(g5,g-3)
    c: Parallel(g1,g-3)
    c: Perpendicular(g1,g0)
    c: Distance(g0) = 1.6
    c: Coincident(g6,g1)
    c: Coincident(g6,g5)
    c: Parallel(g3,g-3)
    c: Perpendicular(g3,g4)
    c: Perpendicular(g2,g3)
    c: Coincident(g2,g0)
    c: Coincident(g4,g5)
FEATURE [Part::Extrusion] Extrude041  label="Extrude scavo driver solenoide"
  Base = -> Sketch038
  Dir = (0,-1,2e-16)
  DirMode = 2
  FaceMakerClass = Part::FaceMakerBullseye
  FaceMakerMode = 3
  LengthFwd = 20.8
  LengthRev = 0
  Solid = true
  Symmetric = true
FEATURE [Sketcher::SketchObject] Sketch039  label="scavo per cavo usb per micro"
  ArcFitTolerance = 1e-06
  AttachmentSupport = -> [XZ_Plane]
  ExternalGeometry = -> [Sketch,Sketch016]
  FullyConstrained = true
  MakeInternals = false
  MapMode = 5
  Placement = pos=(0,0,0) rot=(1,0,0;1.5708rad)
  sketch-geometry (4):
    g0: LineSegment StartX=-82.51 StartY=36.4 StartZ=0 EndX=-74.51 EndY=36.4 EndZ=0
    g1: LineSegment StartX=-74.51 StartY=36.4 StartZ=0 EndX=-74.51 EndY=30.8 EndZ=0
    g2: LineSegment StartX=-74.51 StartY=30.8 StartZ=0 EndX=-82.51 EndY=30.8 EndZ=0
    g3: LineSegment StartX=-82.51 StartY=30.8 StartZ=0 EndX=-82.51 EndY=36.4 EndZ=0
  constraints (11):
    c: Coincident(g1,g0)
    c: Vertical(g1)
    c: Coincident(g2,g1)
    c: Horizontal(g2)
    c: Coincident(g3,g2)
    c: Coincident(g3,g0)
    c: Vertical(g3)
    c: Tangent(g0,g-3)
    c: Tangent(g2,g-4)
    c: Tangent(g3,g-4)
    c: Tangent(g1,g-4)
FEATURE [Part::Extrusion] Extrude042  label="Extrude scavo per cavo usb per micro"
  Base = -> Sketch039
  Dir = (0,-1,2e-16)
  DirMode = 2
  FaceMakerClass = Part::FaceMakerBullseye
  FaceMakerMode = 3
  LengthFwd = 11.2
  LengthRev = 0
  Solid = true
  Symmetric = true
FEATURE [Sketcher::SketchObject] Sketch040  label="scavo saldature alimentatore connettore 5v"
  ArcFitTolerance = 1e-06
  AttachmentSupport = -> [XZ_Plane]
  ExternalGeometry = -> [Sketch037]
  FullyConstrained = true
  MakeInternals = false
  MapMode = 5
  Placement = pos=(0,0,0) rot=(1,0,0;1.5708rad)
  sketch-geometry (4):
    g0: LineSegment StartX=-211.175 StartY=-52.4316 StartZ=0 EndX=-211.175 EndY=-56.4316 EndZ=0
    g1: LineSegment StartX=-211.175 StartY=-52.4316 StartZ=0 EndX=-209.575 EndY=-52.4316 EndZ=0
    g2: LineSegment StartX=-209.575 StartY=-52.4316 StartZ=0 EndX=-209.575 EndY=-56.4316 EndZ=0
    g3: LineSegment StartX=-209.575 StartY=-56.4316 StartZ=0 EndX=-211.175 EndY=-56.4316 EndZ=0
  constraints (11):
    c: Vertical(g0)
    c: Coincident(g1,g0)
    c: Horizontal(g1)
    c: Coincident(g2,g1)
    c: Coincident(g3,g2)
    c: Coincident(g3,g0)
    c: Horizontal(g3)
    c: DistanceX(g1,g1) = 1.6
    c: DistanceY(g2,g2) = 4
    c: Tangent(g2,g-3)
    c: DistanceY(g1,g-3) = 2
FEATURE [Part::Extrusion] Extrude043  label="Extrude scavo saldature alimentatore connettore 5v"
  Base = -> Sketch040
  Dir = (0,-1,2e-16)
  DirMode = 2
  FaceMakerClass = Part::FaceMakerBullseye
  FaceMakerMode = 3
  LengthFwd = 8
  LengthRev = 0
  Solid = true
  Symmetric = true
FEATURE [Sketcher::SketchObject] Sketch041  label="scavo saldature alimentatore connettore 5v verticali"
  ArcFitTolerance = 1e-06
  AttachmentSupport = -> [XZ_Plane]
  ExternalGeometry = -> [Sketch037]
  FullyConstrained = true
  MakeInternals = false
  MapMode = 5
  Placement = pos=(0,0,0) rot=(1,0,0;1.5708rad)
  sketch-geometry (4):
    g0: LineSegment StartX=-211.175 StartY=-53.6316 StartZ=0 EndX=-209.575 EndY=-53.6316 EndZ=0
    g1: LineSegment StartX=-209.575 StartY=-53.6316 StartZ=0 EndX=-209.575 EndY=-76.6316 EndZ=0
    g2: LineSegment StartX=-209.575 StartY=-76.6316 StartZ=0 EndX=-211.175 EndY=-76.6316 EndZ=0
    g3: LineSegment StartX=-211.175 StartY=-76.6316 StartZ=0 EndX=-211.175 EndY=-53.6316 EndZ=0
  constraints (11):
    c: Horizontal(g0)
    c: Coincident(g1,g0)
    c: Coincident(g2,g1)
    c: Horizontal(g2)
    c: Coincident(g3,g2)
    c: Coincident(g3,g0)
    c: Vertical(g3)
    c: DistanceY(g3,g3) = 23
    c: DistanceX(g0,g0) = 1.6
    c: Tangent(g1,g-3)
    c: DistanceY(g0,g-3) = 3.2
FEATURE [Part::Extrusion] Extrude044  label="Extrude scavo saldature alimentatore connettore 5v verticali"
  Base = -> Sketch041
  Dir = (0,-1,2e-16)
  DirMode = 2
  FaceMakerClass = Part::FaceMakerBullseye
  FaceMakerMode = 3
  LengthFwd = 3.2
  LengthRev = 0
  Placement = pos=(0,8.3,0) rot=(0,0,1;0rad)
  Solid = true
  Symmetric = false
FEATURE [Sketcher::SketchObject] Sketch042  label="fermi per driver solenoide e alimentatore"
  ArcFitTolerance = 1e-06
  AttachmentSupport = -> [XZ_Plane]
  ExternalGeometry = -> [Sketch036,Sketch037,Sketch,Sketch038]
  FullyConstrained = true
  MakeInternals = false
  MapMode = 5
  Placement = pos=(0,0,0) rot=(1,0,0;1.5708rad)
  sketch-geometry (27):
    g0: LineSegment StartX=-199.238 StartY=-23.0627 StartZ=0 EndX=-200.168 EndY=-25.0566 EndZ=0
    g1: LineSegment StartX=-200.168 StartY=-25.0566 StartZ=0 EndX=-198.174 EndY=-25.9863 EndZ=0
    g2: LineSegment StartX=-198.174 StartY=-25.9863 StartZ=0 EndX=-197.244 EndY=-23.9925 EndZ=0
    g3: LineSegment StartX=-197.244 StartY=-23.9925 StartZ=0 EndX=-199.238 EndY=-23.0627 EndZ=0
    g4: LineSegment StartX=-200.012 StartY=-20.9364 StartZ=0 EndX=-202.294 EndY=-25.8305 EndZ=0
    g5: LineSegment StartX=-202.294 StartY=-25.8305 StartZ=0 EndX=-198.85 EndY=-27.4364 EndZ=0
    g6: LineSegment StartX=-196.724 StartY=-26.6625 StartZ=0 EndX=-195.794 EndY=-24.6687 EndZ=0
    g7: LineSegment StartX=-196.568 StartY=-22.5424 StartZ=0 EndX=-200.012 EndY=-20.9364 EndZ=0
    g8: LineSegment [constr] StartX=-197.4 StartY=-28.1126 StartZ=0 EndX=-196.724 EndY=-26.6625 EndZ=0
    g9: LineSegment [constr] StartX=-197.4 StartY=-28.1126 StartZ=0 EndX=-198.85 EndY=-27.4364 EndZ=0
    g10: ArcOfCircle CenterX=-197.244 CenterY=-23.9925 CenterZ=0 NormalX=0 NormalY=0 NormalZ=1 AngleXU=0 Radius=1.6 StartAngle=5.84685 EndAngle=7.41765
    g11: GeomPoint [constr] X=-195.118 Y=-23.2186 Z=0
    g12: ArcOfCircle CenterX=-198.174 CenterY=-25.9863 CenterZ=0 NormalX=0 NormalY=0 NormalZ=1 AngleXU=0 Radius=1.6 StartAngle=4.27606 EndAngle=5.84685
    g13: GeomPoint [constr] X=-197.4 Y=-28.1126 Z=0
    g14: LineSegment StartX=-207.775 StartY=-46.8316 StartZ=0 EndX=-207.775 EndY=-50.8316 EndZ=0
    g15: LineSegment StartX=-207.775 StartY=-46.8316 StartZ=0 EndX=-203.775 EndY=-46.8316 EndZ=0
    g16: LineSegment StartX=-203.775 StartY=-46.8316 StartZ=0 EndX=-203.775 EndY=-50.8316 EndZ=0
    g17: LineSegment StartX=-207.775 StartY=-50.8316 StartZ=0 EndX=-203.775 EndY=-50.8316 EndZ=0
    g18: LineSegment StartX=-209.375 StartY=-52.4316 StartZ=0 EndX=-203.775 EndY=-52.4316 EndZ=0
    g19: LineSegment StartX=-202.175 StartY=-50.8316 StartZ=0 EndX=-202.175 EndY=-46.8316 EndZ=0
    g20: LineSegment StartX=-203.775 StartY=-45.2316 StartZ=0 EndX=-209.375 EndY=-45.2316 EndZ=0
    g21: LineSegment StartX=-209.375 StartY=-45.2316 StartZ=0 EndX=-209.375 EndY=-52.4316 EndZ=0
    g22: ArcOfCircle CenterX=-203.775 CenterY=-46.8316 CenterZ=0 NormalX=0 NormalY=0 NormalZ=1 AngleXU=0 Radius=1.6 StartAngle=1.8e-15 EndAngle=1.5708
    g23: GeomPoint [constr] X=-202.175 Y=-45.2316 Z=0
    g24: ArcOfCircle CenterX=-203.775 CenterY=-50.8316 CenterZ=0 NormalX=0 NormalY=0 NormalZ=1 AngleXU=0 Radius=1.6 StartAngle=4.71239 EndAngle=6.28319
    g25: GeomPoint [constr] X=-202.175 Y=-52.4316 Z=0
    g26: LineSegment [constr] StartX=-207.775 StartY=-50.4316 StartZ=0 EndX=-207.775 EndY=-50.8316 EndZ=0
  constraints (69):
    c: Coincident(g1,g0)
    c: Coincident(g2,g1)
    c: Coincident(g3,g2)
    c: Coincident(g3,g0)
    c: Parallel(g0,g2)
    c: Perpendicular(g3,g0)
    c: Perpendicular(g1,g0)
    c: Coincident(g5,g4)
    c: Coincident(g7,g4)
    c: Distance(g3) = 2.2
    c: Distance(g2) = 2.2
    c: Parallel(g6,g2)
    c: Parallel(g6,g4)
    c: Perpendicular(g5,g6)
    c: Perpendicular(g7,g6)
    c: Distance(g13,g11) = 5.4
    c: Distance(g5,g13) = 5.4
    c: Coincident(g9,g8)
    c: Distance(g8) = 1.6
    c: Distance(g9) = 1.6
    c: Perpendicular(g9,g8)
    c: Parallel(g8,g6)
    c: Coincident(g8,g13)
    c: Distance(g8,g1) = 1.6
    c: Distance(g9,g1) = 1.6
    c: Tangent(g0,g-5)
    c: Distance(g0,g-6) = 18
    c: PointOnObject(g11,g7)
    c: PointOnObject(g11,g6)
    c: Tangent(g7,g10) = -1.5708
    c: Tangent(g6,g10) = -1.5708
    c: PointOnObject(g13,g5)
    c: Tangent(g5,g12) = -1.5708
    c: Tangent(g6,g12) = -1.5708
    c: Equal(g10,g12)
    c: Coincident(g10,g2)
    c: Vertical(g14)
    c: Coincident(g15,g14)
    c: Horizontal(g15)
    c: Coincident(g16,g15)
    c: Vertical(g16)
    c: Coincident(g17,g14)
    c: Coincident(g17,g16)
    c: Horizontal(g17)
    c: Distance(g16) = 4
    c: Distance(g15) = 4
    c: Horizontal(g18)
    c: Vertical(g19)
    c: Horizontal(g20)
    c: Coincident(g21,g20)
    c: Coincident(g21,g18)
    c: Vertical(g21)
    c: Distance(g20,g23) = 7.2
    c: Distance(g25,g23) = 7.2
    c: DistanceY(g18,g14) = 1.6
    c: DistanceX(g18,g14) = 1.6
    c: PointOnObject(g23,g20)
    c: PointOnObject(g23,g19)
    c: Tangent(g20,g22) = -1.5708
    c: Tangent(g19,g22) = -1.5708
    c: PointOnObject(g25,g19)
    c: Tangent(g18,g24) = -1.5708
    c: Tangent(g19,g24) = -1.5708
    c: Equal(g22,g24)
    c: Coincident(g22,g15)
    c: Vertical(g26)
    c: Distance(g26) = 0.4
    c: Coincident(g26,g-4)
    c: Coincident(g14,g26)
FEATURE [Part::Extrusion] Extrude045  label="Extrude fermi per driver solenoide e alimentatore"
  Base = -> Sketch042
  Dir = (0,-1,2e-16)
  DirMode = 2
  FaceMakerClass = Part::FaceMakerBullseye
  FaceMakerMode = 3
  LengthFwd = 25.2
  LengthRev = 0
  Solid = true
  Symmetric = true
FEATURE [Sketcher::SketchObject] Sketch043  label="scavo pulizia fermo alimentatore"
  ArcFitTolerance = 1e-06
  AttachmentSupport = -> [XZ_Plane]
  ExternalGeometry = -> [Sketch042,Sketch036,Sketch037]
  FullyConstrained = true
  MakeInternals = false
  MapMode = 5
  Placement = pos=(0,0,0) rot=(1,0,0;1.5708rad)
  sketch-geometry (6):
    g0: LineSegment StartX=-209.375 StartY=-52.4316 StartZ=0 EndX=-209.375 EndY=-50.4316 EndZ=0
    g1: LineSegment StartX=-209.375 StartY=-50.4316 StartZ=0 EndX=-207.775 EndY=-50.4316 EndZ=0
    g2: LineSegment StartX=-207.775 StartY=-50.4316 StartZ=0 EndX=-207.775 EndY=-45.2316 EndZ=0
    g3: LineSegment StartX=-207.775 StartY=-45.2316 StartZ=0 EndX=-202.175 EndY=-45.2316 EndZ=0
    g4: LineSegment StartX=-202.175 StartY=-45.2316 StartZ=0 EndX=-202.175 EndY=-52.4316 EndZ=0
    g5: LineSegment StartX=-202.175 StartY=-52.4316 StartZ=0 EndX=-209.375 EndY=-52.4316 EndZ=0
  constraints (13):
    c: Vertical(g0)
    c: Coincident(g1,g0)
    c: Coincident(g2,g1)
    c: Coincident(g3,g2)
    c: Coincident(g4,g3)
    c: Coincident(g5,g4)
    c: Coincident(g5,g0)
    c: Horizontal(g5)
    c: Coincident(g0,g-6)
    c: Tangent(g1,g-8)
    c: Tangent(g2,g-4)
    c: Tangent(g3,g-7)
    c: Tangent(g4,g-3)
FEATURE [Part::Extrusion] Extrude046  label="Extrude scavo pulizia fermo alimentatore"
  Base = -> Sketch043
  Dir = (0,-1,2e-16)
  DirMode = 2
  FaceMakerClass = Part::FaceMakerBullseye
  FaceMakerMode = 3
  LengthFwd = 19.5
  LengthRev = 0
  Solid = true
  Symmetric = true
FEATURE [Sketcher::SketchObject] Sketch044  label="buchini per fissaggio oled"
  ArcFitTolerance = 1e-06
  AttachmentSupport = -> [YZ_Plane]
  ExternalGeometry = -> [Sketch]
  FullyConstrained = true
  MakeInternals = false
  MapMode = 5
  Placement = pos=(0,0,0) rot=(0.57735,0.57735,0.57735;2.0944rad)
  sketch-geometry (5):
    g0: LineSegment [constr] StartX=1.5e-14 StartY=67.3588 StartZ=0 EndX=0 EndY=64.3588 EndZ=0
    g1: LineSegment [constr] StartX=0 StartY=64.3588 StartZ=0 EndX=10.4 EndY=64.3588 EndZ=0
    g2: LineSegment [constr] StartX=0 StartY=64.3588 StartZ=0 EndX=-10.4 EndY=64.3588 EndZ=0
    g3: Circle CenterX=10.4 CenterY=64.3588 CenterZ=0 NormalX=0 NormalY=0 NormalZ=1 AngleXU=0 Radius=1.5
    g4: Circle CenterX=-10.4 CenterY=64.3588 CenterZ=0 NormalX=0 NormalY=0 NormalZ=1 AngleXU=0 Radius=1.5
  constraints (13):
    c: Distance(g0) = 3
    c: PointOnObject(g0,g-2)
    c: Coincident(g1,g0)
    c: Horizontal(g1)
    c: Coincident(g2,g0)
    c: Horizontal(g2)
    c: DistanceX(g1,g1) = 10.4
    c: Coincident(g3,g1)
    c: Diameter(g4) = 3
    c: Coincident(g4,g2)
    c: Coincident(g0,g-7)
    c: Equal(g1,g2)
    c: Equal(g4,g3)
FEATURE [Part::Extrusion] Extrude047  label="Extrude buchini per fissaggio oled"
  Base = -> Sketch044
  Dir = (1,0,0)
  DirMode = 2
  FaceMakerClass = Part::FaceMakerBullseye
  FaceMakerMode = 3
  LengthFwd = 10
  LengthRev = 0
  Placement = pos=(-186,0,0) rot=(0,0,1;0rad)
  Solid = true
  Symmetric = false
FEATURE [Sketcher::SketchObject] Sketch046  label="scavo 5x5 neopixel"
  ArcFitTolerance = 1e-06
  AttachmentSupport = -> [YZ_Plane002]
  FullyConstrained = true
  MakeInternals = false
  MapMode = 5
  Placement = pos=(0,0,0) rot=(0.57735,0.57735,0.57735;2.0944rad)
  sketch-geometry (4):
    g0: LineSegment StartX=-2.7 StartY=2.7 StartZ=0 EndX=2.7 EndY=2.7 EndZ=0
    g1: LineSegment StartX=2.7 StartY=2.7 StartZ=0 EndX=2.7 EndY=-2.7 EndZ=0
    g2: LineSegment StartX=2.7 StartY=-2.7 StartZ=0 EndX=-2.7 EndY=-2.7 EndZ=0
    g3: LineSegment StartX=-2.7 StartY=-2.7 StartZ=0 EndX=-2.7 EndY=2.7 EndZ=0
  constraints (11):
    c: Horizontal(g0)
    c: Coincident(g1,g0)
    c: Vertical(g1)
    c: Coincident(g2,g1)
    c: Horizontal(g2)
    c: Coincident(g3,g2)
    c: Coincident(g3,g0)
    c: Vertical(g3)
    c: DistanceX(g0,g0) = 5.4
    c: DistanceY(g1,g1) = 5.4
    c: Symmetric(g0,g1,g-1)
FEATURE [Sketcher::SketchObject] Sketch047  label="scavo 10x10 neopixel corpo"
  ArcFitTolerance = 1e-06
  AttachmentOffset = pos=(0,0,1) rot=(0,0,1;0rad)
  AttachmentSupport = -> [YZ_Plane002]
  FullyConstrained = true
  MakeInternals = false
  MapMode = 5
  Placement = pos=(1,0,0) rot=(0.57735,0.57735,0.57735;2.0944rad)
  sketch-geometry (4):
    g0: LineSegment StartX=-5 StartY=5.1 StartZ=0 EndX=5 EndY=5.1 EndZ=0
    g1: LineSegment StartX=5 StartY=5.1 StartZ=0 EndX=5 EndY=-5.1 EndZ=0
    g2: LineSegment StartX=5 StartY=-5.1 StartZ=0 EndX=-5 EndY=-5.1 EndZ=0
    g3: LineSegment StartX=-5 StartY=-5.1 StartZ=0 EndX=-5 EndY=5.1 EndZ=0
  constraints (11):
    c: Horizontal(g0)
    c: Coincident(g1,g0)
    c: Vertical(g1)
    c: Coincident(g2,g1)
    c: Horizontal(g2)
    c: Coincident(g3,g2)
    c: Coincident(g3,g0)
    c: Vertical(g3)
    c: DistanceX(g0,g0) = 10
    c: DistanceY(g1,g1) = 10.2
    c: Symmetric(g0,g2,g-1)
FEATURE [Sketcher::SketchObject] Sketch048  label="buco per perno blocco neopixel"
  ArcFitTolerance = 1e-06
  AttachmentSupport = -> [XZ_Plane002]
  FullyConstrained = true
  MakeInternals = false
  MapMode = 5
  Placement = pos=(0,0,0) rot=(1,0,0;1.5708rad)
  sketch-geometry (4):
    g0: LineSegment StartX=3 StartY=1.2 StartZ=0 EndX=3 EndY=-1.2 EndZ=0
    g1: LineSegment StartX=3 StartY=-1.2 StartZ=0 EndX=5.4 EndY=-1.2 EndZ=0
    g2: LineSegment StartX=5.4 StartY=-1.2 StartZ=0 EndX=5.4 EndY=1.2 EndZ=0
    g3: LineSegment StartX=5.4 StartY=1.2 StartZ=0 EndX=3 EndY=1.2 EndZ=0
  constraints (11):
    c: Coincident(g1,g0)
    c: Horizontal(g1)
    c: Coincident(g2,g1)
    c: Vertical(g2)
    c: Coincident(g3,g2)
    c: Coincident(g3,g0)
    c: Horizontal(g3)
    c: DistanceX(g1,g1) = 2.4
    c: DistanceY(g2,g2) = 2.4
    c: Symmetric(g0,g0,g-1)
    c: DistanceX(g-1,g0) = 3
FEATURE [Sketcher::SketchObject] Sketch045  label="blocco principale per neopixel"
  ArcFitTolerance = 1e-06
  AttachmentSupport = -> [XZ_Plane002]
  ExternalGeometry = -> [Sketch048]
  FullyConstrained = true
  MakeInternals = false
  MapMode = 5
  Placement = pos=(0,0,0) rot=(1,0,0;1.5708rad)
  sketch-geometry (6):
    g0: LineSegment StartX=0 StartY=5.1 StartZ=0 EndX=0 EndY=-5.1 EndZ=0
    g1: LineSegment StartX=0 StartY=-5.1 StartZ=0 EndX=3 EndY=-5.1 EndZ=0
    g2: LineSegment StartX=7 StartY=-1.1 StartZ=0 EndX=7 EndY=5.1 EndZ=0
    g3: LineSegment StartX=7 StartY=5.1 StartZ=0 EndX=0 EndY=5.1 EndZ=0
    g4: ArcOfCircle CenterX=3 CenterY=-1.1 CenterZ=0 NormalX=0 NormalY=0 NormalZ=1 AngleXU=0 Radius=4 StartAngle=4.71239 EndAngle=6.28319
    g5: GeomPoint [constr] X=7 Y=-5.1 Z=0
  constraints (15):
    c: Vertical(g0)
    c: Coincident(g1,g0)
    c: Horizontal(g1)
    c: Vertical(g2)
    c: Coincident(g3,g2)
    c: Coincident(g3,g0)
    c: Horizontal(g3)
    c: DistanceY(g0,g0) = 10.2
    c: Symmetric(g0,g0,g-1)
    c: DistanceX(g3,g3) = 7
    c: PointOnObject(g5,g2)
    c: PointOnObject(g5,g1)
    c: Tangent(g2,g4) = -1.5708
    c: Tangent(g1,g4) = -1.5708
    c: DistanceX(g-3,g1) = 0
FEATURE [Sketcher::SketchObject] Sketch049  label="rinforzi esterni per corpo neopoixel"
  ArcFitTolerance = 1e-06
  AttachmentSupport = -> [XZ_Plane002]
  ExternalGeometry = -> [Sketch045]
  FullyConstrained = true
  MakeInternals = false
  MapMode = 5
  Placement = pos=(0,0,0) rot=(1,0,0;1.5708rad)
  sketch-geometry (8):
    g0: LineSegment StartX=1 StartY=-4.1 StartZ=0 EndX=2 EndY=-4.1 EndZ=0
    g1: LineSegment StartX=2 StartY=-4.1 StartZ=0 EndX=2 EndY=-5.1 EndZ=0
    g2: LineSegment StartX=2 StartY=-5.1 StartZ=0 EndX=1 EndY=-5.1 EndZ=0
    g3: LineSegment StartX=1 StartY=-5.1 StartZ=0 EndX=1 EndY=-4.1 EndZ=0
    g4: LineSegment StartX=1 StartY=5.1 StartZ=0 EndX=2 EndY=5.1 EndZ=0
    g5: LineSegment StartX=2 StartY=5.1 StartZ=0 EndX=2 EndY=4.1 EndZ=0
    g6: LineSegment StartX=2 StartY=4.1 StartZ=0 EndX=1 EndY=4.1 EndZ=0
    g7: LineSegment StartX=1 StartY=4.1 StartZ=0 EndX=1 EndY=5.1 EndZ=0
  constraints (24):
    c: Horizontal(g0)
    c: Coincident(g1,g0)
    c: Vertical(g1)
    c: Coincident(g2,g1)
    c: Horizontal(g2)
    c: Coincident(g3,g2)
    c: Coincident(g3,g0)
    c: Vertical(g3)
    c: Horizontal(g4)
    c: Coincident(g5,g4)
    c: Vertical(g5)
    c: Coincident(g6,g5)
    c: Horizontal(g6)
    c: Coincident(g7,g6)
    c: Coincident(g7,g4)
    c: Vertical(g7)
    c: DistanceX(g4,g4) = 1
    c: DistanceY(g5,g5) = 1
    c: DistanceX(g0,g0) = 1
    c: DistanceY(g1,g1) = 1
    c: DistanceX(g-3,g4) = 1
    c: DistanceY(g-3,g4) = 0
    c: DistanceX(g-4,g2) = 1
    c: DistanceY(g2,g-4) = 0
FEATURE [Sketcher::SketchObject] Sketch052  label="scavo saldature driver solenoide"
  ArcFitTolerance = 1e-06
  AttachmentSupport = -> [XZ_Plane]
  ExternalGeometry = -> [Sketch038]
  FullyConstrained = true
  MakeInternals = false
  MapMode = 5
  Placement = pos=(0,0,0) rot=(1,0,0;1.5708rad)
  sketch-geometry (4):
    g0: LineSegment StartX=-193.348 StartY=-2.85912 StartZ=0 EndX=-195.038 EndY=-6.48435 EndZ=0
    g1: LineSegment StartX=-195.038 StartY=-6.48435 StartZ=0 EndX=-193.588 EndY=-7.16054 EndZ=0
    g2: LineSegment StartX=-193.588 StartY=-7.16054 StartZ=0 EndX=-191.898 EndY=-3.53531 EndZ=0
    g3: LineSegment StartX=-191.898 StartY=-3.53531 StartZ=0 EndX=-193.348 EndY=-2.85912 EndZ=0
  constraints (11):
    c: Coincident(g1,g0)
    c: Coincident(g2,g1)
    c: Coincident(g3,g2)
    c: Coincident(g3,g0)
    c: Parallel(g2,g0)
    c: Perpendicular(g2,g3)
    c: Perpendicular(g1,g2,g1) = 1.5708
    c: Parallel(g2,g-3)
    c: Distance(g2) = 4
    c: Distance(g3) = 1.6
    c: Coincident(g2,g-3)
FEATURE [Part::Extrusion] Extrude055  label="Extrude scavo saldature driver solenoide"
  Base = -> Sketch052
  Dir = (0,-1,2e-16)
  DirMode = 2
  FaceMakerClass = Part::FaceMakerBullseye
  FaceMakerMode = 3
  LengthFwd = 6
  LengthRev = 0
  Solid = true
  Symmetric = true
FEATURE [Sketcher::SketchObject] Sketch053  label="scavo saldature rumble"
  ArcFitTolerance = 1e-06
  AttachmentSupport = -> [XZ_Plane]
  ExternalGeometry = -> [Sketch019]
  FullyConstrained = true
  MakeInternals = false
  MapMode = 5
  Placement = pos=(0,0,0) rot=(1,0,0;1.5708rad)
  sketch-geometry (4):
    g0: LineSegment StartX=-165.001 StartY=-43.1663 StartZ=0 EndX=-166.238 EndY=-46.9705 EndZ=0
    g1: LineSegment StartX=-166.238 StartY=-46.9705 StartZ=0 EndX=-165.096 EndY=-47.3413 EndZ=0
    g2: LineSegment StartX=-165.096 StartY=-47.3413 StartZ=0 EndX=-163.86 EndY=-43.5371 EndZ=0
    g3: LineSegment StartX=-163.86 StartY=-43.5371 StartZ=0 EndX=-165.001 EndY=-43.1663 EndZ=0
  constraints (11):
    c: Coincident(g1,g0)
    c: Coincident(g2,g1)
    c: Coincident(g3,g2)
    c: Coincident(g3,g0)
    c: Parallel(g0,g2)
    c: Perpendicular(g3,g0)
    c: Perpendicular(g1,g0)
    c: Parallel(g0,g-3)
    c: Distance(g0) = 4
    c: Distance(g1) = 1.2
    c: Coincident(g0,g-3)
FEATURE [Part::Extrusion] Extrude056  label="Extrude scavo saldature rumble"
  Base = -> Sketch053
  Dir = (0,-1,2e-16)
  DirMode = 2
  FaceMakerClass = Part::FaceMakerBullseye
  FaceMakerMode = 3
  LengthFwd = 8.4
  LengthRev = 0
  Solid = true
  Symmetric = true
FEATURE [Sketcher::SketchObject] Sketch054  label="scavo saldature alimentatore connettore USB"
  ArcFitTolerance = 1e-06
  AttachmentSupport = -> [XZ_Plane]
  ExternalGeometry = -> [Sketch037]
  FullyConstrained = true
  MakeInternals = false
  MapMode = 5
  Placement = pos=(0,0,0) rot=(1,0,0;1.5708rad)
  sketch-geometry (4):
    g0: LineSegment StartX=-209.575 StartY=-80.4316 StartZ=0 EndX=-210.375 EndY=-80.4316 EndZ=0
    g1: LineSegment StartX=-210.375 StartY=-80.4316 StartZ=0 EndX=-210.375 EndY=-72.4316 EndZ=0
    g2: LineSegment StartX=-210.375 StartY=-72.4316 StartZ=0 EndX=-209.575 EndY=-72.4316 EndZ=0
    g3: LineSegment StartX=-209.575 StartY=-72.4316 StartZ=0 EndX=-209.575 EndY=-80.4316 EndZ=0
  constraints (11):
    c: Horizontal(g0)
    c: Coincident(g1,g0)
    c: Vertical(g1)
    c: Coincident(g2,g1)
    c: Horizontal(g2)
    c: Coincident(g3,g2)
    c: Coincident(g3,g0)
    c: Vertical(g3)
    c: DistanceX(g0,g0) = 0.8
    c: DistanceY(g3,g3) = 8
    c: Coincident(g0,g-4)
FEATURE [Part::Extrusion] Extrude057  label="Extrude scavo saldature alimentatore connettore USB"
  Base = -> Sketch054
  Dir = (0,-1,2e-16)
  DirMode = 2
  FaceMakerClass = Part::FaceMakerBullseye
  FaceMakerMode = 3
  LengthFwd = 11
  LengthRev = 0
  Solid = true
  Symmetric = true
FEATURE [Sketcher::SketchObject] Sketch055  label="buco interno per micro switch"
  ArcFitTolerance = 1e-06
  AttachmentSupport = -> [XZ_Plane]
  ExternalGeometry = -> [Sketch]
  FullyConstrained = true
  MakeInternals = false
  MapMode = 5
  Placement = pos=(0,0,0) rot=(1,0,0;1.5708rad)
  sketch-geometry (11):
    g0: LineSegment [constr] StartX=-194.483 StartY=34.2854 StartZ=0 EndX=-196.022 EndY=30.0568 EndZ=0
    g1: LineSegment [constr] StartX=-196.022 StartY=30.0568 StartZ=0 EndX=-197.561 EndY=25.8282 EndZ=0
    g2: LineSegment [constr] StartX=-196.022 StartY=30.0568 StartZ=0 EndX=-194.143 EndY=29.3727 EndZ=0
    g3: LineSegment [constr] StartX=-196.022 StartY=30.0568 StartZ=0 EndX=-197.902 EndY=30.7408 EndZ=0
    g4: LineSegment StartX=-196.362 StartY=34.9694 StartZ=0 EndX=-192.604 EndY=33.6014 EndZ=0
    g5: LineSegment StartX=-199.441 StartY=26.5122 StartZ=0 EndX=-195.682 EndY=25.1441 EndZ=0
    g6: LineSegment StartX=-192.604 StartY=33.6014 StartZ=0 EndX=-195.682 EndY=25.1441 EndZ=0
    g7: LineSegment StartX=-196.362 StartY=34.9694 StartZ=0 EndX=-199.441 EndY=26.5122 EndZ=0
    g8: GeomPoint [constr] X=-187.821 Y=29.2 Z=0
    g9: LineSegment [constr] StartX=-188.505 StartY=27.3206 StartZ=0 EndX=-196.022 EndY=30.0568 EndZ=0
    g10: LineSegment [constr] StartX=-187.821 StartY=29.2 StartZ=0 EndX=-188.505 EndY=27.3206 EndZ=0
  constraints (27):
    c: Coincident(g2,g0)
    c: Parallel(g0,g-3)
    c: Tangent(g1,g0) = -1.5708
    c: Perpendicular(g0,g2)
    c: Tangent(g2,g3)
    c: Distance(g0,g1) = 9
    c: Equal(g0,g1)
    c: Distance(g3,g2) = 4
    c: Equal(g2,g3)
    c: Parallel(g3,g4)
    c: Symmetric(g4,g4,g0)
    c: Parallel(g6,g1)
    c: Parallel(g7,g1)
    c: Symmetric(g6,g6,g2)
    c: Symmetric(g5,g5,g1)
    c: Symmetric(g7,g7,g3)
    c: Coincident(g7,g4)
    c: Coincident(g6,g4)
    c: Coincident(g5,g6)
    c: Symmetric(g-3,g-3,g8)
    c: Perpendicular(g-3,g9)
    c: Distance(g9) = 8
    c: Coincident(g3,g9)
    c: Coincident(g10,g8)
    c: Parallel(g10,g-3)
    c: Distance(g10) = 2
    c: Coincident(g10,g9)
FEATURE [Sketcher::SketchObject] Sketch056  label="buco esterno per micro switch"
  ArcFitTolerance = 1e-06
  AttachmentSupport = -> [XZ_Plane]
  ExternalGeometry = -> [Sketch055]
  FullyConstrained = true
  MakeInternals = false
  MapMode = 5
  Placement = pos=(0,0,0) rot=(1,0,0;1.5708rad)
  sketch-geometry (17):
    g0: GeomPoint [constr] X=-194.143 Y=29.3727 Z=0
    g1: GeomPoint [constr] X=-194.483 Y=34.2854 Z=0
    g2: GeomPoint [constr] X=-197.902 Y=30.7408 Z=0
    g3: GeomPoint [constr] X=-197.561 Y=25.8282 Z=0
    g4: GeomPoint [constr] X=-196.022 Y=30.0568 Z=0
    g5: LineSegment [constr] StartX=-194.483 StartY=34.2854 StartZ=0 EndX=-196.022 EndY=30.0568 EndZ=0
    g6: LineSegment [constr] StartX=-196.022 StartY=30.0568 StartZ=0 EndX=-197.561 EndY=25.8282 EndZ=0
    g7: LineSegment [constr] StartX=-197.902 StartY=30.7408 StartZ=0 EndX=-196.022 EndY=30.0568 EndZ=0
    g8: LineSegment [constr] StartX=-196.022 StartY=30.0568 StartZ=0 EndX=-194.143 EndY=29.3727 EndZ=0
    g9: LineSegment [constr] StartX=-195.338 StartY=31.9362 StartZ=0 EndX=-196.022 EndY=30.0568 EndZ=0
    g10: LineSegment [constr] StartX=-196.022 StartY=30.0568 StartZ=0 EndX=-196.706 EndY=28.1774 EndZ=0
    g11: LineSegment [constr] StartX=-196.022 StartY=30.0568 StartZ=0 EndX=-196.821 EndY=30.3475 EndZ=0
    g12: LineSegment [constr] StartX=-196.022 StartY=30.0568 StartZ=0 EndX=-195.223 EndY=29.7661 EndZ=0
    g13: LineSegment StartX=-194.539 StartY=31.6454 StartZ=0 EndX=-195.907 EndY=27.8867 EndZ=0
    g14: LineSegment StartX=-196.137 StartY=32.2269 StartZ=0 EndX=-197.505 EndY=28.4681 EndZ=0
    g15: LineSegment StartX=-196.137 StartY=32.2269 StartZ=0 EndX=-194.539 EndY=31.6454 EndZ=0
    g16: LineSegment StartX=-197.505 StartY=28.4681 StartZ=0 EndX=-195.907 EndY=27.8867 EndZ=0
  constraints (34):
    c: Symmetric(g-5,g-5,g1)
    c: Symmetric(g-5,g-6,g0)
    c: Symmetric(g-6,g-6,g3)
    c: Symmetric(g-5,g-6,g2)
    c: Coincident(g5,g1)
    c: Coincident(g5,g4)
    c: Coincident(g6,g4)
    c: Coincident(g6,g3)
    c: Equal(g5,g6)
    c: Coincident(g7,g2)
    c: Coincident(g7,g4)
    c: Coincident(g8,g4)
    c: Coincident(g8,g0)
    c: Equal(g7,g8)
    c: Coincident(g11,g9)
    c: Coincident(g12,g9)
    c: Tangent(g10,g9) = -1.5708
    c: Perpendicular(g11,g9)
    c: Parallel(g9,g-4)
    c: Equal(g9,g10)
    c: Parallel(g12,g11)
    c: Equal(g11,g12)
    c: Distance(g11,g12) = 1.7
    c: Distance(g9,g10) = 4
    c: Symmetric(g13,g13,g12)
    c: Parallel(g13,g9)
    c: Symmetric(g14,g14,g11)
    c: Symmetric(g15,g15,g9)
    c: Parallel(g15,g11)
    c: Symmetric(g16,g16,g10)
    c: Coincident(g16,g14)
    c: Coincident(g15,g14)
    c: Coincident(g13,g15)
    c: Coincident(g9,g4)
FEATURE [Sketcher::SketchObject] Sketch057  label="buco interno per SWITCH"
  ArcFitTolerance = 1e-06
  AttachmentSupport = -> [XZ_Plane]
  ExternalGeometry = -> [Sketch]
  FullyConstrained = true
  MakeInternals = false
  MapMode = 5
  Placement = pos=(0,0,0) rot=(1,0,0;1.5708rad)
  sketch-geometry (10):
    g0: GeomPoint [constr] X=-187.821 Y=29.2 Z=0
    g1: LineSegment [constr] StartX=-188.505 StartY=27.3206 StartZ=0 EndX=-193.203 EndY=29.0307 EndZ=0
    g2: LineSegment [constr] StartX=-190.809 StartY=35.6086 StartZ=0 EndX=-195.597 EndY=22.4529 EndZ=0
    g3: GeomPoint [constr] X=-193.203 Y=29.0307 Z=0
    g4: LineSegment [constr] StartX=-196.492 StartY=30.2278 StartZ=0 EndX=-189.914 EndY=27.8336 EndZ=0
    g5: LineSegment StartX=-194.098 StartY=36.8056 StartZ=0 EndX=-187.52 EndY=34.4115 EndZ=0
    g6: LineSegment StartX=-194.098 StartY=36.8056 StartZ=0 EndX=-198.886 EndY=23.6499 EndZ=0
    g7: LineSegment StartX=-187.52 StartY=34.4115 StartZ=0 EndX=-192.308 EndY=21.2558 EndZ=0
    g8: LineSegment StartX=-198.886 StartY=23.6499 StartZ=0 EndX=-192.308 EndY=21.2558 EndZ=0
    g9: LineSegment [constr] StartX=-187.821 StartY=29.2 StartZ=0 EndX=-188.505 EndY=27.3206 EndZ=0
  constraints (23):
    c: Symmetric(g-3,g-3,g0)
    c: Perpendicular(g1,g-3)
    c: Parallel(g2,g-3)
    c: Symmetric(g2,g2,g3)
    c: Perpendicular(g2,g4)
    c: Symmetric(g4,g4,g3)
    c: Distance(g2) = 14
    c: Distance(g4) = 7
    c: Distance(g1) = 5
    c: Parallel(g5,g4)
    c: Parallel(g7,g2)
    c: Symmetric(g5,g5,g2)
    c: Symmetric(g6,g6,g4)
    c: Symmetric(g7,g7,g4)
    c: Symmetric(g8,g8,g2)
    c: Coincident(g6,g5)
    c: Coincident(g7,g5)
    c: Coincident(g8,g7)
    c: Coincident(g3,g1)
    c: Coincident(g9,g0)
    c: Parallel(g9,g-3)
    c: Distance(g9) = 2
    c: Coincident(g1,g9)
FEATURE [Sketcher::SketchObject] Sketch058  label="buco esterno per SWITCH"
  ArcFitTolerance = 1e-06
  AttachmentSupport = -> [XZ_Plane]
  ExternalGeometry = -> [Sketch057]
  FullyConstrained = true
  MakeInternals = false
  MapMode = 5
  Placement = pos=(0,0,0) rot=(1,0,0;1.5708rad)
  sketch-geometry (12):
    g0: GeomPoint [constr] X=-190.809 Y=35.6086 Z=0
    g1: GeomPoint [constr] X=-196.492 Y=30.2278 Z=0
    g2: GeomPoint [constr] X=-189.914 Y=27.8336 Z=0
    g3: GeomPoint [constr] X=-195.597 Y=22.4529 Z=0
    g4: GeomPoint [constr] X=-193.203 Y=29.0307 Z=0
    g5: LineSegment [constr] StartX=-192.006 StartY=32.3196 StartZ=0 EndX=-194.4 EndY=25.7418 EndZ=0
    g6: GeomPoint [constr] X=-193.203 Y=29.0307 Z=0
    g7: LineSegment [constr] StartX=-195.082 StartY=29.7148 StartZ=0 EndX=-191.324 EndY=28.3467 EndZ=0
    g8: LineSegment StartX=-193.885 StartY=33.0037 StartZ=0 EndX=-190.127 EndY=31.6356 EndZ=0
    g9: LineSegment StartX=-190.127 StartY=31.6356 StartZ=0 EndX=-192.521 EndY=25.0578 EndZ=0
    g10: LineSegment StartX=-196.28 StartY=26.4258 StartZ=0 EndX=-192.521 EndY=25.0578 EndZ=0
    g11: LineSegment StartX=-193.885 StartY=33.0037 StartZ=0 EndX=-196.28 EndY=26.4258 EndZ=0
  constraints (21):
    c: Symmetric(g-6,g-6,g3)
    c: Symmetric(g-4,g-6,g2)
    c: Symmetric(g-5,g-4,g0)
    c: Symmetric(g-5,g-6,g1)
    c: Symmetric(g1,g2,g4)
    c: Parallel(g5,g-4)
    c: Symmetric(g5,g5,g6)
    c: Perpendicular(g7,g5)
    c: Symmetric(g7,g7,g6)
    c: Distance(g5) = 7
    c: Distance(g7) = 4
    c: Parallel(g8,g7)
    c: Parallel(g11,g5)
    c: Symmetric(g8,g8,g5)
    c: Symmetric(g9,g9,g7)
    c: Symmetric(g10,g10,g5)
    c: Symmetric(g11,g11,g7)
    c: Coincident(g11,g8)
    c: Coincident(g9,g8)
    c: Coincident(g9,g10)
    c: Coincident(g6,g4)
FEATURE [Part::Extrusion] Extrude060  label="Extrude buco interno per SWITCH destro"
  Base = -> Sketch057
  Dir = (0,-1,2e-16)
  DirMode = 2
  FaceMakerClass = Part::FaceMakerBullseye
  FaceMakerMode = 3
  LengthFwd = 13.2
  LengthRev = 0
  Placement = pos=(0,2.6,0) rot=(0,0,1;0rad)
  Solid = true
  Symmetric = false
FEATURE [Part::Extrusion] Extrude061  label="Extrude buco esterno per SWITCH destro"
  Base = -> Sketch058
  Dir = (0,-1,2e-16)
  DirMode = 2
  FaceMakerClass = Part::FaceMakerBullseye
  FaceMakerMode = 3
  LengthFwd = 2
  LengthRev = 0
  Placement = pos=(0,-10.6,0) rot=(0,0,1;0rad)
  Solid = true
  Symmetric = false
FEATURE [Sketcher::SketchObject] Sketch059  label="buco per spazio introduzione SWITCH"
  ArcFitTolerance = 1e-06
  AttachmentSupport = -> [XZ_Plane]
  ExternalGeometry = -> [Sketch057,Sketch010]
  FullyConstrained = true
  MakeInternals = false
  MapMode = 5
  Placement = pos=(0,0,0) rot=(1,0,0;1.5708rad)
  sketch-geometry (8):
    g0: LineSegment [constr] StartX=-201.368 StartY=36.3521 StartZ=0 EndX=-195.094 EndY=34.0687 EndZ=0
    g1: LineSegment [constr] StartX=-194.098 StartY=36.8056 StartZ=0 EndX=-195.094 EndY=34.0687 EndZ=0
    g2: LineSegment StartX=-198.658 StartY=24.2771 StartZ=0 EndX=-199.654 EndY=21.5401 EndZ=0
    g3: LineSegment StartX=-199.654 StartY=21.5401 StartZ=0 EndX=-181.196 EndY=14.822 EndZ=0
    g4: LineSegment StartX=-181.196 StartY=14.822 StartZ=0 EndX=-180.2 EndY=17.559 EndZ=0
    g5: LineSegment StartX=-180.2 StartY=17.559 StartZ=0 EndX=-198.658 EndY=24.2771 EndZ=0
    g6: LineSegment [constr] StartX=-204.932 StartY=26.5605 StartZ=0 EndX=-198.658 EndY=24.2771 EndZ=0
    g7: LineSegment [constr] StartX=-198.658 StartY=24.2771 StartZ=0 EndX=-199.654 EndY=21.5401 EndZ=0
  constraints (20):
    c: Parallel(g1,g-3)
    c: Parallel(g0,g-4)
    c: Coincident(g0,g-4)
    c: Coincident(g1,g-3)
    c: Coincident(g0,g1)
    c: Coincident(g3,g2)
    c: Coincident(g4,g3)
    c: Coincident(g5,g4)
    c: Coincident(g5,g2)
    c: Parallel(g5,g-5)
    c: Parallel(g3,g-5)
    c: Parallel(g4,g-6)
    c: DistanceX(g-6,g4) = 0
    c: Coincident(g6,g-5)
    c: Equal(g6,g0)
    c: Coincident(g7,g6)
    c: Equal(g7,g1)
    c: Tangent(g7,g-3)
    c: Coincident(g2,g6)
    c: Coincident(g2,g7)
FEATURE [Part::Extrusion] Extrude062  label="Extrude buco per spazio introduzione SWITCH"
  Base = -> Sketch059
  Dir = (0,-1,2e-16)
  DirMode = 2
  FaceMakerClass = Part::FaceMakerBullseye
  FaceMakerMode = 3
  LengthFwd = 13.2
  LengthRev = 0
  Solid = true
  Symmetric = true
FEATURE [Part::Extrusion] Extrude063  label="Extrude buco interno per SWITCH sinistro"
  Base = -> Sketch057
  Dir = (0,-1,2e-16)
  DirMode = 2
  FaceMakerClass = Part::FaceMakerBullseye
  FaceMakerMode = 3
  LengthFwd = 13.2
  LengthRev = 0
  Placement = pos=(0,10.6,0) rot=(0,0,1;0rad)
  Solid = true
  Symmetric = false
FEATURE [Part::Extrusion] Extrude064  label="Extrude buco esterno per SWITCH sinistro"
  Base = -> Sketch058
  Dir = (0,-1,2e-16)
  DirMode = 2
  FaceMakerClass = Part::FaceMakerBullseye
  FaceMakerMode = 3
  LengthFwd = 2
  LengthRev = 0
  Placement = pos=(0,12.6,0) rot=(0,0,1;0rad)
  Solid = true
  Symmetric = false
FEATURE [Sketcher::SketchObject] Sketch061  label="struttura esterna blocco switch"
  ArcFitTolerance = 1e-06
  AttachmentSupport = -> [XZ_Plane003]
  FullyConstrained = true
  MakeInternals = false
  MapMode = 5
  Placement = pos=(0,0,0) rot=(1,0,0;1.5708rad)
  sketch-geometry (5):
    g0: LineSegment StartX=-1 StartY=-5.1 StartZ=0 EndX=1 EndY=-5.1 EndZ=0
    g1: LineSegment StartX=1 StartY=-5.1 StartZ=0 EndX=1 EndY=5.1 EndZ=0
    g2: LineSegment StartX=1 StartY=5.1 StartZ=0 EndX=-1 EndY=5.1 EndZ=0
    g3: LineSegment StartX=-1 StartY=5.1 StartZ=0 EndX=-1 EndY=-5.1 EndZ=0
    g4: GeomPoint [constr] X=0 Y=0 Z=0
  constraints (12):
    c: Coincident(g0,g1)
    c: Coincident(g1,g2)
    c: Coincident(g2,g3)
    c: Coincident(g3,g0)
    c: Horizontal(g0)
    c: Horizontal(g2)
    c: Vertical(g1)
    c: Vertical(g3)
    c: Symmetric(g2,g0,g4)
    c: Distance(g1,g3) = 2
    c: Distance(g0,g2) = 10.2
    c: Coincident(g4,g-1)
FEATURE [Sketcher::SketchObject] Sketch062  label="struttura interna blocco switch"
  ArcFitTolerance = 1e-06
  AttachmentSupport = -> [XZ_Plane003]
  ExternalGeometry = -> [Sketch061]
  FullyConstrained = true
  MakeInternals = false
  MapMode = 5
  Placement = pos=(0,0,0) rot=(1,0,0;1.5708rad)
  sketch-geometry (5):
    g0: LineSegment StartX=-1 StartY=3.1 StartZ=0 EndX=-1 EndY=-3.1 EndZ=0
    g1: LineSegment StartX=-1 StartY=-3.1 StartZ=0 EndX=1 EndY=-3.1 EndZ=0
    g2: LineSegment StartX=1 StartY=-3.1 StartZ=0 EndX=1 EndY=3.1 EndZ=0
    g3: LineSegment StartX=1 StartY=3.1 StartZ=0 EndX=-1 EndY=3.1 EndZ=0
    g4: GeomPoint [constr] X=0 Y=0 Z=0
  constraints (12):
    c: Coincident(g0,g1)
    c: Coincident(g1,g2)
    c: Coincident(g2,g3)
    c: Coincident(g3,g0)
    c: Vertical(g0)
    c: Vertical(g2)
    c: Horizontal(g1)
    c: Horizontal(g3)
    c: Symmetric(g2,g0,g4)
    c: Coincident(g4,g-1)
    c: Distance(g0) = 6.2
    c: Equal(g3,g-3)
FEATURE [Sketcher::SketchObject] Sketch063  label="blocchi tra switch"
  ArcFitTolerance = 1e-06
  AttachmentSupport = -> [XZ_Plane003]
  ExternalGeometry = -> [Sketch061,Sketch062]
  FullyConstrained = true
  MakeInternals = false
  MapMode = 5
  Placement = pos=(0,0,0) rot=(1,0,0;1.5708rad)
  sketch-geometry (8):
    g0: LineSegment StartX=-3 StartY=5.1 StartZ=0 EndX=-1 EndY=5.1 EndZ=0
    g1: LineSegment StartX=-1 StartY=5.1 StartZ=0 EndX=-1 EndY=3.1 EndZ=0
    g2: LineSegment StartX=-1 StartY=3.1 StartZ=0 EndX=-3 EndY=3.1 EndZ=0
    g3: LineSegment StartX=-3 StartY=3.1 StartZ=0 EndX=-3 EndY=5.1 EndZ=0
    g4: LineSegment StartX=-3 StartY=-3.1 StartZ=0 EndX=-1 EndY=-3.1 EndZ=0
    g5: LineSegment StartX=-1 StartY=-3.1 StartZ=0 EndX=-1 EndY=-5.1 EndZ=0
    g6: LineSegment StartX=-1 StartY=-5.1 StartZ=0 EndX=-3 EndY=-5.1 EndZ=0
    g7: LineSegment StartX=-3 StartY=-5.1 StartZ=0 EndX=-3 EndY=-3.1 EndZ=0
  constraints (20):
    c: Horizontal(g0)
    c: Coincident(g1,g0)
    c: Coincident(g2,g1)
    c: Horizontal(g2)
    c: Coincident(g3,g2)
    c: Coincident(g3,g0)
    c: Vertical(g3)
    c: Horizontal(g4)
    c: Coincident(g5,g4)
    c: Coincident(g6,g5)
    c: Horizontal(g6)
    c: Coincident(g7,g6)
    c: Coincident(g7,g4)
    c: Vertical(g7)
    c: Coincident(g0,g-4)
    c: Coincident(g1,g-5)
    c: Coincident(g4,g-6)
    c: Coincident(g5,g-7)
    c: Distance(g0) = 2
    c: Distance(g4) = 2
FEATURE [Sketcher::SketchObject] Sketch066  label="piano per rampino"
  ArcFitTolerance = 1e-06
  AttachmentSupport = -> [XZ_Plane002]
  ExternalGeometry = -> [Sketch045]
  FullyConstrained = true
  MakeInternals = false
  MapMode = 5
  Placement = pos=(0,0,0) rot=(1,0,0;1.5708rad)
  sketch-geometry (4):
    g0: LineSegment StartX=5.4 StartY=5.1 StartZ=0 EndX=5.4 EndY=3.9 EndZ=0
    g1: LineSegment StartX=5.4 StartY=3.9 StartZ=0 EndX=7 EndY=3.9 EndZ=0
    g2: LineSegment StartX=7 StartY=3.9 StartZ=0 EndX=7 EndY=5.1 EndZ=0
    g3: LineSegment StartX=7 StartY=5.1 StartZ=0 EndX=5.4 EndY=5.1 EndZ=0
  constraints (11):
    c: Coincident(g0,g1)
    c: Coincident(g1,g2)
    c: Coincident(g2,g3)
    c: Coincident(g3,g0)
    c: Vertical(g0)
    c: Vertical(g2)
    c: Horizontal(g1)
    c: Horizontal(g3)
    c: Distance(g0,g2) = 1.6
    c: Distance(g1,g3) = 1.2
    c: Coincident(g2,g-3)
FEATURE [Sketcher::SketchObject] Sketch064  label="rampini_per_serraggio_struttura"
  ArcFitTolerance = 1e-06
  AttachmentSupport = -> [XZ_Plane002]
  ExternalGeometry = -> [Sketch066,Sketch045]
  FullyConstrained = true
  MakeInternals = false
  MapMode = 5
  Placement = pos=(0,0,0) rot=(1,0,0;1.5708rad)
  sketch-geometry (7):
    g0: LineSegment StartX=7 StartY=5.1 StartZ=0 EndX=7 EndY=3.9 EndZ=0
    g1: LineSegment StartX=7 StartY=3.9 StartZ=0 EndX=9 EndY=3.9 EndZ=0
    g2: LineSegment StartX=7 StartY=5.1 StartZ=0 EndX=7 EndY=5.1 EndZ=0
    g3: LineSegment StartX=7 StartY=5.1 StartZ=0 EndX=7 EndY=7.5 EndZ=0
    g4: LineSegment StartX=9 StartY=5.1 StartZ=0 EndX=9 EndY=3.9 EndZ=0
    g5: LineSegment StartX=7 StartY=7.5 StartZ=0 EndX=9 EndY=7.5 EndZ=0
    g6: LineSegment StartX=9 StartY=7.5 StartZ=0 EndX=9 EndY=5.1 EndZ=0
  constraints (20):
    c: Vertical(g0)
    c: Coincident(g1,g0)
    c: Horizontal(g1)
    c: Coincident(g2,g0)
    c: Horizontal(g2)
    c: Coincident(g3,g2)
    c: Vertical(g3)
    c: Coincident(g5,g3)
    c: Coincident(g4,g6)
    c: Coincident(g4,g1)
    c: Vertical(g4)
    c: Coincident(g0,g-3)
    c: DistanceY(g-4,g3) = 2.4
    c: DistanceX(g1,g1) = 2
    c: DistanceY(g2,g6) = 0
    c: DistanceX(g2,g2) = 0
    c: DistanceY(g0,g0) = 1.2
    c: Coincident(g5,g6)
    c: Horizontal(g5)
    c: Vertical(g6)
FEATURE [Sketcher::SketchObject] Sketch067  label="perno per blocco switch"
  ArcFitTolerance = 1e-06
  AttachmentSupport = -> [XZ_Plane]
  ExternalGeometry = -> [Sketch,Sketch010]
  FullyConstrained = true
  MakeInternals = false
  MapMode = 5
  Placement = pos=(0,0,0) rot=(1,0,0;1.5708rad)
  sketch-geometry (14):
    g0: LineSegment StartX=-191.073 StartY=24.9429 StartZ=0 EndX=-185.81 EndY=23.0276 EndZ=0
    g1: LineSegment StartX=-183.76 StartY=23.9839 StartZ=0 EndX=-182.392 EndY=27.7427 EndZ=0
    g2: LineSegment StartX=-183.348 StartY=29.7934 StartZ=0 EndX=-188.61 EndY=31.7087 EndZ=0
    g3: LineSegment StartX=-188.61 StartY=31.7087 StartZ=0 EndX=-191.073 EndY=24.9429 EndZ=0
    g4: GeomPoint [constr] X=-186.459 Y=27.0946 Z=0
    g5: LineSegment StartX=-189.022 StartY=25.8992 StartZ=0 EndX=-185.263 EndY=24.5311 EndZ=0
    g6: LineSegment StartX=-185.263 StartY=24.5311 StartZ=0 EndX=-183.895 EndY=28.2899 EndZ=0
    g7: LineSegment StartX=-183.895 StartY=28.2899 StartZ=0 EndX=-187.654 EndY=29.658 EndZ=0
    g8: LineSegment StartX=-187.654 StartY=29.658 StartZ=0 EndX=-189.022 EndY=25.8992 EndZ=0
    g9: GeomPoint [constr] X=-186.459 Y=27.0946 Z=0
    g10: ArcOfCircle CenterX=-185.263 CenterY=24.5311 CenterZ=0 NormalX=0 NormalY=0 NormalZ=1 AngleXU=0 Radius=1.6 StartAngle=4.36332 EndAngle=5.93412
    g11: GeomPoint [constr] X=-184.307 Y=22.4804 Z=0
    g12: ArcOfCircle CenterX=-183.895 CenterY=28.2899 CenterZ=0 NormalX=0 NormalY=0 NormalZ=1 AngleXU=0 Radius=1.6 StartAngle=5.93412 EndAngle=7.50492
    g13: GeomPoint [constr] X=-181.844 Y=29.2462 Z=0
  constraints (30):
    c: Coincident(g2,g3)
    c: Coincident(g3,g0)
    c: Symmetric(g13,g0,g4)
    c: Distance(g11,g3) = 7.2
    c: Distance(g0,g2) = 7.2
    c: Parallel(g3,g1)
    c: Parallel(g2,g0)
    c: Perpendicular(g2,g3)
    c: Coincident(g5,g6)
    c: Coincident(g6,g7)
    c: Coincident(g7,g8)
    c: Coincident(g8,g5)
    c: Symmetric(g7,g5,g9)
    c: Distance(g6,g8) = 4
    c: Distance(g5,g7) = 4
    c: Coincident(g9,g4)
    c: Parallel(g8,g6)
    c: Parallel(g7,g5)
    c: Perpendicular(g7,g8)
    c: Tangent(g8,g-3)
    c: Tangent(g2,g-4)
    c: PointOnObject(g11,g1)
    c: PointOnObject(g11,g0)
    c: Tangent(g1,g10) = -1.5708
    c: Tangent(g0,g10) = -1.5708
    c: PointOnObject(g13,g1)
    c: Tangent(g1,g12) = -1.5708
    c: Tangent(g2,g12) = -1.5708
    c: Equal(g10,g12)
    c: Coincident(g10,g5)
FEATURE [Part::Extrusion] Extrude072  label="Extrude perno per blocco switch"
  Base = -> Sketch067
  Dir = (0,-1,2e-16)
  DirMode = 2
  FaceMakerClass = Part::FaceMakerBullseye
  FaceMakerMode = 3
  LengthFwd = 25.2
  LengthRev = 0
  Solid = true
  Symmetric = true
FEATURE [Part::MultiFuse] Fusion
  Refine = true
  Shapes = -> [Extrude,Sweep,Extrude007,Extrude011,Extrude005,Extrude012,Extrude013,Extrude016,Extrude031,Extrude039,Extrude045,Extrude072]
FEATURE [Part::Cut] Cut
  Base = -> Fusion
  Refine = true
  Tool = -> Extrude001
FEATURE [Part::Cut] Cut001
  Base = -> Cut
  Refine = true
  Tool = -> Extrude004
FEATURE [Part::Cut] Cut002
  Base = -> Cut001
  Refine = true
  Tool = -> Extrude006
FEATURE [Part::Cut] Cut003
  Base = -> Cut002
  Refine = true
  Tool = -> Extrude008
FEATURE [Part::Cut] Cut004
  Base = -> Cut003
  Refine = true
  Tool = -> Extrude009
FEATURE [Part::Cut] Cut005
  Base = -> Cut004
  Refine = true
  Tool = -> Extrude010
FEATURE [Part::Cut] Cut006
  Base = -> Cut005
  Refine = true
  Tool = -> Extrude014
FEATURE [Part::Cut] Cut007
  Base = -> Cut006
  Refine = true
  Tool = -> Extrude015
FEATURE [Part::Cut] Cut008
  Base = -> Cut007
  Refine = true
  Tool = -> Extrude018
FEATURE [Part::Cut] Cut009
  Base = -> Cut008
  Refine = true
  Tool = -> Extrude019
FEATURE [Part::Cut] Cut010
  Base = -> Cut009
  Refine = true
  Tool = -> Extrude020
FEATURE [Part::Cut] Cut011
  Base = -> Cut010
  Refine = true
  Tool = -> Extrude021
FEATURE [Part::Cut] Cut012
  Base = -> Cut011
  Refine = true
  Tool = -> Extrude022
FEATURE [Part::Cut] Cut013
  Base = -> Cut012
  Refine = true
  Tool = -> Extrude023
FEATURE [Part::Cut] Cut014
  Base = -> Cut013
  Refine = true
  Tool = -> Extrude032
FEATURE [Part::Cut] Cut015
  Base = -> Cut014
  Refine = true
  Tool = -> Extrude033
FEATURE [Part::Cut] Cut016
  Base = -> Cut015
  Refine = true
  Tool = -> Extrude034
FEATURE [Part::Cut] Cut017
  Base = -> Cut016
  Refine = true
  Tool = -> Extrude035
FEATURE [Part::Cut] Cut018
  Base = -> Cut017
  Refine = true
  Tool = -> Extrude036
FEATURE [Part::Cut] Cut019
  Base = -> Cut018
  Refine = true
  Tool = -> Extrude037
FEATURE [Part::Cut] Cut020
  Base = -> Cut019
  Refine = true
  Tool = -> Extrude030
FEATURE [Part::Cut] Cut022
  Base = -> Cut020
  Refine = true
  Tool = -> Extrude038
FEATURE [Part::Cut] Cut023
  Base = -> Cut022
  Refine = true
  Tool = -> Extrude041
FEATURE [Part::Cut] Cut024
  Base = -> Cut023
  Refine = true
  Tool = -> Extrude040
FEATURE [Part::Cut] Cut025
  Base = -> Cut024
  Refine = true
  Tool = -> Extrude042
FEATURE [Part::Cut] Cut026
  Base = -> Cut025
  Refine = true
  Tool = -> Extrude043
FEATURE [Part::Cut] Cut027
  Base = -> Cut026
  Refine = true
  Tool = -> Extrude044
FEATURE [Part::Cut] Cut028
  Base = -> Cut027
  Refine = true
  Tool = -> Extrude046
FEATURE [Part::Cut] Cut029
  Base = -> Cut028
  Refine = true
  Tool = -> Extrude047
FEATURE [Part::Cut] Cut033
  Base = -> Cut029
  Refine = true
  Tool = -> Extrude055
FEATURE [Part::Cut] Cut034
  Base = -> Cut033
  Refine = true
  Tool = -> Extrude056
FEATURE [Part::Cut] Cut035
  Base = -> Cut034
  Refine = true
  Tool = -> Extrude057
FEATURE [Part::Cut] Cut037
  Base = -> Cut035
  Refine = true
  Tool = -> Extrude060
FEATURE [Part::Cut] Cut038
  Base = -> Cut037
  Refine = true
  Tool = -> Extrude061
FEATURE [Part::Cut] Cut039
  Base = -> Cut038
  Refine = true
  Tool = -> Extrude063
FEATURE [Part::Cut] Cut040
  Base = -> Cut039
  Refine = true
  Tool = -> Extrude064
FEATURE [Part::Cut] Cut041
  Base = -> Cut040
  Refine = true
  Tool = -> Extrude062
FEATURE [Sketcher::SketchObject] Sketch068  label="base con smusso sopra neopixel"
  ArcFitTolerance = 1e-06
  AttachmentSupport = -> [YZ_Plane002]
  FullyConstrained = true
  MakeInternals = false
  MapMode = 5
  Placement = pos=(0,0,0) rot=(0.57735,0.57735,0.57735;2.0944rad)
  sketch-geometry (5):
    g0: LineSegment StartX=-9.5 StartY=-6.1 StartZ=0 EndX=9.5 EndY=-6.1 EndZ=0
    g1: LineSegment StartX=9.5 StartY=-6.1 StartZ=0 EndX=9.5 EndY=6.1 EndZ=0
    g2: LineSegment StartX=9.5 StartY=6.1 StartZ=0 EndX=-9.5 EndY=6.1 EndZ=0
    g3: LineSegment StartX=-9.5 StartY=6.1 StartZ=0 EndX=-9.5 EndY=-6.1 EndZ=0
    g4: GeomPoint [constr] X=0 Y=0 Z=0
  constraints (12):
    c: Coincident(g0,g1)
    c: Coincident(g1,g2)
    c: Coincident(g2,g3)
    c: Coincident(g3,g0)
    c: Horizontal(g0)
    c: Horizontal(g2)
    c: Vertical(g1)
    c: Vertical(g3)
    c: Symmetric(g2,g0,g4)
    c: Distance(g1,g3) = 19
    c: Distance(g0,g2) = 12.2
    c: Coincident(g4,g-1)
FEATURE [Sketcher::SketchObject] Sketch069  label="cilindro minore"
  ArcFitTolerance = 1e-06
  AttachmentSupport = -> [XZ_Plane004]
  FullyConstrained = true
  MakeInternals = false
  MapMode = 5
  Placement = pos=(0,0,0) rot=(1,0,0;1.5708rad)
  sketch-geometry (1):
    g0: Circle CenterX=0 CenterY=0 CenterZ=0 NormalX=0 NormalY=0 NormalZ=1 AngleXU=0 Radius=5.8
  constraints (2):
    c: Diameter(g0) = 11.6
    c: Coincident(g0,g-1)
FEATURE [Sketcher::SketchObject] Sketch070  label="cilindro maggiore"
  ArcFitTolerance = 1e-06
  AttachmentSupport = -> [XZ_Plane004]
  ExternalGeometry = -> [Sketch069]
  FullyConstrained = true
  MakeInternals = false
  MapMode = 5
  Placement = pos=(0,0,0) rot=(1,0,0;1.5708rad)
  sketch-geometry (1):
    g0: Circle CenterX=0 CenterY=0 CenterZ=0 NormalX=0 NormalY=0 NormalZ=1 AngleXU=0 Radius=6.5
  constraints (2):
    c: Coincident(g0,g-1)
    c: Diameter(g0) = 13
FEATURE [Sketcher::SketchObject] Sketch071  label="buco interno"
  ArcFitTolerance = 1e-06
  AttachmentSupport = -> [XZ_Plane004]
  ExternalGeometry = -> [Sketch069]
  FullyConstrained = true
  MakeInternals = false
  MapMode = 5
  Placement = pos=(0,0,0) rot=(1,0,0;1.5708rad)
  sketch-geometry (1):
    g0: Circle CenterX=0 CenterY=0 CenterZ=0 NormalX=0 NormalY=0 NormalZ=1 AngleXU=0 Radius=5
  constraints (2):
    c: Coincident(g0,g-1)
    c: Diameter(g0) = 10
FEATURE [PartDesign::Pad] Pad
  Direction = (0,-1,2e-16)
  Length = 1.2
  Length2 = 10
  Placement = pos=(0,0,0) rot=(1,0,0;1.5708rad)
  Profile = -> Sketch070
  ReferenceAxis = -> Sketch070 [N_Axis]
  Refine = true
  Suppressed = false
  Type = 0
FEATURE [PartDesign::Pad] Pad001
  BaseFeature = -> Pad
  Direction = (0,-1,2e-16)
  Length = 5.6
  Length2 = 10
  Placement = pos=(0,0,0) rot=(1,0,0;1.5708rad)
  Profile = -> Sketch069
  ReferenceAxis = -> Sketch069 [N_Axis]
  Refine = true
  Suppressed = false
  Type = 0
FEATURE [PartDesign::Pocket] Pocket
  BaseFeature = -> Pad001
  Direction = (0,1,-2e-16)
  Length = 7
  Length2 = 5
  Midplane = true
  Placement = pos=(0,0,0) rot=(1,0,0;1.5708rad)
  Profile = -> Sketch071
  ReferenceAxis = -> Sketch071 [N_Axis]
  Refine = true
  Suppressed = false
  Type = 0
FEATURE [PartDesign::Fillet] Fillet
  Base = -> Pocket [Face7]
  BaseFeature = -> Pocket
  Placement = pos=(0,0,0) rot=(1,0,0;1.5708rad)
  Radius = 1
  Refine = true
  SupportTransform = false
  Suppressed = false
  UseAllEdges = false
FEATURE [PartDesign::Body] Body004  label="pulsanti lato sinistro"
  AllowCompound = false
  Group = -> [Sketch069,Sketch070,Sketch071,Pad,Pad001,Pocket,Fillet]
  Origin = -> Origin004
  Tip = -> Fillet
FEATURE [Sketcher::SketchObject] Sketch072  label="buco per saldature e diodo driver solenoide"
  ArcFitTolerance = 1e-06
  AttachmentSupport = -> [XZ_Plane]
  ExternalGeometry = -> [Sketch038]
  FullyConstrained = true
  MakeInternals = false
  MapMode = 5
  Placement = pos=(0,0,0) rot=(1,0,0;1.5708rad)
  sketch-geometry (4):
    g0: LineSegment StartX=-209.225 StartY=-40.6939 StartZ=0 EndX=-204.154 EndY=-29.8182 EndZ=0
    g1: LineSegment StartX=-204.154 StartY=-29.8182 StartZ=0 EndX=-206.51 EndY=-28.7194 EndZ=0
    g2: LineSegment StartX=-206.51 StartY=-28.7194 StartZ=0 EndX=-211.582 EndY=-39.5951 EndZ=0
    g3: LineSegment StartX=-211.582 StartY=-39.5951 StartZ=0 EndX=-209.225 EndY=-40.6939 EndZ=0
  constraints (11):
    c: Coincident(g1,g0)
    c: Coincident(g2,g1)
    c: Coincident(g3,g2)
    c: Coincident(g3,g0)
    c: Parallel(g-3,g0)
    c: Parallel(g0,g2)
    c: Perpendicular(g0,g3)
    c: Perpendicular(g1,g0)
    c: Distance(g3) = 2.6
    c: Distance(g2) = 12
    c: Coincident(g0,g-3)
FEATURE [Part::Extrusion] Extrude074  label="Extrude buco per saldature e diodo driver solenoide"
  Base = -> Sketch072
  Dir = (0,-1,2e-16)
  DirMode = 2
  FaceMakerClass = Part::FaceMakerBullseye
  FaceMakerMode = 3
  LengthFwd = 14.6
  LengthRev = 0
  Solid = true
  Symmetric = true
FEATURE [Part::Cut] Cut042
  Base = -> Cut041
  Refine = true
  Tool = -> Extrude074
FEATURE [Sketcher::SketchObject] Sketch073  label="fori slargati blocco solenoide"
  ArcFitTolerance = 1e-06
  AttachmentSupport = -> [XY_Plane]
  ExternalGeometry = -> [Sketch030]
  FullyConstrained = true
  MakeInternals = false
  MapMode = 5
  sketch-geometry (2):
    g0: Circle CenterX=-152.209 CenterY=6.95 CenterZ=0 NormalX=0 NormalY=0 NormalZ=1 AngleXU=0 Radius=3.7
    g1: Circle CenterX=-130.41 CenterY=-6.95 CenterZ=0 NormalX=0 NormalY=0 NormalZ=1 AngleXU=0 Radius=3.7
  constraints (4):
    c: Diameter(g0) = 7.4
    c: Coincident(g0,g-3)
    c: Diameter(g1) = 7.4
    c: Coincident(g1,g-4)
FEATURE [Part::Extrusion] Extrude075  label="Extrude fori slargati blocco solenoide"
  Base = -> Sketch073
  Dir = (0,0,1)
  DirMode = 2
  FaceMakerClass = Part::FaceMakerBullseye
  FaceMakerMode = 3
  LengthFwd = 1.5
  LengthRev = 0
  Placement = pos=(0,0,36.4) rot=(0,0,1;0rad)
  Solid = true
  Symmetric = false
FEATURE [Part::Cut] Cut043
  Base = -> Cut042
  Refine = true
  Tool = -> Extrude075
FEATURE [Sketcher::SketchObject] Sketch074  label="lato sx pistola"
  ArcFitTolerance = 1e-06
  AttachmentSupport = -> [XZ_Plane]
  ExternalGeometry = -> [Sketch016,Sketch,Sketch058]
  FullyConstrained = true
  MakeInternals = false
  MapMode = 5
  Placement = pos=(0,0,0) rot=(1,0,0;1.5708rad)
  sketch-geometry (37):
    g0: LineSegment StartX=-82.8 StartY=3.2 StartZ=0 EndX=0 EndY=3.2 EndZ=0
    g1: LineSegment StartX=-82.8 StartY=3.2 StartZ=0 EndX=-82.8 EndY=6.2 EndZ=0
    g2: LineSegment [constr] StartX=-107.6 StartY=18 StartZ=0 EndX=-107.6 EndY=20 EndZ=0
    g3: LineSegment [constr] StartX=-132.428 StartY=18 StartZ=0 EndX=-132.428 EndY=20 EndZ=0
    g4: LineSegment StartX=-132.428 StartY=20 StartZ=0 EndX=-107.6 EndY=20 EndZ=0
    g5: ArcOfCircle CenterX=-107.6 CenterY=4 CenterZ=0 NormalX=0 NormalY=0 NormalZ=1 AngleXU=0 Radius=16 StartAngle=0.137937 EndAngle=1.5708
    g6: LineSegment StartX=-82.8 StartY=6.2 StartZ=0 EndX=-91.752 EndY=6.2 EndZ=0
    g7: LineSegment [constr] StartX=-145.743 StartY=8.32624 StartZ=0 EndX=-147.645 EndY=8.94427 EndZ=0
    g8: ArcOfCircle CenterX=-132.428 CenterY=4 CenterZ=0 NormalX=0 NormalY=0 NormalZ=1 AngleXU=0 Radius=16 StartAngle=1.5708 EndAngle=2.82743
    g9: LineSegment StartX=-215.932 StartY=-80.4316 StartZ=0 EndX=-176.685 EndY=-80.4316 EndZ=0
    g10: LineSegment StartX=-147.645 StartY=8.94427 StartZ=0 EndX=-176.685 EndY=-80.4316 EndZ=0
    g11: LineSegment [constr] StartX=-193.988 StartY=-2.33927 StartZ=0 EndX=-192.176 EndY=-3.18451 EndZ=0
    g12: LineSegment [constr] StartX=-217.232 StartY=-52.1862 StartZ=0 EndX=-215.42 EndY=-53.0314 EndZ=0
    g13: LineSegment StartX=-192.176 StartY=-3.18451 StartZ=0 EndX=-215.42 EndY=-53.0314 EndZ=0
    g14: ArcOfCircle CenterX=-184.801 CenterY=-67.3089 CenterZ=0 NormalX=0 NormalY=0 NormalZ=1 AngleXU=0 Radius=33.7833 StartAngle=2.70526 EndAngle=3.54053
    g15: ArcOfCircle CenterX=-207.583 CenterY=4 CenterZ=0 NormalX=0 NormalY=0 NormalZ=1 AngleXU=0 Radius=17 StartAngle=5.84685 EndAngle=7.56663
    g16: LineSegment StartX=-202.765 StartY=20.303 StartZ=0 EndX=-195.887 EndY=39.2 EndZ=0
    g17: LineSegment [constr] StartX=-193.885 StartY=33.0037 StartZ=0 EndX=-197.644 EndY=34.3718 EndZ=0
    g18: LineSegment StartX=-195.887 StartY=39.2 StartZ=0 EndX=0 EndY=39.2 EndZ=0
    g19: LineSegment StartX=0 StartY=3.2 StartZ=0 EndX=0 EndY=39.2 EndZ=0
    g20: LineSegment StartX=-189.939 StartY=31.5672 StartZ=0 EndX=-192.333 EndY=24.9893 EndZ=0
    g21: LineSegment StartX=-196.467 StartY=26.4942 StartZ=0 EndX=-194.073 EndY=33.0721 EndZ=0
    g22: Circle CenterX=-213.443 CenterY=-76.8316 CenterZ=0 NormalX=0 NormalY=0 NormalZ=1 AngleXU=0 Radius=1.8
    g23: Circle CenterX=-179.305 CenterY=-76.8316 CenterZ=0 NormalX=0 NormalY=0 NormalZ=1 AngleXU=0 Radius=1.8
    g24: Circle CenterX=-184.08 CenterY=34.8 CenterZ=0 NormalX=0 NormalY=0 NormalZ=1 AngleXU=0 Radius=1.8
    g25: Circle CenterX=-78.51 CenterY=34.8 CenterZ=0 NormalX=0 NormalY=0 NormalZ=1 AngleXU=0 Radius=1.8
    g26: Circle CenterX=-78.51 CenterY=7.6 CenterZ=0 NormalX=0 NormalY=0 NormalZ=1 AngleXU=0 Radius=1.8
    g27: Circle CenterX=-5.6 CenterY=34.8 CenterZ=0 NormalX=0 NormalY=0 NormalZ=1 AngleXU=0 Radius=1.8
    g28: Circle CenterX=-5.6 CenterY=7.6 CenterZ=0 NormalX=0 NormalY=0 NormalZ=1 AngleXU=0 Radius=1.8
    g29: LineSegment StartX=-190.127 StartY=31.6356 StartZ=0 EndX=-189.939 EndY=31.5672 EndZ=0
    g30: LineSegment StartX=-194.073 StartY=33.0721 StartZ=0 EndX=-193.885 EndY=33.0037 EndZ=0
    g31: LineSegment StartX=-193.885 StartY=33.0037 StartZ=0 EndX=-190.127 EndY=31.6356 EndZ=0
    g32: LineSegment StartX=-196.467 StartY=26.4942 StartZ=0 EndX=-192.333 EndY=24.9893 EndZ=0
    g33: Circle CenterX=-19 CenterY=21.2 CenterZ=0 NormalX=0 NormalY=0 NormalZ=1 AngleXU=0 Radius=6.3
    g34: Circle CenterX=-42 CenterY=21.2 CenterZ=0 NormalX=0 NormalY=0 NormalZ=1 AngleXU=0 Radius=6.3
    g35: Circle CenterX=-65 CenterY=21.2 CenterZ=0 NormalX=0 NormalY=0 NormalZ=1 AngleXU=0 Radius=6.3
    g36: LineSegment [constr] StartX=-4 StartY=21.2 StartZ=0 EndX=-65 EndY=21.2 EndZ=0
  constraints (96):
    c: Coincident(g0,g-41)
    c: Horizontal(g0)
    c: PointOnObject(g0,g-39)
    c: Coincident(g1,g0)
    c: Vertical(g1)
    c: DistanceY(g1,g1) = 3
    c: Coincident(g2,g-17)
    c: Vertical(g2)
    c: Coincident(g3,g-16)
    c: Vertical(g3)
    c: DistanceY(g2,g2) = 2
    c: DistanceY(g3,g3) = 2
    c: Coincident(g4,g3)
    c: Coincident(g4,g2)
    c: Coincident(g5,g-17)
    c: Coincident(g5,g2)
    c: Coincident(g6,g1)
    c: Horizontal(g6)
    c: Coincident(g6,g5)
    c: Coincident(g7,g-15)
    c: Coincident(g8,g7)
    c: Coincident(g8,g3)
    c: Coincident(g8,g-15)
    c: Horizontal(g9)
    c: DistanceY(g-13,g9) = 2
    c: Coincident(g10,g7)
    c: Parallel(g10,g-14)
    c: Coincident(g9,g10)
    c: Distance(g11) = 2
    c: Coincident(g11,g-11)
    c: Perpendicular(g-11,g11)
    c: Distance(g12) = 2
    c: Coincident(g12,g-12)
    c: Perpendicular(g-11,g12)
    c: Coincident(g13,g11)
    c: Coincident(g13,g12)
    c: Coincident(g14,g-32)
    c: Coincident(g14,g12)
    c: Coincident(g14,g9)
    c: Coincident(g15,g-10)
    c: Coincident(g15,g11)
    c: Parallel(g16,g-22)
    c: Distance(g17) = 4
    c: PointOnObject(g17,g16)
    c: Coincident(g15,g16)
    c: Horizontal(g18)
    c: Coincident(g18,g16)
    c: Coincident(g19,g0)
    c: PointOnObject(g19,g-39)
    c: DistanceY(g19,g-36) = 2
    c: Coincident(g18,g19)
    c: Diameter(g22) = 3.6
    c: Coincident(g22,g-9)
    c: Diameter(g23) = 3.6
    c: Coincident(g23,g-8)
    c: Diameter(g24) = 3.6
    c: Diameter(g25) = 3.6
    c: Diameter(g26) = 3.6
    c: Diameter(g27) = 3.6
    c: Diameter(g28) = 3.6
    c: Coincident(g27,g-4)
    c: Coincident(g28,g-3)
    c: Coincident(g25,g-6)
    c: Coincident(g26,g-5)
    c: Coincident(g24,g-7)
    c: Parallel(g20,g-21)
    c: Equal(g20,g-21)
    c: Parallel(g21,g-19)
    c: Equal(g21,g-19)
    c: Distance(g29) = 0.2
    c: Distance(g30) = 0.2
    c: Parallel(g29,g-20)
    c: Parallel(g31,g-20)
    c: Equal(g31,g-20)
    c: Coincident(g30,g31)
    c: Coincident(g31,g29)
    c: Coincident(g29,g-21)
    c: Parallel(g30,g31)
    c: Coincident(g17,g30)
    c: Coincident(g20,g29)
    c: Coincident(g21,g30)
    c: Perpendicular(g16,g17)
    c: Coincident(g32,g21)
    c: Coincident(g32,g20)
    c: Perpendicular(g10,g7)
    c: Diameter(g33) = 12.6
    c: Diameter(g34) = 12.6
    c: Diameter(g35) = 12.6
    c: Horizontal(g36)
    c: PointOnObject(g33,g36)
    c: PointOnObject(g34,g36)
    c: DistanceX(g34,g33) = 23
    c: DistanceX(g35,g34) = 23
    c: DistanceX(g33,g36) = 15
    c: Symmetric(g-24,g-24,g36)
    c: Coincident(g36,g35)
FEATURE [Sketcher::SketchObject] Sketch075  label="lato dx pistola"
  ArcFitTolerance = 1e-06
  AttachmentSupport = -> [XZ_Plane]
  ExternalGeometry = -> [Sketch016,Sketch,Sketch058,Sketch074]
  FullyConstrained = true
  MakeInternals = false
  MapMode = 5
  Placement = pos=(0,0,0) rot=(1,0,0;1.5708rad)
  sketch-geometry (61):
    g0: LineSegment StartX=-82.8 StartY=3.2 StartZ=0 EndX=0 EndY=3.2 EndZ=0
    g1: LineSegment StartX=-82.8 StartY=3.2 StartZ=0 EndX=-82.8 EndY=6.2 EndZ=0
    g2: LineSegment [constr] StartX=-107.6 StartY=18 StartZ=0 EndX=-107.6 EndY=20 EndZ=0
    g3: LineSegment [constr] StartX=-132.428 StartY=18 StartZ=0 EndX=-132.428 EndY=20 EndZ=0
    g4: LineSegment StartX=-132.428 StartY=20 StartZ=0 EndX=-107.6 EndY=20 EndZ=0
    g5: ArcOfCircle CenterX=-107.6 CenterY=4 CenterZ=0 NormalX=0 NormalY=0 NormalZ=1 AngleXU=0 Radius=16 StartAngle=0.137937 EndAngle=1.5708
    g6: LineSegment StartX=-82.8 StartY=6.2 StartZ=0 EndX=-91.752 EndY=6.2 EndZ=0
    g7: LineSegment [constr] StartX=-145.743 StartY=8.32624 StartZ=0 EndX=-147.645 EndY=8.94427 EndZ=0
    g8: ArcOfCircle CenterX=-132.428 CenterY=4 CenterZ=0 NormalX=0 NormalY=0 NormalZ=1 AngleXU=0 Radius=16 StartAngle=1.5708 EndAngle=2.82743
    g9: LineSegment StartX=-215.932 StartY=-80.4316 StartZ=0 EndX=-176.685 EndY=-80.4316 EndZ=0
    g10: LineSegment StartX=-147.645 StartY=8.94427 StartZ=0 EndX=-176.685 EndY=-80.4316 EndZ=0
    g11: LineSegment [constr] StartX=-193.988 StartY=-2.33927 StartZ=0 EndX=-192.176 EndY=-3.18451 EndZ=0
    g12: LineSegment [constr] StartX=-217.232 StartY=-52.1862 StartZ=0 EndX=-215.42 EndY=-53.0314 EndZ=0
    g13: LineSegment StartX=-192.176 StartY=-3.18451 StartZ=0 EndX=-215.42 EndY=-53.0314 EndZ=0
    g14: ArcOfCircle CenterX=-184.801 CenterY=-67.3089 CenterZ=0 NormalX=0 NormalY=0 NormalZ=1 AngleXU=0 Radius=33.7833 StartAngle=2.70526 EndAngle=3.54053
    g15: ArcOfCircle CenterX=-207.583 CenterY=4 CenterZ=0 NormalX=0 NormalY=0 NormalZ=1 AngleXU=0 Radius=17 StartAngle=5.84685 EndAngle=7.56663
    g16: LineSegment StartX=-202.765 StartY=20.303 StartZ=0 EndX=-195.887 EndY=39.2 EndZ=0
    g17: LineSegment [constr] StartX=-193.885 StartY=33.0037 StartZ=0 EndX=-197.644 EndY=34.3718 EndZ=0
    g18: LineSegment StartX=-195.887 StartY=39.2 StartZ=0 EndX=0 EndY=39.2 EndZ=0
    g19: LineSegment StartX=0 StartY=3.2 StartZ=0 EndX=0 EndY=39.2 EndZ=0
    g20: LineSegment StartX=-189.939 StartY=31.5672 StartZ=0 EndX=-192.333 EndY=24.9893 EndZ=0
    g21: LineSegment StartX=-196.467 StartY=26.4942 StartZ=0 EndX=-194.073 EndY=33.0721 EndZ=0
    g22: Circle CenterX=-213.443 CenterY=-76.8316 CenterZ=0 NormalX=0 NormalY=0 NormalZ=1 AngleXU=0 Radius=1.8
    g23: Circle CenterX=-179.305 CenterY=-76.8316 CenterZ=0 NormalX=0 NormalY=0 NormalZ=1 AngleXU=0 Radius=1.8
    g24: Circle CenterX=-184.08 CenterY=34.8 CenterZ=0 NormalX=0 NormalY=0 NormalZ=1 AngleXU=0 Radius=1.8
    g25: Circle CenterX=-78.51 CenterY=34.8 CenterZ=0 NormalX=0 NormalY=0 NormalZ=1 AngleXU=0 Radius=1.8
    g26: Circle CenterX=-78.51 CenterY=7.6 CenterZ=0 NormalX=0 NormalY=0 NormalZ=1 AngleXU=0 Radius=1.8
    g27: Circle CenterX=-5.6 CenterY=34.8 CenterZ=0 NormalX=0 NormalY=0 NormalZ=1 AngleXU=0 Radius=1.8
    g28: Circle CenterX=-5.6 CenterY=7.6 CenterZ=0 NormalX=0 NormalY=0 NormalZ=1 AngleXU=0 Radius=1.8
    g29: LineSegment StartX=-190.127 StartY=31.6356 StartZ=0 EndX=-189.939 EndY=31.5672 EndZ=0
    g30: LineSegment StartX=-194.073 StartY=33.0721 StartZ=0 EndX=-193.885 EndY=33.0037 EndZ=0
    g31: LineSegment StartX=-193.885 StartY=33.0037 StartZ=0 EndX=-190.127 EndY=31.6356 EndZ=0
    g32: LineSegment StartX=-196.467 StartY=26.4942 StartZ=0 EndX=-192.333 EndY=24.9893 EndZ=0
    g33: LineSegment [constr] StartX=-4 StartY=21.2 StartZ=0 EndX=-87.91 EndY=21.2 EndZ=0
    g34: GeomPoint [constr] X=-4 Y=21.2 Z=0
    g35: LineSegment [constr] StartX=-15.2 StartY=33.7 StartZ=0 EndX=-15.2 EndY=8.7 EndZ=0
    g36: LineSegment [constr] StartX=-15.2 StartY=33.7 StartZ=0 EndX=-56.2 EndY=33.7 EndZ=0
    g37: LineSegment [constr] StartX=-15.2 StartY=8.7 StartZ=0 EndX=-56.2 EndY=8.7 EndZ=0
    g38: LineSegment [constr] StartX=-56.2 StartY=33.7 StartZ=0 EndX=-56.2 EndY=8.7 EndZ=0
    g39: Circle CenterX=-18.6 CenterY=30.3 CenterZ=0 NormalX=0 NormalY=0 NormalZ=1 AngleXU=0 Radius=3.4
    g40: Circle CenterX=-18.6 CenterY=12.1 CenterZ=0 NormalX=0 NormalY=0 NormalZ=1 AngleXU=0 Radius=3.4
    g41: Circle CenterX=-43.2 CenterY=30.3 CenterZ=0 NormalX=0 NormalY=0 NormalZ=1 AngleXU=0 Radius=3.4
    g42: Circle CenterX=-43.2 CenterY=12.1 CenterZ=0 NormalX=0 NormalY=0 NormalZ=1 AngleXU=0 Radius=3.4
    g43: LineSegment [constr] StartX=-4 StartY=21.2 StartZ=0 EndX=-15.2 EndY=21.2 EndZ=0
    g44: LineSegment [constr] StartX=-15.2 StartY=21.2 StartZ=0 EndX=-36.2 EndY=21.2 EndZ=0
    g45: LineSegment [constr] StartX=-41.5 StartY=16.2 StartZ=0 EndX=-30.9 EndY=16.2 EndZ=0
    g46: LineSegment [constr] StartX=-30.9 StartY=16.2 StartZ=0 EndX=-30.9 EndY=26.2 EndZ=0
    g47: LineSegment [constr] StartX=-30.9 StartY=26.2 StartZ=0 EndX=-41.5 EndY=26.2 EndZ=0
    g48: LineSegment [constr] StartX=-41.5 StartY=26.2 StartZ=0 EndX=-41.5 EndY=16.2 EndZ=0
    g49: GeomPoint [constr] X=-36.2 Y=21.2 Z=0
    g50: Circle CenterX=-36.2 CenterY=21.2 CenterZ=0 NormalX=0 NormalY=0 NormalZ=1 AngleXU=0 Radius=2.8
    g51: LineSegment [constr] StartX=-24.2 StartY=26.7 StartZ=0 EndX=-24.2 EndY=15.7 EndZ=0
    g52: Circle CenterX=-24.2 CenterY=26.7 CenterZ=0 NormalX=0 NormalY=0 NormalZ=1 AngleXU=0 Radius=3
    g53: Circle CenterX=-24.2 CenterY=15.7 CenterZ=0 NormalX=0 NormalY=0 NormalZ=1 AngleXU=0 Radius=3
    g54: GeomPoint X=-18.6 Y=30.3 Z=0
    g55: GeomPoint X=-18.6 Y=12.1 Z=0
    g56: GeomPoint X=-43.2 Y=12.1 Z=0
    g57: GeomPoint X=-43.2 Y=30.3 Z=0
    g58: Circle CenterX=-65 CenterY=21.2 CenterZ=0 NormalX=0 NormalY=0 NormalZ=1 AngleXU=0 Radius=1.5
    g59: Circle CenterX=-42 CenterY=21.2 CenterZ=0 NormalX=0 NormalY=0 NormalZ=1 AngleXU=0 Radius=1.5
    g60: Circle CenterX=-19 CenterY=21.2 CenterZ=0 NormalX=0 NormalY=0 NormalZ=1 AngleXU=0 Radius=1.5
  constraints (149):
    c: Coincident(g0,g-41)
    c: Horizontal(g0)
    c: PointOnObject(g0,g-39)
    c: Coincident(g1,g0)
    c: Vertical(g1)
    c: DistanceY(g1,g1) = 3
    c: Coincident(g2,g-17)
    c: Vertical(g2)
    c: Coincident(g3,g-16)
    c: Vertical(g3)
    c: DistanceY(g2,g2) = 2
    c: DistanceY(g3,g3) = 2
    c: Coincident(g4,g3)
    c: Coincident(g4,g2)
    c: Coincident(g5,g-17)
    c: Coincident(g5,g2)
    c: Coincident(g6,g1)
    c: Horizontal(g6)
    c: Coincident(g6,g5)
    c: Coincident(g7,g-15)
    c: Coincident(g8,g7)
    c: Coincident(g8,g3)
    c: Coincident(g8,g-15)
    c: Horizontal(g9)
    c: DistanceY(g-13,g9) = 2
    c: Coincident(g10,g7)
    c: Parallel(g10,g-14)
    c: Coincident(g9,g10)
    c: Distance(g11) = 2
    c: Coincident(g11,g-11)
    c: Perpendicular(g-11,g11)
    c: Distance(g12) = 2
    c: Coincident(g12,g-12)
    c: Perpendicular(g-11,g12)
    c: Coincident(g13,g11)
    c: Coincident(g13,g12)
    c: Coincident(g14,g-32)
    c: Coincident(g14,g12)
    c: Coincident(g14,g9)
    c: Coincident(g15,g-10)
    c: Coincident(g15,g11)
    c: Parallel(g16,g-22)
    c: Distance(g17) = 4
    c: PointOnObject(g17,g16)
    c: Coincident(g15,g16)
    c: Horizontal(g18)
    c: Coincident(g18,g16)
    c: Coincident(g19,g0)
    c: PointOnObject(g19,g-39)
    c: DistanceY(g19,g-36) = 2
    c: Coincident(g18,g19)
    c: Diameter(g22) = 3.6
    c: Coincident(g22,g-9)
    c: Diameter(g23) = 3.6
    c: Coincident(g23,g-8)
    c: Diameter(g24) = 3.6
    c: Diameter(g25) = 3.6
    c: Diameter(g26) = 3.6
    c: Diameter(g27) = 3.6
    c: Diameter(g28) = 3.6
    c: Coincident(g27,g-4)
    c: Coincident(g28,g-3)
    c: Coincident(g25,g-6)
    c: Coincident(g26,g-5)
    c: Coincident(g24,g-7)
    c: Parallel(g20,g-21)
    c: Equal(g20,g-21)
    c: Parallel(g21,g-19)
    c: Equal(g21,g-19)
    c: Distance(g29) = 0.2
    c: Distance(g30) = 0.2
    c: Parallel(g29,g-20)
    c: Parallel(g31,g-20)
    c: Equal(g31,g-20)
    c: Coincident(g30,g31)
    c: Coincident(g31,g29)
    c: Coincident(g29,g-21)
    c: Parallel(g30,g31)
    c: Coincident(g17,g30)
    c: Coincident(g20,g29)
    c: Coincident(g21,g30)
    c: Perpendicular(g16,g17)
    c: Coincident(g32,g21)
    c: Coincident(g32,g20)
    c: Perpendicular(g10,g7)
    c: Horizontal(g33)
    c: Symmetric(g-24,g-24,g33)
    c: PointOnObject(g33,g-28)
    c: Symmetric(g-24,g-24,g34)
    c: DistanceY(g35,g35) = 25
    c: Symmetric(g35,g35,g33)
    c: Distance(g36) = 41
    c: Coincident(g36,g35)
    c: Horizontal(g36)
    c: Coincident(g37,g35)
    c: Horizontal(g37)
    c: Coincident(g38,g36)
    c: Vertical(g38)
    c: Coincident(g37,g38)
    c: Diameter(g39) = 6.8
    c: Diameter(g40) = 6.8
    c: Tangent(g39,g36)
    c: Tangent(g40,g37)
    c: Tangent(g39,g35)
    c: Tangent(g40,g35)
    c: Diameter(g41) = 6.8
    c: Diameter(g42) = 6.8
    c: Tangent(g41,g36)
    c: Tangent(g42,g37)
    c: DistanceX(g41,g39) = 24.6
    c: DistanceX(g42,g40) = 24.6
    c: Distance(g43) = 11.2
    c: Coincident(g43,g33)
    c: PointOnObject(g43,g33)
    c: PointOnObject(g43,g35)
    c: Distance(g44) = 21
    c: Coincident(g44,g43)
    c: PointOnObject(g44,g33)
    c: Coincident(g45,g46)
    c: Coincident(g46,g47)
    c: Coincident(g47,g48)
    c: Coincident(g48,g45)
    c: Horizontal(g45)
    c: Horizontal(g47)
    c: Vertical(g46)
    c: Vertical(g48)
    c: Symmetric(g47,g45,g49)
    c: Distance(g46,g48) = 10.6
    c: Distance(g45,g47) = 10
    c: Coincident(g49,g44)
    c: Diameter(g50) = 5.6
    c: Coincident(g50,g44)
    c: Distance(g51) = 11
    c: Symmetric(g51,g51,g33)
    c: DistanceX(g51,g43) = 9
    c: Diameter(g52) = 6
    c: Coincident(g52,g51)
    c: Diameter(g53) = 6
    c: Coincident(g53,g51)
    c: Coincident(g40,g55)
    c: Coincident(g39,g54)
    c: Coincident(g41,g57)
    c: Coincident(g42,g56)
    c: Diameter(g58) = 3
    c: Diameter(g59) = 3
    c: Diameter(g60) = 3
    c: Coincident(g58,g-44)
    c: Coincident(g59,g-46)
    c: Coincident(g60,g-45)
FEATURE [Sketcher::SketchObject] Sketch078
  ArcFitTolerance = 1e-06
  AttachmentSupport = -> [XZ_Plane005]
  FullyConstrained = true
  MakeInternals = false
  MapMode = 5
  Placement = pos=(0,0,0) rot=(1,0,0;1.5708rad)
  sketch-geometry (5):
    g0: LineSegment [constr] StartX=0 StartY=5.5 StartZ=0 EndX=0 EndY=-5.5 EndZ=0
    g1: ArcOfCircle CenterX=0 CenterY=5.5 CenterZ=0 NormalX=0 NormalY=0 NormalZ=1 AngleXU=0 Radius=2.7 StartAngle=0 EndAngle=3.14159
    g2: ArcOfCircle CenterX=0 CenterY=-5.5 CenterZ=0 NormalX=0 NormalY=0 NormalZ=1 AngleXU=0 Radius=2.7 StartAngle=3.1416 EndAngle=6.28318
    g3: LineSegment StartX=-2.7 StartY=5.5 StartZ=0 EndX=-2.7 EndY=-5.50001 EndZ=0
    g4: LineSegment StartX=2.7 StartY=5.5 StartZ=0 EndX=2.7 EndY=-5.50001 EndZ=0
  constraints (13):
    c: Distance(g0) = 11
    c: Vertical(g0)
    c: Symmetric(g0,g0,g-1)
    c: Radius(g1) = 2.7
    c: Coincident(g1,g0)
    c: Radius(g2) = 2.7
    c: Coincident(g2,g0)
    c: Vertical(g3)
    c: Vertical(g4)
    c: Coincident(g2,g4)
    c: Coincident(g2,g3)
    c: Tangent(g3,g1) = -1.5708
    c: Tangent(g4,g1) = 1.5708
FEATURE [PartDesign::Pad] Pad002
  Direction = (0,-1,2e-16)
  Length = 0.8
  Length2 = 10
  Placement = pos=(0,0,0) rot=(1,0,0;1.5708rad)
  Profile = -> Sketch078
  ReferenceAxis = -> Sketch078 [N_Axis]
  Refine = true
  Suppressed = false
  Type = 0
FEATURE [Sketcher::SketchObject] Sketch079
  ArcFitTolerance = 1e-06
  AttachmentSupport = -> [XZ_Plane005]
  ExternalGeometry = -> [Sketch078]
  FullyConstrained = true
  MakeInternals = false
  MapMode = 5
  Placement = pos=(0,0,0) rot=(1,0,0;1.5708rad)
  sketch-geometry (2):
    g0: Circle CenterX=-1e-16 CenterY=5.5 CenterZ=0 NormalX=0 NormalY=0 NormalZ=1 AngleXU=0 Radius=2.7
    g1: Circle CenterX=0 CenterY=-5.5 CenterZ=0 NormalX=0 NormalY=0 NormalZ=1 AngleXU=0 Radius=2.7
  constraints (4):
    c: Coincident(g0,g-3)
    c: PointOnObject(g-3,g0)
    c: Coincident(g1,g-4)
    c: Equal(g1,g-4)
FEATURE [PartDesign::Pad] Pad003
  BaseFeature = -> Pad002
  Direction = (0,-1,2e-16)
  Length = 5
  Length2 = 10
  Placement = pos=(0,0,0) rot=(1,0,0;1.5708rad)
  Profile = -> Sketch079
  ReferenceAxis = -> Sketch079 [N_Axis]
  Refine = true
  Suppressed = false
  Type = 0
FEATURE [PartDesign::Fillet] Fillet001
  Base = -> Pad003 [Edge16,Edge14]
  BaseFeature = -> Pad003
  Placement = pos=(0,0,0) rot=(1,0,0;1.5708rad)
  Radius = 0.4
  Refine = true
  SupportTransform = false
  Suppressed = false
  UseAllEdges = false
FEATURE [PartDesign::Body] Body005  label="pulsanti lato destro"
  AllowCompound = false
  Group = -> [Sketch078,Pad002,Sketch079,Pad003,Fillet001]
  Origin = -> Origin005
  Tip = -> Fillet001
FEATURE [PartDesign::SubShapeBinder] Binder
  BindCopyOnChange = 0
  BindMode = 0
  ClaimChildren = false
  Context = -> Body006 [Binder.]
  Fuse = false
  MakeFace = true
  OffsetFill = false
  OffsetIntersection = false
  OffsetJoinType = 0
  OffsetOpenResult = false
  PartialLoad = false
  Refine = true
  Relative = true
  Support = -> [Body[Sketch074.]]
  _Version = 2
FEATURE [PartDesign::SubShapeBinder] Binder001
  BindCopyOnChange = 0
  BindMode = 0
  ClaimChildren = false
  Context = -> Body007 [Binder001.]
  Fuse = false
  MakeFace = true
  OffsetFill = false
  OffsetIntersection = false
  OffsetJoinType = 0
  OffsetOpenResult = false
  PartialLoad = false
  Refine = true
  Relative = true
  Support = -> [Body[Sketch075.]]
  _Version = 2
FEATURE [Mesh::Feature] logo_per_PCB_definitivo_positivo
  Placement = pos=(-191,17,-66) rot=(0,1,1;0rad)
FEATURE [Sketcher::SketchObject] Sketch114  label="Sketch114 - base lato DX"
  ArcFitTolerance = 1e-06
  AttachmentSupport = -> [Binder001]
  ExternalGeometry = -> [Binder001]
  FullyConstrained = true
  MakeInternals = false
  MapMode = 5
  Placement = pos=(0,1e-15,0) rot=(0,0.707107,0.707107;3.14159rad)
  sketch-geometry (30):
    g0: Circle CenterX=5.6 CenterY=34.8 CenterZ=0 NormalX=0 NormalY=0 NormalZ=1 AngleXU=0 Radius=1.8
    g1: Circle CenterX=5.6 CenterY=7.6 CenterZ=0 NormalX=0 NormalY=0 NormalZ=1 AngleXU=0 Radius=1.8
    g2: Circle CenterX=24.2 CenterY=26.7 CenterZ=0 NormalX=0 NormalY=0 NormalZ=1 AngleXU=0 Radius=3
    g3: Circle CenterX=24.2 CenterY=15.7 CenterZ=0 NormalX=0 NormalY=0 NormalZ=1 AngleXU=0 Radius=3
    g4: Circle CenterX=36.2 CenterY=21.2 CenterZ=0 NormalX=0 NormalY=0 NormalZ=1 AngleXU=0 Radius=2.8
    g5: Circle CenterX=78.51 CenterY=34.8 CenterZ=0 NormalX=0 NormalY=0 NormalZ=1 AngleXU=0 Radius=1.8
    g6: Circle CenterX=78.51 CenterY=7.6 CenterZ=0 NormalX=0 NormalY=0 NormalZ=1 AngleXU=0 Radius=1.8
    g7: Circle CenterX=184.08 CenterY=34.8 CenterZ=0 NormalX=0 NormalY=0 NormalZ=1 AngleXU=0 Radius=1.8
    g8: Circle CenterX=213.443 CenterY=-76.8316 CenterZ=0 NormalX=0 NormalY=0 NormalZ=1 AngleXU=0 Radius=1.8
    g9: Circle CenterX=179.305 CenterY=-76.8316 CenterZ=0 NormalX=0 NormalY=0 NormalZ=1 AngleXU=0 Radius=1.8
    g10: ArcOfCircle [constr] CenterX=132.428 CenterY=4 CenterZ=0 NormalX=0 NormalY=0 NormalZ=1 AngleXU=0 Radius=16 StartAngle=0.314159 EndAngle=1.5708
    g11: ArcOfCircle CenterX=107.6 CenterY=4 CenterZ=0 NormalX=0 NormalY=0 NormalZ=1 AngleXU=0 Radius=16 StartAngle=1.5708 EndAngle=3.00366
    g12: ArcOfCircle CenterX=207.583 CenterY=4 CenterZ=0 NormalX=0 NormalY=0 NormalZ=1 AngleXU=0 Radius=17 StartAngle=1.85815 EndAngle=3.57792
    g13: ArcOfCircle CenterX=184.801 CenterY=-67.3089 CenterZ=0 NormalX=0 NormalY=0 NormalZ=1 AngleXU=0 Radius=33.7833 StartAngle=5.88425 EndAngle=6.71952
    g14: LineSegment StartX=0 StartY=39.2 StartZ=0 EndX=0 EndY=3.2 EndZ=0
    g15: LineSegment StartX=0 StartY=3.2 StartZ=0 EndX=82.8 EndY=3.2 EndZ=0
    g16: LineSegment StartX=82.8 StartY=3.2 StartZ=0 EndX=82.8 EndY=6.2 EndZ=0
    g17: LineSegment StartX=82.8 StartY=6.2 StartZ=0 EndX=91.752 EndY=6.2 EndZ=0
    g18: LineSegment StartX=107.6 StartY=20 StartZ=0 EndX=132.428 EndY=20 EndZ=0
    g19: LineSegment StartX=147.645 StartY=8.94427 StartZ=0 EndX=176.685 EndY=-80.4316 EndZ=0
    g20: LineSegment StartX=176.685 StartY=-80.4316 StartZ=0 EndX=215.932 EndY=-80.4316 EndZ=0
    g21: LineSegment StartX=215.42 StartY=-53.0314 StartZ=0 EndX=192.176 EndY=-3.18451 EndZ=0
    g22: LineSegment StartX=202.765 StartY=20.303 StartZ=0 EndX=195.887 EndY=39.2 EndZ=0
    g23: LineSegment StartX=195.887 StartY=39.2 StartZ=0 EndX=0 EndY=39.2 EndZ=0
    g24: LineSegment StartX=196.467 StartY=26.4942 StartZ=0 EndX=194.073 EndY=33.0721 EndZ=0
    g25: LineSegment StartX=194.073 StartY=33.0721 StartZ=0 EndX=189.939 EndY=31.5672 EndZ=0
    g26: LineSegment StartX=189.939 StartY=31.5672 StartZ=0 EndX=192.333 EndY=24.9893 EndZ=0
    g27: LineSegment StartX=192.333 StartY=24.9893 StartZ=0 EndX=196.467 EndY=26.4942 EndZ=0
    g28: LineSegment StartX=132.428 StartY=20 StartZ=0 EndX=144.053 EndY=20 EndZ=0
    g29: LineSegment StartX=144.053 StartY=20 StartZ=0 EndX=147.645 EndY=8.94427 EndZ=0
  constraints (65):
    c: Equal(g0,g-25)
    c: Equal(g2,g-29)
    c: Equal(g3,g-30)
    c: Equal(g4,g-28)
    c: Equal(g1,g-26)
    c: Coincident(g0,g-25)
    c: Coincident(g1,g-26)
    c: Coincident(g2,g-29)
    c: Coincident(g3,g-30)
    c: Coincident(g4,g-28)
    c: Equal(g5,g-23)
    c: Equal(g6,g-24)
    c: Coincident(g5,g-23)
    c: Coincident(g6,g-24)
    c: Equal(g7,g-20)
    c: Coincident(g7,g-20)
    c: Equal(g9,g-22)
    c: Coincident(g9,g-22)
    c: Equal(g8,g-21)
    c: Coincident(g8,g-21)
    c: Equal(g13,g-12)
    c: Equal(g12,g-14)
    c: Equal(g10,g-9)
    c: Equal(g11,g-7)
    c: Coincident(g14,g-27)
    c: Coincident(g14,g-27)
    c: Coincident(g15,g14)
    c: Coincident(g15,g-5)
    c: Coincident(g16,g15)
    c: Coincident(g16,g-6)
    c: Coincident(g17,g16)
    c: Coincident(g17,g-7)
    c: Coincident(g11,g17)
    c: Coincident(g11,g-8)
    c: Coincident(g18,g11)
    c: Coincident(g18,g-9)
    c: Coincident(g10,g18)
    c: Coincident(g10,g-10)
    c: Coincident(g19,g10)
    c: Coincident(g19,g-11)
    c: Coincident(g20,g19)
    c: Coincident(g20,g-12)
    c: Coincident(g13,g20)
    c: Coincident(g13,g-13)
    c: Coincident(g21,g13)
    c: Coincident(g21,g-14)
    c: Coincident(g12,g21)
    c: Coincident(g12,g-15)
    c: Coincident(g22,g12)
    c: Coincident(g22,g-15)
    c: Coincident(g23,g22)
    c: Coincident(g23,g14)
    c: Coincident(g24,g-18)
    c: Coincident(g24,g-16)
    c: Coincident(g25,g24)
    c: Coincident(g25,g-19)
    c: Coincident(g26,g25)
    c: Coincident(g26,g-19)
    c: Coincident(g27,g26)
    c: Coincident(g27,g24)
    c: Coincident(g29,g10)
    c: Coincident(g28,g10)
    c: Coincident(g29,g28)
    c: Parallel(g28,g18)
    c: Parallel(g29,g19)
FEATURE [PartDesign::Pad] Pad011
  Direction = (0,1,-2e-16)
  Length = 2
  Length2 = 10
  Profile = -> Sketch114
  ReferenceAxis = -> Sketch114 [N_Axis]
  Refine = true
  Reversed = true
  Suppressed = false
  Type = 0
FEATURE [Sketcher::SketchObject] Sketch115
  ArcFitTolerance = 1e-06
  AttachmentSupport = -> [Pad011]
  ExternalGeometry = -> [Binder001]
  FullyConstrained = true
  MakeInternals = false
  MapMode = 5
  Placement = pos=(0,1.7e-15,0) rot=(0,0.707107,0.707107;3.14159rad)
  sketch-geometry (4):
    g0: ArcOfCircle CenterX=24.2 CenterY=26.7 CenterZ=0 NormalX=0 NormalY=0 NormalZ=1 AngleXU=0 Radius=3 StartAngle=4.48384e-08 EndAngle=3.14159
    g1: ArcOfCircle CenterX=24.2 CenterY=15.7 CenterZ=0 NormalX=0 NormalY=0 NormalZ=1 AngleXU=0 Radius=3 StartAngle=3.14159 EndAngle=6.28318
    g2: LineSegment StartX=21.2 StartY=26.7 StartZ=0 EndX=21.2 EndY=15.7 EndZ=0
    g3: LineSegment StartX=27.2 StartY=26.7 StartZ=0 EndX=27.2 EndY=15.7 EndZ=0
  constraints (12):
    c: Equal(g1,g-4)
    c: Equal(g0,g-3)
    c: Coincident(g0,g-3)
    c: Coincident(g1,g-4)
    c: Vertical(g2)
    c: Vertical(g3)
    c: Tangent(g3,g-3)
    c: Tangent(g2,g-3)
    c: Coincident(g0,g2)
    c: Coincident(g0,g3)
    c: Coincident(g1,g2)
    c: Coincident(g3,g1)
FEATURE [Sketcher::SketchObject] Sketch117  label="Sketch117 - fori per inserto M3 x 3 x 4.5"
  ArcFitTolerance = 1e-06
  AttachmentSupport = -> [Pad011]
  ExternalGeometry = -> [Binder001]
  FullyConstrained = true
  MakeInternals = false
  MapMode = 5
  Placement = pos=(0,1.7e-15,0) rot=(0,0.707107,0.707107;3.14159rad)
  sketch-geometry (4):
    g0: Circle CenterX=43.2 CenterY=30.3 CenterZ=0 NormalX=0 NormalY=0 NormalZ=1 AngleXU=0 Radius=2.25
    g1: Circle CenterX=43.2 CenterY=12.1 CenterZ=0 NormalX=0 NormalY=0 NormalZ=1 AngleXU=0 Radius=2.25
    g2: Circle CenterX=18.6 CenterY=30.3 CenterZ=0 NormalX=0 NormalY=0 NormalZ=1 AngleXU=0 Radius=2.25
    g3: Circle CenterX=18.6 CenterY=12.1 CenterZ=0 NormalX=0 NormalY=0 NormalZ=1 AngleXU=0 Radius=2.25
  constraints (8):
    c: Diameter(g0) = 4.5
    c: Diameter(g1) = 4.5
    c: Diameter(g2) = 4.5
    c: Diameter(g3) = 4.5
    c: Coincident(g2,g-3)
    c: Coincident(g3,g-6)
    c: Coincident(g0,g-4)
    c: Coincident(g1,g-5)
FEATURE [Sketcher::SketchObject] Sketch118
  ArcFitTolerance = 1e-06
  AttachmentSupport = -> [Pad011]
  ExternalGeometry = -> [Binder001]
  FullyConstrained = true
  MakeInternals = false
  MapMode = 5
  Placement = pos=(0,-2,0) rot=(1,0,0;1.5708rad)
  sketch-geometry (12):
    g0: Circle CenterX=-78.51 CenterY=34.8 CenterZ=0 NormalX=0 NormalY=0 NormalZ=1 AngleXU=0 Radius=1.8
    g1: Circle CenterX=-78.51 CenterY=7.6 CenterZ=0 NormalX=0 NormalY=0 NormalZ=1 AngleXU=0 Radius=1.8
    g2: Circle CenterX=-5.6 CenterY=34.8 CenterZ=0 NormalX=0 NormalY=0 NormalZ=1 AngleXU=0 Radius=1.8
    g3: Circle CenterX=-5.6 CenterY=7.6 CenterZ=0 NormalX=0 NormalY=0 NormalZ=1 AngleXU=0 Radius=1.8
    g4: LineSegment StartX=0 StartY=39.2 StartZ=0 EndX=0 EndY=3.2 EndZ=0
    g5: LineSegment StartX=0 StartY=3.2 StartZ=0 EndX=-82.8 EndY=3.2 EndZ=0
    g6: LineSegment StartX=-82.8 StartY=3.2 StartZ=0 EndX=-82.8 EndY=39.2 EndZ=0
    g7: LineSegment StartX=-82.8 StartY=39.2 StartZ=0 EndX=0 EndY=39.2 EndZ=0
    g8: ArcOfCircle CenterX=-65 CenterY=21.2 CenterZ=0 NormalX=0 NormalY=0 NormalZ=1 AngleXU=0 Radius=10 StartAngle=1.5708 EndAngle=4.71239
    g9: ArcOfCircle CenterX=-19 CenterY=21.2 CenterZ=0 NormalX=0 NormalY=0 NormalZ=1 AngleXU=0 Radius=10 StartAngle=4.71239 EndAngle=7.85398
    g10: LineSegment StartX=-65 StartY=31.2 StartZ=0 EndX=-19 EndY=31.2 EndZ=0
    g11: LineSegment StartX=-65 StartY=11.2 StartZ=0 EndX=-19 EndY=11.2 EndZ=0
  constraints (25):
    c: Equal(g2,g-5)
    c: Equal(g3,g-7)
    c: Equal(g1,g-6)
    c: Equal(g0,g-4)
    c: Coincident(g0,g-4)
    c: Coincident(g1,g-6)
    c: Coincident(g3,g-7)
    c: Coincident(g2,g-5)
    c: Coincident(g4,g-8)
    c: Coincident(g4,g-9)
    c: Coincident(g5,g4)
    c: Coincident(g5,g-10)
    c: Coincident(g6,g5)
    c: PointOnObject(g6,g-3)
    c: Vertical(g6)
    c: Coincident(g7,g6)
    c: Coincident(g7,g4)
    c: Tangent(g8,g10) = 1.5708
    c: Tangent(g8,g11) = -1.5708
    c: Tangent(g9,g10) = 1.5708
    c: Tangent(g9,g11) = -1.5708
    c: Equal(g8,g9)
    c: Radius(g8) = 10
    c: Coincident(g8,g-11)
    c: Coincident(g9,g-12)
FEATURE [Sketcher::SketchObject] Sketch120
  ArcFitTolerance = 1e-06
  AttachmentSupport = -> [Pad011]
  ExternalGeometry = -> [Binder001]
  FullyConstrained = true
  MakeInternals = false
  MapMode = 5
  Placement = pos=(0,-2,0) rot=(1,0,0;1.5708rad)
  sketch-geometry (4):
    g0: LineSegment StartX=-137.815 StartY=39.2 StartZ=0 EndX=-142.655 EndY=24.303 EndZ=0
    g1: LineSegment StartX=-137.815 StartY=39.2 StartZ=0 EndX=-110.815 EndY=39.2 EndZ=0
    g2: LineSegment StartX=-142.655 StartY=24.303 StartZ=0 EndX=-110.815 EndY=24.303 EndZ=0
    g3: ArcOfCircle CenterX=-92.2534 CenterY=31.7515 CenterZ=0 NormalX=0 NormalY=0 NormalZ=1 AngleXU=0 Radius=20 StartAngle=2.75997 EndAngle=3.52321
  constraints (12):
    c: PointOnObject(g0,g-3)
    c: Coincident(g1,g0)
    c: PointOnObject(g1,g-3)
    c: Coincident(g2,g0)
    c: Horizontal(g2)
    c: Tangent(g0,g-4)
    c: Vertical(g2,g1)
    c: DistanceX(g1,g1) = 27
    c: DistanceY(g-6,g0) = 4
    c: Radius(g3) = 20
    c: Coincident(g3,g1)
    c: Coincident(g3,g2)
FEATURE [Sketcher::SketchObject] Sketch121
  ArcFitTolerance = 1e-06
  AttachmentSupport = -> [Pad011]
  ExternalGeometry = -> [Binder001]
  FullyConstrained = true
  MakeInternals = false
  MapMode = 5
  Placement = pos=(0,-2,0) rot=(1,0,0;1.5708rad)
  sketch-geometry (15):
    g0: LineSegment StartX=-137.815 StartY=39.2 StartZ=0 EndX=-143.955 EndY=20.303 EndZ=0
    g1: LineSegment StartX=-143.955 StartY=20.303 StartZ=0 EndX=-190.141 EndY=20.303 EndZ=0
    g2: LineSegment StartX=-190.141 StartY=20.303 StartZ=0 EndX=-186.139 EndY=31.3 EndZ=0
    g3: LineSegment StartX=-178.754 StartY=39.2 StartZ=0 EndX=-180.791 EndY=33.6029 EndZ=0
    g4: ArcOfCircle CenterX=-184.08 CenterY=34.8 CenterZ=0 NormalX=0 NormalY=0 NormalZ=1 AngleXU=0 Radius=3.5 StartAngle=4.71239 EndAngle=5.93412
    g5: LineSegment StartX=-184.08 StartY=31.3 StartZ=0 EndX=-186.139 EndY=31.3 EndZ=0
    g6: LineSegment StartX=-137.815 StartY=39.2 StartZ=0 EndX=-156.815 EndY=39.2 EndZ=0
    g7: LineSegment StartX=-168.815 StartY=39.2 StartZ=0 EndX=-178.754 EndY=39.2 EndZ=0
    g8: LineSegment StartX=-157.815 StartY=39.2 StartZ=0 EndX=-167.815 EndY=39.2 EndZ=0
    g9: LineSegment StartX=-168.815 StartY=31.2 StartZ=0 EndX=-156.815 EndY=31.2 EndZ=0
    g10: LineSegment StartX=-167.436 StartY=36.2 StartZ=0 EndX=-157.436 EndY=36.2 EndZ=0
    g11: ArcOfCircle CenterX=-176.411 CenterY=35.2 CenterZ=0 NormalX=0 NormalY=0 NormalZ=1 AngleXU=0 Radius=20 StartAngle=6.08183 EndAngle=6.48454
    g12: ArcOfCircle CenterX=-188.411 CenterY=35.2 CenterZ=0 NormalX=0 NormalY=0 NormalZ=1 AngleXU=0 Radius=20 StartAngle=6.08183 EndAngle=6.48454
    g13: ArcOfCircle CenterX=-177.411 CenterY=35.2 CenterZ=0 NormalX=0 NormalY=0 NormalZ=1 AngleXU=0 Radius=20 StartAngle=0.0500209 EndAngle=0.201358
    g14: ArcOfCircle CenterX=-187.411 CenterY=35.2 CenterZ=0 NormalX=0 NormalY=0 NormalZ=1 AngleXU=0 Radius=20 StartAngle=0.0500209 EndAngle=0.201358
  constraints (46):
    c: PointOnObject(g0,g-3)
    c: Tangent(g0,g-5)
    c: Coincident(g1,g0)
    c: Horizontal(g1)
    c: Coincident(g2,g1)
    c: PointOnObject(g3,g-3)
    c: Parallel(g3,g-6)
    c: Parallel(g2,g-6)
    c: Radius(g4) = 3.5
    c: Coincident(g4,g-7)
    c: Tangent(g3,g4) = 1.5708
    c: Horizontal(g5)
    c: Tangent(g5,g4) = 1.5708
    c: DistanceX(g-8,g5) = 3.8
    c: Coincident(g2,g5)
    c: Coincident(g6,g0)
    c: PointOnObject(g6,g-3)
    c: DistanceX(g6,g6) = 19
    c: PointOnObject(g7,g-3)
    c: DistanceX(g7,g6) = 12
    c: Coincident(g7,g3)
    c: PointOnObject(g8,g-3)
    c: PointOnObject(g8,g-3)
    c: DistanceX(g8,g8) = 10
    c: DistanceX(g8,g6) = 1
    c: Horizontal(g9)
    c: Vertical(g7,g9)
    c: Vertical(g6,g9)
    c: DistanceY(g9,g7) = 8
    c: Horizontal(g10)
    c: Equal(g8,g10)
    c: DistanceY(g10,g8) = 3
    c: Radius(g11) = 20
    c: Coincident(g11,g6)
    c: Coincident(g11,g9)
    c: Radius(g12) = 20
    c: Coincident(g12,g7)
    c: Coincident(g12,g9)
    c: Equal(g13,g11)
    c: Coincident(g13,g8)
    c: Coincident(g13,g10)
    c: Horizontal(g13,g11)
    c: Equal(g14,g12)
    c: Coincident(g14,g8)
    c: Coincident(g14,g10)
    c: Horizontal(g1,g-6)
FEATURE [Sketcher::SketchObject] Sketch122
  ArcFitTolerance = 1e-06
  AttachmentSupport = -> [Pad011]
  ExternalGeometry = -> [Binder001]
  FullyConstrained = true
  MakeInternals = false
  MapMode = 5
  Placement = pos=(0,-2,0) rot=(1,0,0;1.5708rad)
  sketch-geometry (8):
    g0: LineSegment StartX=-202.765 StartY=20.303 StartZ=0 EndX=-143.955 EndY=20.303 EndZ=0
    g1: ArcOfCircle CenterX=-184.801 CenterY=-67.3089 CenterZ=0 NormalX=0 NormalY=0 NormalZ=1 AngleXU=0 Radius=33.7833 StartAngle=2.70526 EndAngle=3.54053
    g2: LineSegment StartX=-176.685 StartY=-80.4316 StartZ=0 EndX=-215.932 EndY=-80.4316 EndZ=0
    g3: LineSegment StartX=-215.42 StartY=-53.0315 StartZ=0 EndX=-192.176 EndY=-3.18454 EndZ=0
    g4: ArcOfCircle CenterX=-207.583 CenterY=4 CenterZ=0 NormalX=0 NormalY=0 NormalZ=1 AngleXU=0 Radius=17 StartAngle=5.84685 EndAngle=7.56663
    g5: Circle CenterX=-213.443 CenterY=-76.8316 CenterZ=0 NormalX=0 NormalY=0 NormalZ=1 AngleXU=0 Radius=3
    g6: Circle CenterX=-179.305 CenterY=-76.8316 CenterZ=0 NormalX=0 NormalY=0 NormalZ=1 AngleXU=0 Radius=3
    g7: LineSegment StartX=-143.955 StartY=20.303 StartZ=0 EndX=-176.685 EndY=-80.4316 EndZ=0
  constraints (18):
    c: Coincident(g0,g-6)
    c: Coincident(g1,g-7)
    c: Coincident(g1,g-8)
    c: Coincident(g2,g1)
    c: Tangent(g3,g-5)
    c: Coincident(g4,g-6)
    c: Coincident(g4,g0)
    c: Coincident(g3,g4)
    c: Coincident(g1,g3)
    c: Diameter(g5) = 6
    c: Diameter(g6) = 6
    c: Coincident(g5,g-9)
    c: Coincident(g6,g-10)
    c: Horizontal(g0)
    c: Horizontal(g2)
    c: Coincident(g7,g0)
    c: Coincident(g7,g2)
    c: Tangent(g7,g-4)
FEATURE [Sketcher::SketchObject] Sketch123
  ArcFitTolerance = 1e-06
  AttachmentSupport = -> [Pad011]
  ExternalGeometry = -> [Binder001]
  FullyConstrained = true
  MakeInternals = false
  MapMode = 5
  Placement = pos=(0,-2,0) rot=(1,0,0;1.5708rad)
  sketch-geometry (4):
    g0: LineSegment StartX=-108 StartY=36.8 StartZ=0 EndX=-90 EndY=36.8 EndZ=0
    g1: LineSegment StartX=-108 StartY=36.8 StartZ=0 EndX=-108 EndY=26.8 EndZ=0
    g2: LineSegment StartX=-108 StartY=26.8 StartZ=0 EndX=-90 EndY=26.8 EndZ=0
    g3: ArcOfCircle CenterX=-94 CenterY=31.8 CenterZ=0 NormalX=0 NormalY=0 NormalZ=1 AngleXU=0 Radius=6.40312 StartAngle=5.38713 EndAngle=7.17924
  constraints (13):
    c: Horizontal(g0)
    c: Coincident(g1,g0)
    c: Vertical(g1)
    c: Coincident(g2,g1)
    c: Horizontal(g2)
    c: DistanceX(g0,g0) = 18
    c: DistanceY(g1,g1) = 10
    c: Equal(g0,g2)
    c: DistanceX(g0,g-3) = 90
    c: DistanceY(g0,g-3) = 2.4
    c: Coincident(g3,g0)
    c: Coincident(g3,g2)
    c: DistanceX(g3,g0) = 4
FEATURE [PartDesign::Chamfer] Chamfer014
  Angle = 45
  Base = -> Pad011 [Edge80,Edge4,Edge7]
  BaseFeature = -> Pad011
  ChamferType = 0
  FlipDirection = false
  Refine = true
  Size = 1.9
  Size2 = 1
  SupportTransform = false
  Suppressed = false
  UseAllEdges = false
FEATURE [PartDesign::Pocket] Pocket006
  BaseFeature = -> Chamfer014
  Direction = (0,-1,2e-16)
  Length = 1.2
  Length2 = 5
  Profile = -> Sketch115
  ReferenceAxis = -> Sketch115 [N_Axis]
  Refine = true
  Suppressed = false
  Type = 0
FEATURE [Sketcher::SketchObject] Sketch116  label="Sketch116 - pieno per inserto M3 x 3 x 4,5"
  ArcFitTolerance = 1e-06
  AttachmentSupport = -> [Pocket006]
  ExternalGeometry = -> [Binder001]
  FullyConstrained = true
  MakeInternals = false
  MapMode = 5
  Placement = pos=(0,1.7e-15,0) rot=(0,0.707107,0.707107;3.14159rad)
  sketch-geometry (4):
    g0: Circle CenterX=43.2 CenterY=30.3 CenterZ=0 NormalX=0 NormalY=0 NormalZ=1 AngleXU=0 Radius=3.4
    g1: Circle CenterX=43.2 CenterY=12.1 CenterZ=0 NormalX=0 NormalY=0 NormalZ=1 AngleXU=0 Radius=3.4
    g2: Circle CenterX=18.6 CenterY=30.3 CenterZ=0 NormalX=0 NormalY=0 NormalZ=1 AngleXU=0 Radius=3.4
    g3: Circle CenterX=18.6 CenterY=12.1 CenterZ=0 NormalX=0 NormalY=0 NormalZ=1 AngleXU=0 Radius=3.4
  constraints (8):
    c: Diameter(g0) = 6.8
    c: Diameter(g1) = 6.8
    c: Diameter(g2) = 6.8
    c: Diameter(g3) = 6.8
    c: Coincident(g2,g-3)
    c: Coincident(g0,g-4)
    c: Coincident(g3,g-6)
    c: Coincident(g1,g-5)
FEATURE [PartDesign::Pad] Pad012
  BaseFeature = -> Pocket006
  Direction = (0,1,-2e-16)
  Length = 2.4
  Length2 = 10
  Profile = -> Sketch116
  ReferenceAxis = -> Sketch116 [N_Axis]
  Refine = true
  Suppressed = false
  Type = 0
FEATURE [PartDesign::Pocket] Pocket007
  BaseFeature = -> Pad012
  Direction = (0,-1,2e-16)
  Length = 0.6
  Length2 = 2.4
  Profile = -> Sketch117
  ReferenceAxis = -> Sketch117 [N_Axis]
  Refine = true
  Suppressed = false
  Type = 4
FEATURE [PartDesign::Pad] Pad013
  BaseFeature = -> Pocket007
  Direction = (0,-1,2e-16)
  Length = 1.6
  Length2 = 10
  Profile = -> Sketch118
  ReferenceAxis = -> Sketch118 [N_Axis]
  Refine = true
  Suppressed = false
  Type = 0
FEATURE [Sketcher::SketchObject] Sketch119
  ArcFitTolerance = 1e-06
  AttachmentSupport = -> [Pad013]
  ExternalGeometry = -> [Binder001]
  FullyConstrained = true
  MakeInternals = false
  MapMode = 5
  Placement = pos=(0,-3.6,0) rot=(1,0,0;1.5708rad)
  sketch-geometry (21):
    g0: LineSegment [constr] StartX=-82.8 StartY=3.2 StartZ=0 EndX=-82.8 EndY=39.2 EndZ=0
    g1: ArcOfCircle CenterX=-78.51 CenterY=34.8 CenterZ=0 NormalX=0 NormalY=0 NormalZ=1 AngleXU=0 Radius=3.5 StartAngle=4.71239 EndAngle=6.28319
    g2: ArcOfCircle CenterX=-78.51 CenterY=7.6 CenterZ=0 NormalX=0 NormalY=0 NormalZ=1 AngleXU=0 Radius=3.5 StartAngle=0 EndAngle=1.5708
    g3: ArcOfCircle CenterX=-5.6 CenterY=34.8 CenterZ=0 NormalX=0 NormalY=0 NormalZ=1 AngleXU=0 Radius=3.5 StartAngle=3.14159 EndAngle=4.71239
    g4: ArcOfCircle CenterX=-5.6 CenterY=7.6 CenterZ=0 NormalX=0 NormalY=0 NormalZ=1 AngleXU=0 Radius=3.5 StartAngle=1.5708 EndAngle=3.14159
    g5: LineSegment StartX=0 StartY=39.2 StartZ=0 EndX=0 EndY=31.3 EndZ=0
    g6: LineSegment StartX=0 StartY=39.2 StartZ=0 EndX=-9.1 EndY=39.2 EndZ=0
    g7: LineSegment StartX=0 StartY=3.2 StartZ=0 EndX=0 EndY=11.1 EndZ=0
    g8: LineSegment StartX=0 StartY=3.2 StartZ=0 EndX=-9.1 EndY=3.2 EndZ=0
    g9: LineSegment StartX=-82.8 StartY=3.2 StartZ=0 EndX=-75.01 EndY=3.2 EndZ=0
    g10: LineSegment StartX=-82.8 StartY=3.2 StartZ=0 EndX=-82.8 EndY=11.1 EndZ=0
    g11: LineSegment StartX=-82.8 StartY=39.2 StartZ=0 EndX=-82.8 EndY=31.3 EndZ=0
    g12: LineSegment StartX=-82.8 StartY=39.2 StartZ=0 EndX=-75.01 EndY=39.2 EndZ=0
    g13: LineSegment StartX=-82.8 StartY=31.3 StartZ=0 EndX=-78.51 EndY=31.3 EndZ=0
    g14: LineSegment StartX=-75.01 StartY=39.2 StartZ=0 EndX=-75.01 EndY=34.8 EndZ=0
    g15: LineSegment StartX=-82.8 StartY=11.1 StartZ=0 EndX=-78.51 EndY=11.1 EndZ=0
    g16: LineSegment StartX=-75.01 StartY=3.2 StartZ=0 EndX=-75.01 EndY=7.6 EndZ=0
    g17: LineSegment StartX=-9.1 StartY=39.2 StartZ=0 EndX=-9.1 EndY=34.8 EndZ=0
    g18: LineSegment StartX=0 StartY=31.3 StartZ=0 EndX=-5.6 EndY=31.3 EndZ=0
    g19: LineSegment StartX=0 StartY=11.1 StartZ=0 EndX=-5.6 EndY=11.1 EndZ=0
    g20: LineSegment StartX=-9.1 StartY=3.2 StartZ=0 EndX=-9.1 EndY=7.6 EndZ=0
  constraints (51):
    c: Coincident(g0,g-10)
    c: PointOnObject(g0,g-8)
    c: Vertical(g0)
    c: Coincident(g1,g-3)
    c: Coincident(g2,g-4)
    c: Coincident(g3,g-5)
    c: Coincident(g4,g-6)
    c: Radius(g4) = 3.5
    c: Radius(g3) = 3.5
    c: Radius(g1) = 3.5
    c: Radius(g2) = 3.5
    c: Coincident(g5,g-9)
    c: PointOnObject(g5,g-9)
    c: Coincident(g6,g5)
    c: PointOnObject(g6,g-8)
    c: Coincident(g7,g-9)
    c: PointOnObject(g7,g-9)
    c: Coincident(g8,g7)
    c: PointOnObject(g8,g-7)
    c: Coincident(g9,g0)
    c: PointOnObject(g9,g-7)
    c: Coincident(g10,g0)
    c: PointOnObject(g10,g0)
    c: Coincident(g11,g0)
    c: PointOnObject(g11,g0)
    c: Coincident(g12,g0)
    c: PointOnObject(g12,g-8)
    c: Coincident(g13,g11)
    c: Horizontal(g13)
    c: Coincident(g14,g12)
    c: Vertical(g14)
    c: Coincident(g15,g10)
    c: Horizontal(g15)
    c: Coincident(g16,g9)
    c: Vertical(g16)
    c: Coincident(g17,g6)
    c: Vertical(g17)
    c: Coincident(g18,g5)
    c: Horizontal(g18)
    c: Coincident(g19,g7)
    c: Horizontal(g19)
    c: Coincident(g20,g8)
    c: Vertical(g20)
    c: Tangent(g20,g4) = 1.5708
    c: Tangent(g4,g19) = -1.5708
    c: Tangent(g18,g3) = 1.5708
    c: Tangent(g3,g17) = -1.5708
    c: Tangent(g13,g1) = -1.5708
    c: Tangent(g1,g14) = 1.5708
    c: Tangent(g16,g2) = -1.5708
    c: Tangent(g2,g15) = 1.5708
FEATURE [PartDesign::Pocket] Pocket008
  BaseFeature = -> Pad013
  Direction = (0,1,-2e-16)
  Length = 1.6
  Length2 = 5
  Profile = -> Sketch119
  ReferenceAxis = -> Sketch119 [N_Axis]
  Refine = true
  Suppressed = false
  Type = 0
FEATURE [PartDesign::Pad] Pad017
  BaseFeature = -> Pocket008
  Direction = (0,-1,2e-16)
  Length = 1.6
  Length2 = 10
  Profile = -> Sketch123
  ReferenceAxis = -> Sketch123 [N_Axis]
  Refine = true
  Suppressed = false
  Type = 0
FEATURE [Sketcher::SketchObject] Sketch125
  ArcFitTolerance = 1e-06
  AttachmentSupport = -> [Pad017]
  ExternalGeometry = -> [Pad017]
  FullyConstrained = true
  MakeInternals = false
  MapMode = 5
  Placement = pos=(0,-3.6,8e-16) rot=(1,0,0;1.5708rad)
  sketch-geometry (20):
    g0: LineSegment StartX=-108 StartY=35.8 StartZ=0 EndX=-108 EndY=35 EndZ=0
    g1: LineSegment StartX=-108 StartY=35 StartZ=0 EndX=-97 EndY=35 EndZ=0
    g2: LineSegment StartX=-97 StartY=35 StartZ=0 EndX=-97 EndY=35.8 EndZ=0
    g3: LineSegment StartX=-97 StartY=35.8 StartZ=0 EndX=-108 EndY=35.8 EndZ=0
    g4: LineSegment StartX=-108 StartY=28.6 StartZ=0 EndX=-108 EndY=27.8 EndZ=0
    g5: LineSegment StartX=-108 StartY=27.8 StartZ=0 EndX=-97 EndY=27.8 EndZ=0
    g6: LineSegment StartX=-97 StartY=27.8 StartZ=0 EndX=-97 EndY=28.6 EndZ=0
    g7: LineSegment StartX=-97 StartY=28.6 StartZ=0 EndX=-108 EndY=28.6 EndZ=0
    g8: LineSegment StartX=-108 StartY=30.4 StartZ=0 EndX=-108 EndY=29.6 EndZ=0
    g9: LineSegment StartX=-108 StartY=29.6 StartZ=0 EndX=-97 EndY=29.6 EndZ=0
    g10: LineSegment StartX=-97 StartY=29.6 StartZ=0 EndX=-97 EndY=30.4 EndZ=0
    g11: LineSegment StartX=-97 StartY=30.4 StartZ=0 EndX=-108 EndY=30.4 EndZ=0
    g12: LineSegment StartX=-108 StartY=32.2 StartZ=0 EndX=-108 EndY=31.4 EndZ=0
    g13: LineSegment StartX=-108 StartY=31.4 StartZ=0 EndX=-97 EndY=31.4 EndZ=0
    g14: LineSegment StartX=-97 StartY=31.4 StartZ=0 EndX=-97 EndY=32.2 EndZ=0
    g15: LineSegment StartX=-97 StartY=32.2 StartZ=0 EndX=-108 EndY=32.2 EndZ=0
    g16: LineSegment StartX=-108 StartY=34 StartZ=0 EndX=-108 EndY=33.2 EndZ=0
    g17: LineSegment StartX=-108 StartY=33.2 StartZ=0 EndX=-97 EndY=33.2 EndZ=0
    g18: LineSegment StartX=-97 StartY=33.2 StartZ=0 EndX=-97 EndY=34 EndZ=0
    g19: LineSegment StartX=-97 StartY=34 StartZ=0 EndX=-108 EndY=34 EndZ=0
  constraints (55):
    c: Coincident(g1,g0)
    c: Horizontal(g1)
    c: Coincident(g2,g1)
    c: Vertical(g2)
    c: Coincident(g3,g2)
    c: Horizontal(g3)
    c: Coincident(g3,g0)
    c: DistanceX(g1,g1) = 11
    c: DistanceY(g2,g2) = 0.8
    c: Coincident(g5,g4)
    c: Horizontal(g5)
    c: Coincident(g6,g5)
    c: Vertical(g6)
    c: Coincident(g7,g6)
    c: Horizontal(g7)
    c: Coincident(g7,g4)
    c: Coincident(g9,g8)
    c: Horizontal(g9)
    c: Coincident(g10,g9)
    c: Vertical(g10)
    c: Coincident(g11,g10)
    c: Horizontal(g11)
    c: Coincident(g11,g8)
    c: Coincident(g13,g12)
    c: Horizontal(g13)
    c: Coincident(g14,g13)
    c: Vertical(g14)
    c: Coincident(g15,g14)
    c: Horizontal(g15)
    c: Coincident(g15,g12)
    c: Coincident(g17,g16)
    c: Horizontal(g17)
    c: Coincident(g18,g17)
    c: Vertical(g18)
    c: Coincident(g19,g18)
    c: Horizontal(g19)
    c: Coincident(g19,g16)
    c: Equal(g3,g19)
    c: Equal(g3,g15)
    c: Equal(g3,g11)
    c: Equal(g3,g7)
    c: Equal(g2,g18)
    c: Equal(g2,g14)
    c: Equal(g2,g10)
    c: Equal(g2,g6)
    c: DistanceY(g-4,g4) = 1
    c: DistanceY(g4,g8) = 1
    c: DistanceY(g8,g12) = 1
    c: DistanceY(g12,g16) = 1
    c: DistanceY(g16,g0) = 1
    c: Tangent(g0,g-5)
    c: Tangent(g16,g-5)
    c: Tangent(g12,g-5)
    c: Tangent(g8,g-5)
    c: Tangent(g4,g-5)
FEATURE [PartDesign::Chamfer] Chamfer009
  Angle = 45
  Base = -> Pad017 [Edge151,Edge154]
  BaseFeature = -> Pad017
  ChamferType = 1
  FlipDirection = false
  Refine = true
  Size = 1.5
  Size2 = 2.8
  SupportTransform = false
  Suppressed = false
  UseAllEdges = false
FEATURE [PartDesign::Pocket] Pocket009
  BaseFeature = -> Chamfer009
  Direction = (0,1,-2e-16)
  Length = 1
  Length2 = 5
  Profile = -> Sketch125
  ReferenceAxis = -> Sketch125 [N_Axis]
  Refine = true
  Suppressed = false
  Type = 0
FEATURE [PartDesign::Pad] Pad014
  BaseFeature = -> Pocket009
  Direction = (0,-1,2e-16)
  Length = 0.8
  Length2 = 10
  Profile = -> Sketch120
  ReferenceAxis = -> Sketch120 [N_Axis]
  Refine = true
  Suppressed = false
  Type = 0
FEATURE [Sketcher::SketchObject] Sketch124
  ArcFitTolerance = 1e-06
  AttachmentSupport = -> [Pad014]
  ExternalGeometry = -> [Binder001]
  FullyConstrained = true
  MakeInternals = false
  MapMode = 5
  Placement = pos=(0,-2.8,6e-16) rot=(1,0,0;1.5708rad)
  sketch-geometry (4):
    g0: LineSegment StartX=-129 StartY=39.2 StartZ=0 EndX=-131.599 EndY=31.2 EndZ=0
    g1: LineSegment StartX=-118 StartY=39.2 StartZ=0 EndX=-120.599 EndY=31.2 EndZ=0
    g2: LineSegment StartX=-129 StartY=39.2 StartZ=0 EndX=-118 EndY=39.2 EndZ=0
    g3: LineSegment StartX=-120.599 StartY=31.2 StartZ=0 EndX=-131.599 EndY=31.2 EndZ=0
  constraints (12):
    c: PointOnObject(g0,g-3)
    c: PointOnObject(g1,g-3)
    c: Parallel(g-4,g0)
    c: Parallel(g-4,g1)
    c: Coincident(g2,g0)
    c: Coincident(g2,g1)
    c: DistanceX(g2,g2) = 11
    c: DistanceY(g1,g1) = 8
    c: Coincident(g3,g1)
    c: Horizontal(g3)
    c: Coincident(g3,g0)
    c: DistanceX(g1,g-3) = 118
FEATURE [PartDesign::Pad] Pad018
  BaseFeature = -> Pad014
  Direction = (0,-1,2e-16)
  Length = 1.2
  Length2 = 10
  Profile = -> Sketch124
  ReferenceAxis = -> Sketch124 [N_Axis]
  Refine = true
  Suppressed = false
  Type = 0
FEATURE [Sketcher::SketchObject] Sketch126
  ArcFitTolerance = 1e-06
  AttachmentSupport = -> [Pad018]
  ExternalGeometry = -> [Pad018]
  FullyConstrained = true
  MakeInternals = false
  MapMode = 5
  Placement = pos=(0,-4,0) rot=(1,0,0;1.5708rad)
  sketch-geometry (8):
    g0: LineSegment StartX=-129.877 StartY=36.5 StartZ=0 EndX=-130.137 EndY=35.7 EndZ=0
    g1: LineSegment StartX=-130.69 StartY=34 StartZ=0 EndX=-130.95 EndY=33.2 EndZ=0
    g2: LineSegment StartX=-129.877 StartY=36.5 StartZ=0 EndX=-118.877 EndY=36.5 EndZ=0
    g3: LineSegment StartX=-130.137 StartY=35.7 StartZ=0 EndX=-119.137 EndY=35.7 EndZ=0
    g4: LineSegment StartX=-130.69 StartY=34 StartZ=0 EndX=-119.69 EndY=34 EndZ=0
    g5: LineSegment StartX=-130.95 StartY=33.2 StartZ=0 EndX=-119.95 EndY=33.2 EndZ=0
    g6: LineSegment StartX=-118.877 StartY=36.5 StartZ=0 EndX=-119.137 EndY=35.7 EndZ=0
    g7: LineSegment StartX=-119.69 StartY=34 StartZ=0 EndX=-119.95 EndY=33.2 EndZ=0
  constraints (20):
    c: Coincident(g2,g0)
    c: Horizontal(g2)
    c: Coincident(g3,g0)
    c: Horizontal(g3)
    c: Coincident(g4,g1)
    c: Horizontal(g4)
    c: Coincident(g5,g1)
    c: Horizontal(g5)
    c: Coincident(g6,g2)
    c: Coincident(g6,g3)
    c: Coincident(g7,g4)
    c: Coincident(g7,g5)
    c: Tangent(g0,g-4)
    c: Tangent(g6,g-5)
    c: Tangent(g1,g-4)
    c: Tangent(g7,g-5)
    c: DistanceY(g3,g2) = 0.8
    c: DistanceY(g5,g4) = 0.8
    c: DistanceY(g-6,g1) = 2
    c: DistanceY(g-6,g0) = 4.5
FEATURE [PartDesign::Chamfer] Chamfer008
  Angle = 45
  Base = -> Pad018 [Edge257]
  BaseFeature = -> Pad018
  ChamferType = 1
  FlipDirection = false
  Refine = true
  Size = 1
  Size2 = 6
  SupportTransform = false
  Suppressed = false
  UseAllEdges = false
FEATURE [PartDesign::Pocket] Pocket010
  BaseFeature = -> Chamfer008
  Direction = (0,1,-2e-16)
  Length = 1
  Length2 = 5
  Profile = -> Sketch126
  ReferenceAxis = -> Sketch126 [N_Axis]
  Refine = true
  Suppressed = false
  Type = 0
FEATURE [PartDesign::Pad] Pad015
  BaseFeature = -> Pocket010
  Direction = (0,-1,2e-16)
  Length = 2
  Length2 = 10
  Profile = -> Sketch121
  ReferenceAxis = -> Sketch121 [N_Axis]
  Refine = true
  Suppressed = false
  Type = 0
FEATURE [PartDesign::Pad] Pad016
  BaseFeature = -> Pad015
  Direction = (0,-1,2e-16)
  Length = 1.6
  Length2 = 10
  Profile = -> Sketch122
  ReferenceAxis = -> Sketch122 [N_Axis]
  Refine = true
  Suppressed = false
  Type = 0
FEATURE [Sketcher::SketchObject] Sketch127
  ArcFitTolerance = 1e-06
  AttachmentSupport = -> [Pad016]
  ExternalGeometry = -> [Pad016]
  FullyConstrained = true
  MakeInternals = false
  MapMode = 5
  Placement = pos=(0,0,-80.4316) rot=(1,0,0;3.14159rad)
  sketch-geometry (8):
    g0: LineSegment StartX=-176.685 StartY=3.6 StartZ=0 EndX=-186.685 EndY=3.6 EndZ=0
    g1: LineSegment [constr] StartX=-186.685 StartY=3.6 StartZ=0 EndX=-186.685 EndY=-9e-16 EndZ=0
    g2: LineSegment StartX=-176.685 StartY=3.6 StartZ=0 EndX=-176.685 EndY=0 EndZ=0
    g3: ArcOfEllipse CenterX=-186.685 CenterY=-9e-16 CenterZ=0 NormalX=0 NormalY=0 NormalZ=1 MajorRadius=10 MinorRadius=3.6 AngleXU=1e-16 StartAngle=0 EndAngle=1.5708
    g4: LineSegment [constr] StartX=-176.685 StartY=-2e-15 StartZ=0 EndX=-196.685 EndY=-2e-15 EndZ=0
    g5: LineSegment [constr] StartX=-186.685 StartY=3.6 StartZ=0 EndX=-186.685 EndY=-3.6 EndZ=0
    g6: GeomPoint [constr] X=-177.356 Y=0 Z=0
    g7: GeomPoint [constr] X=-196.015 Y=-1.9e-15 Z=0
  constraints (13):
    c: Coincident(g0,g-4)
    c: PointOnObject(g0,g-4)
    c: DistanceX(g0,g0) = 10
    c: Coincident(g1,g0)
    c: PointOnObject(g1,g-5)
    c: Vertical(g1)
    c: Coincident(g2,g0)
    c: Coincident(g2,g-5)
    c: InternalAlignment(g4-g7 -> g3) x4
    c: Coincident(g3,g1)
    c: Coincident(g3,g0)
    c: Coincident(g3,g2)
    c: Horizontal(g4)
FEATURE [Sketcher::SketchObject] Sketch128
  ArcFitTolerance = 1e-06
  AttachmentSupport = -> [Pad016]
  ExternalGeometry = -> [Pad016]
  FullyConstrained = true
  MakeInternals = false
  MapMode = 5
  Placement = pos=(0,0,-80.4316) rot=(1,0,0;3.14159rad)
  sketch-geometry (8):
    g0: LineSegment StartX=-215.932 StartY=3.6 StartZ=0 EndX=-215.932 EndY=-1.3e-15 EndZ=0
    g1: LineSegment StartX=-215.932 StartY=3.6 StartZ=0 EndX=-205.932 EndY=3.6 EndZ=0
    g2: LineSegment [constr] StartX=-205.932 StartY=3.6 StartZ=0 EndX=-205.932 EndY=-9e-16 EndZ=0
    g3: ArcOfEllipse CenterX=-205.932 CenterY=-9e-16 CenterZ=0 NormalX=0 NormalY=0 NormalZ=1 MajorRadius=10 MinorRadius=3.6 AngleXU=-3.14159 StartAngle=4.71239 EndAngle=6.28319
    g4: LineSegment [constr] StartX=-215.932 StartY=-1e-15 StartZ=0 EndX=-195.932 EndY=-1e-15 EndZ=0
    g5: LineSegment [constr] StartX=-205.932 StartY=-3.6 StartZ=0 EndX=-205.932 EndY=3.6 EndZ=0
    g6: GeomPoint [constr] X=-215.262 Y=-2e-15 Z=0
    g7: GeomPoint [constr] X=-196.602 Y=-1e-15 Z=0
  constraints (13):
    c: Coincident(g0,g-4)
    c: Coincident(g0,g-5)
    c: Coincident(g1,g0)
    c: PointOnObject(g1,g-3)
    c: DistanceX(g1,g1) = 10
    c: Coincident(g2,g1)
    c: Vertical(g2)
    c: PointOnObject(g2,g-5)
    c: InternalAlignment(g4-g7 -> g3) x4
    c: Coincident(g3,g2)
    c: Coincident(g3,g1)
    c: Coincident(g3,g0)
    c: Horizontal(g4)
FEATURE [PartDesign::SubtractivePipe] SubtractivePipe002
  AuxilleryCurvelinear = true
  AuxillerySpineTangent = false
  BaseFeature = -> Pad016
  Binormal = (0,0,0)
  Mode = 0
  Profile = -> Sketch127
  Refine = true
  Spine = -> Pad016 [Edge254]
  SpineTangent = false
  Suppressed = false
  Transformation = 0
  Transition = 0
FEATURE [PartDesign::SubtractivePipe] SubtractivePipe003
  AuxilleryCurvelinear = true
  AuxillerySpineTangent = false
  BaseFeature = -> SubtractivePipe002
  Binormal = (0,0,0)
  Mode = 0
  Profile = -> Sketch128
  Refine = true
  Spine = -> Pad016 [Edge256,Edge251,Edge252]
  SpineTangent = false
  Suppressed = false
  Transformation = 0
  Transition = 0
FEATURE [Sketcher::SketchObject] Sketch129
  ArcFitTolerance = 1e-06
  AttachmentSupport = -> [Pad016]
  ExternalGeometry = -> [Binder001]
  FullyConstrained = true
  MakeInternals = false
  MapMode = 5
  Placement = pos=(0,-3.6,0) rot=(1,0,0;1.5708rad)
  sketch-geometry (12):
    g0: LineSegment [constr] StartX=-192.176 StartY=-3.18451 StartZ=0 EndX=-181.223 EndY=20.303 EndZ=0
    g1: LineSegment [constr] StartX=-202.765 StartY=20.303 StartZ=0 EndX=-181.223 EndY=20.303 EndZ=0
    g2: LineSegment StartX=-202.765 StartY=20.303 StartZ=0 EndX=-181.223 EndY=20.303 EndZ=0
    g3: LineSegment StartX=-192.176 StartY=-3.18451 StartZ=0 EndX=-196.804 EndY=-13.1107 EndZ=0
    g4: ArcOfCircle CenterX=-207.583 CenterY=4 CenterZ=0 NormalX=0 NormalY=0 NormalZ=1 AngleXU=0 Radius=17 StartAngle=5.84685 EndAngle=7.56663
    g5: ArcOfEllipse CenterX=-181.223 CenterY=8.55923 CenterZ=0 NormalX=0 NormalY=0 NormalZ=1 MajorRadius=23.4779 MinorRadius=11.7437 AngleXU=2e-16 StartAngle=4.71239 EndAngle=7.85398
    g6: LineSegment [constr] StartX=-157.745 StartY=8.55923 StartZ=0 EndX=-204.701 EndY=8.55923 EndZ=0
    g7: LineSegment [constr] StartX=-181.223 StartY=20.303 StartZ=0 EndX=-181.223 EndY=-3.18451 EndZ=0
    g8: GeomPoint [constr] X=-160.894 Y=8.55923 Z=0
    g9: GeomPoint [constr] X=-201.553 Y=8.55923 Z=0
    g10: ArcOfCircle CenterX=-181.223 CenterY=-20.3763 CenterZ=0 NormalX=0 NormalY=0 NormalZ=1 AngleXU=0 Radius=17.1918 StartAngle=1.57079 EndAngle=2.70526
    g11: GeomPoint [constr] X=-181.223 Y=-3.18451 Z=0
  constraints (23):
    c: Coincident(g0,g-5)
    c: Coincident(g1,g-6)
    c: Horizontal(g1)
    c: Coincident(g1,g0)
    c: Parallel(g0,g-4)
    c: Coincident(g2,g1)
    c: Coincident(g2,g0)
    c: Coincident(g3,g0)
    c: Equal(g4,g-5)
    c: Coincident(g4,g1)
    c: Coincident(g4,g0)
    c: InternalAlignment(g6-g9 -> g5) x4
    c: Vertical(g5,g0)
    c: Horizontal(g6)
    c: Coincident(g5,g0)
    c: DistanceX(g6,g-3) = 10.1
    c: Tangent(g10,g3) = -1.5708
    c: PointOnObject(g11,g10)
    c: Tangent(g5,g10,g11) = 1.5708
    c: Coincident(g10,g5)
    c: Coincident(g11,g7)
    c: Parallel(g3,g-4)
    c: Horizontal(g5,g0)
FEATURE [Sketcher::SketchObject] Sketch130
  ArcFitTolerance = 1e-06
  AttachmentOffset = pos=(0,0,-1.6) rot=(0,0,1;0rad)
  AttachmentSupport = -> [Pad016]
  ExternalGeometry = -> [Binder001]
  FullyConstrained = true
  MakeInternals = false
  MapMode = 5
  Placement = pos=(0,-2,-4e-16) rot=(1,0,0;1.5708rad)
  sketch-geometry (12):
    g0: LineSegment [constr] StartX=-192.176 StartY=-3.18451 StartZ=0 EndX=-181.223 EndY=20.303 EndZ=0
    g1: LineSegment [constr] StartX=-202.765 StartY=20.303 StartZ=0 EndX=-181.223 EndY=20.303 EndZ=0
    g2: LineSegment StartX=-202.765 StartY=20.303 StartZ=0 EndX=-181.223 EndY=20.303 EndZ=0
    g3: LineSegment StartX=-192.176 StartY=-3.18451 StartZ=0 EndX=-193.827 EndY=-6.72678 EndZ=0
    g4: ArcOfCircle CenterX=-207.583 CenterY=4 CenterZ=0 NormalX=0 NormalY=0 NormalZ=1 AngleXU=0 Radius=17 StartAngle=5.84685 EndAngle=7.56663
    g5: ArcOfEllipse CenterX=-181.223 CenterY=10.803 CenterZ=0 NormalX=0 NormalY=0 NormalZ=1 MajorRadius=14.4779 MinorRadius=9.5 AngleXU=0 StartAngle=4.71239 EndAngle=7.85398
    g6: LineSegment [constr] StartX=-166.745 StartY=10.803 StartZ=0 EndX=-195.701 EndY=10.803 EndZ=0
    g7: LineSegment [constr] StartX=-181.223 StartY=20.303 StartZ=0 EndX=-181.223 EndY=1.30297 EndZ=0
    g8: GeomPoint [constr] X=-170.298 Y=10.803 Z=0
    g9: GeomPoint [constr] X=-192.148 Y=10.803 Z=0
    g10: ArcOfCircle CenterX=-181.223 CenterY=-12.6042 CenterZ=0 NormalX=0 NormalY=0 NormalZ=1 AngleXU=0 Radius=13.9072 StartAngle=1.5708 EndAngle=2.70526
    g11: GeomPoint [constr] X=-181.223 Y=1.30297 Z=0
  constraints (23):
    c: Coincident(g0,g-5)
    c: Coincident(g1,g-6)
    c: Horizontal(g1)
    c: Coincident(g1,g0)
    c: Parallel(g0,g-4)
    c: Coincident(g2,g1)
    c: Coincident(g2,g0)
    c: Coincident(g3,g0)
    c: Equal(g4,g-5)
    c: Coincident(g4,g1)
    c: Coincident(g4,g0)
    c: InternalAlignment(g6-g9 -> g5) x4
    c: Vertical(g5,g0)
    c: Horizontal(g6)
    c: Coincident(g5,g0)
    c: DistanceX(g6,g-3) = 19.1
    c: Tangent(g10,g3) = -1.5708
    c: PointOnObject(g11,g10)
    c: Tangent(g5,g10,g11) = 1.5708
    c: Coincident(g10,g5)
    c: Coincident(g11,g7)
    c: Parallel(g3,g-4)
    c: DistanceY(g5,g0) = 19
FEATURE [Part::Part2DObjectPython] Clone2D001  label="Sketch130 (2D)"  # Draft 2D object (typed FeaturePython)
  Fuse = false
  Objects = -> [Sketch130]
  Placement = pos=(0,-2,-4e-16) rot=(1,0,0;1.5708rad)
  Scale = (1,1,1)
FEATURE [Sketcher::SketchObject] Sketch131
  ArcFitTolerance = 1e-06
  AttachmentOffset = pos=(0,0,-3.5) rot=(0,0,1;0rad)
  AttachmentSupport = -> [Pad016]
  ExternalGeometry = -> [Binder001]
  FullyConstrained = true
  MakeInternals = false
  MapMode = 5
  Placement = pos=(0,-0.1,-8e-16) rot=(1,0,0;1.5708rad)
  sketch-geometry (1):
    g0: GeomPoint X=-197.47 Y=8.55923 Z=0
  constraints (1):
    c: Symmetric(g-6,g-4,g0)
FEATURE [PartDesign::SubtractiveLoft] SubtractiveLoft002
  BaseFeature = -> SubtractivePipe003
  Closed = false
  Profile = -> Sketch129
  Refine = true
  Ruled = false
  Sections = -> [Sketch130]
  Suppressed = false
FEATURE [PartDesign::SubtractiveLoft] SubtractiveLoft003
  BaseFeature = -> SubtractiveLoft002
  Closed = false
  Profile = -> Clone2D001
  Refine = true
  Ruled = false
  Sections = -> [Sketch131]
  Suppressed = false
FEATURE [PartDesign::Chamfer] Chamfer010
  Angle = 45
  Base = -> SubtractiveLoft003 [Edge200,Edge201,Edge203,Edge202,Edge194]
  BaseFeature = -> SubtractiveLoft003
  ChamferType = 0
  FlipDirection = false
  Refine = true
  Size = 1.5
  Size2 = 1
  SupportTransform = false
  Suppressed = false
  UseAllEdges = false
FEATURE [PartDesign::Chamfer] Chamfer011
  Angle = 45
  Base = -> Chamfer010 [Edge15]
  BaseFeature = -> Chamfer010
  ChamferType = 0
  FlipDirection = false
  Refine = true
  Size = 1.6
  Size2 = 1
  SupportTransform = false
  Suppressed = false
  UseAllEdges = false
FEATURE [PartDesign::Chamfer] Chamfer012
  Angle = 45
  Base = -> Chamfer011 [Edge10]
  BaseFeature = -> Chamfer011
  ChamferType = 0
  FlipDirection = false
  Refine = true
  Size = 3.5
  Size2 = 1
  SupportTransform = false
  Suppressed = false
  UseAllEdges = false
FEATURE [PartDesign::Chamfer] Chamfer013
  Angle = 45
  Base = -> Chamfer012 [Edge145,Edge94]
  BaseFeature = -> Chamfer012
  ChamferType = 0
  FlipDirection = false
  Refine = true
  Size = 1.9
  Size2 = 1
  SupportTransform = false
  Suppressed = false
  UseAllEdges = false
FEATURE [Sketcher::SketchObject] Sketch132
  ArcFitTolerance = 1e-06
  AttachmentSupport = -> [Pad016]
  ExternalGeometry = -> [Binder001]
  FullyConstrained = true
  MakeInternals = false
  MapMode = 5
  Placement = pos=(0,-3.6,0) rot=(1,0,0;1.5708rad)
  sketch-geometry (3):
    g0: LineSegment [constr] StartX=-215.42 StartY=-53.0314 StartZ=0 EndX=-167.782 EndY=-53.0314 EndZ=0
    g1: Circle CenterX=-191.282 CenterY=-53.0314 CenterZ=0 NormalX=0 NormalY=0 NormalZ=1 AngleXU=0 Radius=11.5
    g2: Circle CenterX=-191.282 CenterY=-53.0314 CenterZ=0 NormalX=0 NormalY=0 NormalZ=1 AngleXU=0 Radius=10.7
  constraints (8):
    c: Coincident(g0,g-3)
    c: PointOnObject(g0,g-4)
    c: Horizontal(g0)
    c: Diameter(g1) = 23
    c: PointOnObject(g1,g0)
    c: DistanceX(g1,g0) = 23.5
    c: Diameter(g2) = 21.4
    c: Coincident(g2,g1)
FEATURE [PartDesign::Fillet] Fillet007
  Base = -> Chamfer013 [Edge83]
  BaseFeature = -> Chamfer013
  Radius = 1.1
  Refine = true
  SupportTransform = false
  Suppressed = false
  UseAllEdges = false
FEATURE [PartDesign::Fillet] Fillet008
  Base = -> Fillet007 [Edge76]
  BaseFeature = -> Fillet007
  Radius = 1.9
  Refine = true
  SupportTransform = false
  Suppressed = false
  UseAllEdges = false
FEATURE [PartDesign::Pocket] Pocket011
  BaseFeature = -> Fillet008
  Direction = (0,1,-2e-16)
  Length = 0.8
  Length2 = 5
  Profile = -> Sketch132
  ReferenceAxis = -> Sketch132 [N_Axis]
  Refine = true
  Suppressed = false
  Type = 0
FEATURE [Part::Part2DObjectPython] ShapeString  # Draft 2D object (typed FeaturePython)
  FontFile = <path>
  Fuse = false
  Justification = 6
  JustificationReference = 0
  KeepLeftMargin = false
  MakeFace = true
  ObliqueAngle = 0
  Placement = pos=(-199,-3.6,-57.5) rot=(1,0,0;1.5708rad)
  ScaleToSize = true
  Size = 10
  String = AS
  Tracking = 0
FEATURE [PartDesign::Pocket] Pocket012
  BaseFeature = -> Pocket011
  Direction = (0,1,0)
  Length = 1
  Length2 = 5
  Profile = -> ShapeString
  ReferenceAxis = -> ShapeString [N_Axis]
  Refine = true
  Suppressed = false
  Type = 0
FEATURE [PartDesign::Body] Body007  label="lato DX"
  AllowCompound = false
  Group = -> [Binder001,Sketch114,Pad011,Chamfer014,Sketch115,Pocket006,Sketch116,Pad012,Sketch117,Pocket007,Sketch118,Pad013,Sketch119,Pocket008,Pad017,Chamfer009,Pocket009,Sketch123,Sketch120,Pad014,Pad018,Chamfer008,Pocket010,Sketch121,Pad015,Sketch122,Pad016,Sketch124,Sketch125,Sketch126,Sketch127,Sketch128,SubtractivePipe002,SubtractivePipe003,Sketch129,Sketch130,Clone2D001,Sketch131,SubtractiveLoft002,+11 more]
  Origin = -> Origin007
  Tip = -> Pocket012
FEATURE [Sketcher::SketchObject] Sketch133
  ArcFitTolerance = 1e-06
  AttachmentSupport = -> [Binder]
  ExternalGeometry = -> [Binder]
  FullyConstrained = true
  MakeInternals = false
  MapMode = 5
  Placement = pos=(0,9e-16,0) rot=(0,0.707107,0.707107;3.14159rad)
  sketch-geometry (30):
    g0: LineSegment StartX=0 StartY=39.2 StartZ=0 EndX=0 EndY=3.2 EndZ=0
    g1: LineSegment StartX=0 StartY=3.2 StartZ=0 EndX=82.8 EndY=3.2 EndZ=0
    g2: LineSegment StartX=82.8 StartY=3.2 StartZ=0 EndX=82.8 EndY=6.2 EndZ=0
    g3: LineSegment StartX=82.8 StartY=6.2 StartZ=0 EndX=91.752 EndY=6.2 EndZ=0
    g4: LineSegment StartX=0 StartY=39.2 StartZ=0 EndX=195.887 EndY=39.2 EndZ=0
    g5: LineSegment StartX=195.887 StartY=39.2 StartZ=0 EndX=202.765 EndY=20.303 EndZ=0
    g6: LineSegment StartX=192.333 StartY=24.9893 StartZ=0 EndX=196.467 EndY=26.4942 EndZ=0
    g7: LineSegment StartX=196.467 StartY=26.4942 StartZ=0 EndX=194.073 EndY=33.0721 EndZ=0
    g8: LineSegment StartX=194.073 StartY=33.0721 StartZ=0 EndX=189.939 EndY=31.5672 EndZ=0
    g9: LineSegment StartX=189.939 StartY=31.5672 StartZ=0 EndX=192.333 EndY=24.9893 EndZ=0
    g10: ArcOfCircle CenterX=107.6 CenterY=4 CenterZ=0 NormalX=0 NormalY=0 NormalZ=1 AngleXU=0 Radius=16 StartAngle=1.5708 EndAngle=3.00366
    g11: LineSegment StartX=107.6 StartY=20 StartZ=0 EndX=132.428 EndY=20 EndZ=0
    g12: ArcOfCircle [constr] CenterX=132.428 CenterY=4 CenterZ=0 NormalX=0 NormalY=0 NormalZ=1 AngleXU=0 Radius=16 StartAngle=0.314159 EndAngle=1.5708
    g13: LineSegment StartX=147.645 StartY=8.94427 StartZ=0 EndX=176.685 EndY=-80.4316 EndZ=0
    g14: LineSegment StartX=176.685 StartY=-80.4316 StartZ=0 EndX=215.932 EndY=-80.4316 EndZ=0
    g15: ArcOfCircle CenterX=207.583 CenterY=4 CenterZ=0 NormalX=0 NormalY=0 NormalZ=1 AngleXU=0 Radius=17 StartAngle=1.85815 EndAngle=3.57792
    g16: ArcOfCircle CenterX=184.801 CenterY=-67.3089 CenterZ=0 NormalX=0 NormalY=0 NormalZ=1 AngleXU=0 Radius=33.7833 StartAngle=5.88425 EndAngle=6.71952
    g17: LineSegment StartX=192.176 StartY=-3.18451 StartZ=0 EndX=215.42 EndY=-53.0314 EndZ=0
    g18: Circle CenterX=5.6 CenterY=34.8 CenterZ=0 NormalX=0 NormalY=0 NormalZ=1 AngleXU=0 Radius=1.8
    g19: Circle CenterX=5.6 CenterY=7.6 CenterZ=0 NormalX=0 NormalY=0 NormalZ=1 AngleXU=0 Radius=1.8
    g20: Circle CenterX=78.51 CenterY=34.8 CenterZ=0 NormalX=0 NormalY=0 NormalZ=1 AngleXU=0 Radius=1.8
    g21: Circle CenterX=78.51 CenterY=7.6 CenterZ=0 NormalX=0 NormalY=0 NormalZ=1 AngleXU=0 Radius=1.8
    g22: Circle CenterX=184.08 CenterY=34.8 CenterZ=0 NormalX=0 NormalY=0 NormalZ=1 AngleXU=0 Radius=1.8
    g23: Circle CenterX=179.305 CenterY=-76.8316 CenterZ=0 NormalX=0 NormalY=0 NormalZ=1 AngleXU=0 Radius=1.8
    g24: Circle CenterX=213.443 CenterY=-76.8316 CenterZ=0 NormalX=0 NormalY=0 NormalZ=1 AngleXU=0 Radius=1.8
    g25: Circle CenterX=19 CenterY=21.2 CenterZ=0 NormalX=0 NormalY=0 NormalZ=1 AngleXU=0 Radius=6.3
    g26: Circle CenterX=42 CenterY=21.2 CenterZ=0 NormalX=0 NormalY=0 NormalZ=1 AngleXU=0 Radius=6.3
    g27: Circle CenterX=65 CenterY=21.2 CenterZ=0 NormalX=0 NormalY=0 NormalZ=1 AngleXU=0 Radius=6.3
    g28: LineSegment StartX=132.428 StartY=20 StartZ=0 EndX=144.053 EndY=20 EndZ=0
    g29: LineSegment StartX=147.645 StartY=8.94427 StartZ=0 EndX=144.053 EndY=20 EndZ=0
  constraints (65):
    c: Coincident(g0,g-4)
    c: Coincident(g0,g-5)
    c: Coincident(g1,g0)
    c: Coincident(g1,g-6)
    c: Coincident(g2,g1)
    c: Coincident(g2,g-7)
    c: Coincident(g3,g2)
    c: Coincident(g3,g-8)
    c: Coincident(g4,g0)
    c: Coincident(g4,g-16)
    c: Coincident(g5,g4)
    c: Coincident(g5,g-16)
    c: Coincident(g6,g-20)
    c: Coincident(g6,g-21)
    c: Coincident(g7,g6)
    c: Coincident(g7,g-23)
    c: Coincident(g8,g7)
    c: Coincident(g8,g-22)
    c: Coincident(g9,g8)
    c: Coincident(g9,g6)
    c: Equal(g10,g-8)
    c: Coincident(g10,g3)
    c: Coincident(g10,g-9)
    c: Coincident(g11,g10)
    c: Coincident(g11,g-10)
    c: Equal(g12,g-10)
    c: Coincident(g12,g11)
    c: Coincident(g12,g-11)
    c: Coincident(g13,g12)
    c: Coincident(g13,g-12)
    c: Coincident(g14,g13)
    c: Coincident(g14,g-13)
    c: Equal(g15,g-15)
    c: Coincident(g15,g5)
    c: Coincident(g15,g-15)
    c: Equal(g16,g-13)
    c: Coincident(g16,g14)
    c: Coincident(g16,g-14)
    c: Coincident(g17,g15)
    c: Coincident(g17,g16)
    c: Equal(g18,g-28)
    c: Equal(g19,g-29)
    c: Equal(g20,g-26)
    c: Equal(g21,g-27)
    c: Equal(g22,g-17)
    c: Equal(g24,g-25)
    c: Equal(g23,g-24)
    c: Coincident(g23,g-24)
    c: Coincident(g24,g-25)
    c: Coincident(g22,g-17)
    c: Coincident(g20,g-26)
    c: Coincident(g21,g-27)
    c: Coincident(g18,g-28)
    c: Coincident(g19,g-29)
    c: Equal(g25,g-30)
    c: Equal(g26,g-31)
    c: Equal(g27,g-32)
    c: Coincident(g25,g-30)
    c: Coincident(g26,g-31)
    c: Coincident(g27,g-32)
    c: Parallel(g28,g11)
    c: Parallel(g29,g13)
    c: Coincident(g28,g11)
    c: Coincident(g29,g12)
    c: Coincident(g29,g28)
FEATURE [PartDesign::Pad] Pad019
  Direction = (0,1,-2e-16)
  Length = 2
  Length2 = 10
  Profile = -> Sketch133
  ReferenceAxis = -> Sketch133 [N_Axis]
  Refine = true
  Suppressed = false
  Type = 0
FEATURE [Sketcher::SketchObject] Sketch091  label="Sketch091 - forma anteriore"
  ArcFitTolerance = 1e-06
  AttachmentSupport = -> [Pad019]
  ExternalGeometry = -> [Binder]
  FullyConstrained = true
  MakeInternals = false
  MapMode = 5
  Placement = pos=(0,2,0) rot=(0,0.707107,0.707107;3.14159rad)
  sketch-geometry (12):
    g0: Circle CenterX=5.6 CenterY=34.8 CenterZ=0 NormalX=0 NormalY=0 NormalZ=1 AngleXU=0 Radius=1.8
    g1: Circle CenterX=5.6 CenterY=7.6 CenterZ=0 NormalX=0 NormalY=0 NormalZ=1 AngleXU=0 Radius=1.8
    g2: Circle CenterX=78.51 CenterY=34.8 CenterZ=0 NormalX=0 NormalY=0 NormalZ=1 AngleXU=0 Radius=1.8
    g3: Circle CenterX=78.51 CenterY=7.6 CenterZ=0 NormalX=0 NormalY=0 NormalZ=1 AngleXU=0 Radius=1.8
    g4: LineSegment StartX=0 StartY=39.2 StartZ=0 EndX=0 EndY=3.2 EndZ=0
    g5: LineSegment StartX=0 StartY=3.2 StartZ=0 EndX=82.8 EndY=3.2 EndZ=0
    g6: LineSegment StartX=82.8 StartY=3.2 StartZ=0 EndX=82.8 EndY=39.2 EndZ=0
    g7: LineSegment StartX=82.8 StartY=39.2 StartZ=0 EndX=0 EndY=39.2 EndZ=0
    g8: ArcOfCircle CenterX=19 CenterY=21.2 CenterZ=0 NormalX=0 NormalY=0 NormalZ=1 AngleXU=0 Radius=10 StartAngle=1.5708 EndAngle=4.71239
    g9: ArcOfCircle CenterX=65 CenterY=21.2 CenterZ=0 NormalX=0 NormalY=0 NormalZ=1 AngleXU=0 Radius=10 StartAngle=4.71239 EndAngle=7.85398
    g10: LineSegment StartX=19 StartY=31.2 StartZ=0 EndX=65 EndY=31.2 EndZ=0
    g11: LineSegment StartX=19 StartY=11.2 StartZ=0 EndX=65 EndY=11.2 EndZ=0
  constraints (25):
    c: Equal(g2,g-7)
    c: Equal(g3,g-8)
    c: Equal(g1,g-13)
    c: Equal(g0,g-12)
    c: Coincident(g0,g-12)
    c: Coincident(g1,g-13)
    c: Coincident(g3,g-8)
    c: Coincident(g2,g-7)
    c: Coincident(g4,g-4)
    c: Coincident(g4,g-5)
    c: Coincident(g5,g4)
    c: Coincident(g5,g-6)
    c: Coincident(g6,g5)
    c: PointOnObject(g6,g-3)
    c: Vertical(g6)
    c: Coincident(g7,g6)
    c: Coincident(g7,g4)
    c: Tangent(g8,g10) = 1.5708
    c: Tangent(g8,g11) = -1.5708
    c: Tangent(g9,g10) = 1.5708
    c: Tangent(g9,g11) = -1.5708
    c: Equal(g8,g9)
    c: Radius(g8) = 10
    c: Coincident(g8,g-11)
    c: Coincident(g9,g-9)
FEATURE [Sketcher::SketchObject] Sketch093  label="Sketch093 - scavi interni pulsanti"
  ArcFitTolerance = 1e-06
  AttachmentSupport = -> [Pad019]
  ExternalGeometry = -> [Binder]
  FullyConstrained = true
  MakeInternals = false
  MapMode = 5
  Placement = pos=(0,1.8e-15,0) rot=(1,0,0;1.5708rad)
  sketch-geometry (3):
    g0: Circle CenterX=-65 CenterY=21.2 CenterZ=0 NormalX=0 NormalY=0 NormalZ=1 AngleXU=0 Radius=7.3
    g1: Circle CenterX=-42 CenterY=21.2 CenterZ=0 NormalX=0 NormalY=0 NormalZ=1 AngleXU=0 Radius=7.3
    g2: Circle CenterX=-19 CenterY=21.2 CenterZ=0 NormalX=0 NormalY=0 NormalZ=1 AngleXU=0 Radius=7.3
  constraints (6):
    c: Coincident(g0,g-3)
    c: Coincident(g1,g-4)
    c: Coincident(g2,g-5)
    c: Diameter(g0) = 14.6
    c: Diameter(g1) = 14.6
    c: Diameter(g2) = 14.6
FEATURE [Sketcher::SketchObject] Sketch094  label="Sketch094 - forma centrale"
  ArcFitTolerance = 1e-06
  AttachmentSupport = -> [Pad019]
  ExternalGeometry = -> [Binder]
  FullyConstrained = true
  MakeInternals = false
  MapMode = 5
  Placement = pos=(0,2,0) rot=(0,0.707107,0.707107;3.14159rad)
  sketch-geometry (4):
    g0: LineSegment StartX=137.815 StartY=39.2 StartZ=0 EndX=142.655 EndY=24.303 EndZ=0
    g1: LineSegment StartX=110.815 StartY=24.303 StartZ=0 EndX=142.655 EndY=24.303 EndZ=0
    g2: LineSegment StartX=137.815 StartY=39.2 StartZ=0 EndX=110.815 EndY=39.2 EndZ=0
    g3: ArcOfCircle CenterX=92.2534 CenterY=31.7515 CenterZ=0 NormalX=0 NormalY=0 NormalZ=1 AngleXU=0 Radius=20 StartAngle=5.90156 EndAngle=6.66481
  constraints (12):
    c: PointOnObject(g0,g-3)
    c: Tangent(g0,g-5)
    c: Horizontal(g1)
    c: Coincident(g1,g0)
    c: Coincident(g2,g0)
    c: PointOnObject(g2,g-3)
    c: DistanceX(g2,g2) = 27
    c: Vertical(g1,g2)
    c: Coincident(g3,g2)
    c: Radius(g3) = 20
    c: Coincident(g3,g1)
    c: DistanceY(g-6,g0) = 4
FEATURE [Sketcher::SketchObject] Sketch095  label="Sketch095 - forma posteriore"
  ArcFitTolerance = 1e-06
  AttachmentSupport = -> [Pad019]
  ExternalGeometry = -> [Binder]
  FullyConstrained = true
  MakeInternals = false
  MapMode = 5
  Placement = pos=(0,2,0) rot=(0,0.707107,0.707107;3.14159rad)
  sketch-geometry (15):
    g0: LineSegment StartX=137.815 StartY=39.2 StartZ=0 EndX=143.955 EndY=20.303 EndZ=0
    g1: LineSegment StartX=143.955 StartY=20.303 StartZ=0 EndX=190.141 EndY=20.303 EndZ=0
    g2: ArcOfCircle CenterX=184.08 CenterY=34.8 CenterZ=0 NormalX=0 NormalY=0 NormalZ=1 AngleXU=0 Radius=3.5 StartAngle=3.49066 EndAngle=4.71239
    g3: LineSegment StartX=180.791 StartY=33.6029 StartZ=0 EndX=178.754 EndY=39.2 EndZ=0
    g4: LineSegment StartX=184.08 StartY=31.3 StartZ=0 EndX=186.139 EndY=31.3 EndZ=0
    g5: LineSegment StartX=190.141 StartY=20.303 StartZ=0 EndX=186.139 EndY=31.3 EndZ=0
    g6: LineSegment StartX=137.815 StartY=39.2 StartZ=0 EndX=156.815 EndY=39.2 EndZ=0
    g7: LineSegment StartX=178.754 StartY=39.2 StartZ=0 EndX=168.815 EndY=39.2 EndZ=0
    g8: LineSegment StartX=156.815 StartY=31.2 StartZ=0 EndX=168.815 EndY=31.2 EndZ=0
    g9: ArcOfCircle CenterX=176.411 CenterY=35.2 CenterZ=0 NormalX=0 NormalY=0 NormalZ=1 AngleXU=0 Radius=20 StartAngle=2.94023 EndAngle=3.34295
    g10: ArcOfCircle CenterX=188.411 CenterY=35.2 CenterZ=0 NormalX=0 NormalY=0 NormalZ=1 AngleXU=0 Radius=20 StartAngle=2.94023 EndAngle=3.34295
    g11: LineSegment StartX=157.815 StartY=39.2 StartZ=0 EndX=167.815 EndY=39.2 EndZ=0
    g12: LineSegment StartX=157.436 StartY=36.2 StartZ=0 EndX=167.436 EndY=36.2 EndZ=0
    g13: ArcOfCircle CenterX=177.411 CenterY=35.2 CenterZ=0 NormalX=0 NormalY=0 NormalZ=1 AngleXU=0 Radius=20 StartAngle=2.94023 EndAngle=3.09157
    g14: ArcOfCircle CenterX=187.411 CenterY=35.2 CenterZ=0 NormalX=0 NormalY=0 NormalZ=1 AngleXU=0 Radius=20 StartAngle=2.94023 EndAngle=3.09157
  constraints (46):
    c: PointOnObject(g0,g-3)
    c: Tangent(g0,g-6)
    c: Coincident(g1,g0)
    c: Horizontal(g1)
    c: Radius(g2) = 3.5
    c: Coincident(g2,g-5)
    c: PointOnObject(g3,g-3)
    c: Parallel(g3,g-4)
    c: Tangent(g3,g2) = 1.5708
    c: Horizontal(g4)
    c: Tangent(g4,g2) = -1.5708
    c: Coincident(g5,g1)
    c: Parallel(g5,g-4)
    c: Coincident(g5,g4)
    c: DistanceX(g4,g-8) = 3.8
    c: Coincident(g6,g0)
    c: PointOnObject(g6,g-3)
    c: Coincident(g7,g3)
    c: PointOnObject(g7,g-3)
    c: Horizontal(g8)
    c: DistanceX(g6,g7) = 12
    c: Vertical(g8,g6)
    c: Vertical(g7,g8)
    c: DistanceY(g8,g6) = 8
    c: Coincident(g9,g8)
    c: Coincident(g9,g6)
    c: Coincident(g10,g7)
    c: Coincident(g10,g8)
    c: Radius(g9) = 20
    c: Radius(g10) = 20
    c: PointOnObject(g11,g-3)
    c: PointOnObject(g11,g-3)
    c: DistanceX(g11,g11) = 10
    c: DistanceX(g6,g11) = 1
    c: Horizontal(g12)
    c: Equal(g12,g11)
    c: DistanceY(g12,g11) = 3
    c: Coincident(g13,g11)
    c: Coincident(g13,g12)
    c: Radius(g13) = 20
    c: Coincident(g14,g11)
    c: Coincident(g14,g12)
    c: Radius(g14) = 20
    c: DistanceX(g0,g6) = 19
    c: Horizontal(g9,g13)
    c: Horizontal(g0,g-4)
FEATURE [Sketcher::SketchObject] Sketch096  label="Sketch096 - forma impugnatura"
  ArcFitTolerance = 1e-06
  AttachmentSupport = -> [Pad019]
  ExternalGeometry = -> [Binder]
  FullyConstrained = true
  MakeInternals = false
  MapMode = 5
  Placement = pos=(0,2,0) rot=(0,0.707107,0.707107;3.14159rad)
  sketch-geometry (8):
    g0: LineSegment StartX=176.685 StartY=-80.4316 StartZ=0 EndX=143.955 EndY=20.303 EndZ=0
    g1: LineSegment StartX=176.685 StartY=-80.4316 StartZ=0 EndX=215.932 EndY=-80.4316 EndZ=0
    g2: Circle CenterX=179.305 CenterY=-76.8316 CenterZ=0 NormalX=0 NormalY=0 NormalZ=1 AngleXU=0 Radius=3
    g3: Circle CenterX=213.443 CenterY=-76.8316 CenterZ=0 NormalX=0 NormalY=0 NormalZ=1 AngleXU=0 Radius=3
    g4: LineSegment StartX=143.955 StartY=20.303 StartZ=0 EndX=202.765 EndY=20.303 EndZ=0
    g5: LineSegment StartX=215.42 StartY=-53.0314 StartZ=0 EndX=192.176 EndY=-3.18451 EndZ=0
    g6: ArcOfCircle CenterX=184.801 CenterY=-67.3089 CenterZ=0 NormalX=0 NormalY=0 NormalZ=1 AngleXU=0 Radius=33.7833 StartAngle=5.88425 EndAngle=6.71952
    g7: ArcOfCircle CenterX=207.583 CenterY=4 CenterZ=0 NormalX=0 NormalY=0 NormalZ=1 AngleXU=0 Radius=17 StartAngle=1.85815 EndAngle=3.57792
  constraints (19):
    c: Coincident(g0,g-4)
    c: PointOnObject(g0,g-3)
    c: Horizontal(g0,g-7)
    c: Coincident(g1,g0)
    c: Coincident(g1,g-5)
    c: Diameter(g2) = 6
    c: Diameter(g3) = 6
    c: Coincident(g2,g-9)
    c: Coincident(g3,g-10)
    c: Coincident(g4,g0)
    c: Coincident(g5,g-6)
    c: Coincident(g6,g1)
    c: Coincident(g6,g5)
    c: Equal(g-5,g6)
    c: Coincident(g5,g-7)
    c: Coincident(g4,g-7)
    c: Tangent(g7,g-7)
    c: Coincident(g7,g4)
    c: Coincident(g7,g5)
FEATURE [Sketcher::SketchObject] Sketch097
  ArcFitTolerance = 1e-06
  AttachmentSupport = -> [Pad019]
  ExternalGeometry = -> [Binder]
  FullyConstrained = true
  MakeInternals = false
  MapMode = 5
  Placement = pos=(0,2,0) rot=(0,0.707107,0.707107;3.14159rad)
  sketch-geometry (4):
    g0: LineSegment StartX=90 StartY=36.8 StartZ=0 EndX=108 EndY=36.8 EndZ=0
    g1: LineSegment StartX=108 StartY=36.8 StartZ=0 EndX=108 EndY=26.8 EndZ=0
    g2: LineSegment StartX=108 StartY=26.8 StartZ=0 EndX=90 EndY=26.8 EndZ=0
    g3: ArcOfCircle CenterX=94 CenterY=31.8 CenterZ=0 NormalX=0 NormalY=0 NormalZ=1 AngleXU=0 Radius=6.40312 StartAngle=2.24554 EndAngle=4.03765
  constraints (13):
    c: Horizontal(g0)
    c: Coincident(g1,g0)
    c: Vertical(g1)
    c: DistanceX(g0,g0) = 18
    c: DistanceY(g1,g1) = 10
    c: Coincident(g2,g1)
    c: Horizontal(g2)
    c: Equal(g2,g0)
    c: DistanceY(g0,g-3) = 2.4
    c: Coincident(g3,g0)
    c: Coincident(g3,g2)
    c: DistanceX(g2,g3) = 4
    c: DistanceX(g-3,g0) = 90
FEATURE [PartDesign::Chamfer] Chamfer015
  Angle = 45
  Base = -> Pad019 [Edge19,Edge22,Edge79]
  BaseFeature = -> Pad019
  ChamferType = 0
  FlipDirection = false
  Refine = true
  Size = 1.9
  Size2 = 1
  SupportTransform = false
  Suppressed = false
  UseAllEdges = false
FEATURE [PartDesign::Pocket] Pocket002
  BaseFeature = -> Chamfer015
  Direction = (0,1,-2e-16)
  Length = 1.2
  Length2 = 5
  Profile = -> Sketch093
  ReferenceAxis = -> Sketch093 [N_Axis]
  Refine = true
  Suppressed = false
  Type = 0
FEATURE [PartDesign::Pad] Pad005
  BaseFeature = -> Pocket002
  Direction = (0,1,-2e-16)
  Length = 1.6
  Length2 = 10
  Profile = -> Sketch091
  ReferenceAxis = -> Sketch091 [N_Axis]
  Refine = true
  Suppressed = false
  Type = 0
FEATURE [Sketcher::SketchObject] Sketch092  label="Sketch092 - scavi per viti anteriori"
  ArcFitTolerance = 1e-06
  AttachmentSupport = -> [Pad005]
  ExternalGeometry = -> [Binder]
  FullyConstrained = true
  MakeInternals = false
  MapMode = 5
  Placement = pos=(0,3.6,0) rot=(0,0.707107,0.707107;3.14159rad)
  sketch-geometry (20):
    g0: ArcOfCircle CenterX=5.6 CenterY=7.6 CenterZ=0 NormalX=0 NormalY=0 NormalZ=1 AngleXU=0 Radius=3.5 StartAngle=0 EndAngle=1.5708
    g1: ArcOfCircle CenterX=5.6 CenterY=34.8 CenterZ=0 NormalX=0 NormalY=0 NormalZ=1 AngleXU=0 Radius=3.5 StartAngle=4.71239 EndAngle=6.28319
    g2: ArcOfCircle CenterX=78.51 CenterY=34.8 CenterZ=0 NormalX=0 NormalY=0 NormalZ=1 AngleXU=0 Radius=3.5 StartAngle=3.14159 EndAngle=4.71239
    g3: ArcOfCircle CenterX=78.51 CenterY=7.6 CenterZ=0 NormalX=0 NormalY=0 NormalZ=1 AngleXU=0 Radius=3.5 StartAngle=1.5708 EndAngle=3.14159
    g4: LineSegment StartX=0 StartY=3.2 StartZ=0 EndX=0 EndY=11.1 EndZ=0
    g5: LineSegment StartX=0 StartY=11.1 StartZ=0 EndX=5.6 EndY=11.1 EndZ=0
    g6: LineSegment StartX=0 StartY=3.2 StartZ=0 EndX=9.1 EndY=3.2 EndZ=0
    g7: LineSegment StartX=9.1 StartY=3.2 StartZ=0 EndX=9.1 EndY=7.6 EndZ=0
    g8: LineSegment StartX=0 StartY=39.2 StartZ=0 EndX=0 EndY=31.3 EndZ=0
    g9: LineSegment StartX=0 StartY=31.3 StartZ=0 EndX=5.6 EndY=31.3 EndZ=0
    g10: LineSegment StartX=0 StartY=39.2 StartZ=0 EndX=9.1 EndY=39.2 EndZ=0
    g11: LineSegment StartX=9.1 StartY=39.2 StartZ=0 EndX=9.1 EndY=34.8 EndZ=0
    g12: LineSegment StartX=82.8 StartY=39.2 StartZ=0 EndX=75.01 EndY=39.2 EndZ=0
    g13: LineSegment StartX=82.8 StartY=39.2 StartZ=0 EndX=82.8 EndY=31.3 EndZ=0
    g14: LineSegment StartX=82.8 StartY=31.3 StartZ=0 EndX=78.51 EndY=31.3 EndZ=0
    g15: LineSegment StartX=82.8 StartY=3.2 StartZ=0 EndX=75.01 EndY=3.2 EndZ=0
    g16: LineSegment StartX=75.01 StartY=3.2 StartZ=0 EndX=75.01 EndY=7.6 EndZ=0
    g17: LineSegment StartX=82.8 StartY=3.2 StartZ=0 EndX=82.8 EndY=11.1 EndZ=0
    g18: LineSegment StartX=82.8 StartY=11.1 StartZ=0 EndX=78.51 EndY=11.1 EndZ=0
    g19: LineSegment StartX=75.01 StartY=39.2 StartZ=0 EndX=75.01 EndY=34.8 EndZ=0
  constraints (48):
    c: Radius(g0) = 3.5
    c: Coincident(g0,g-10)
    c: Radius(g1) = 3.5
    c: Coincident(g1,g-9)
    c: Radius(g2) = 3.5
    c: Coincident(g2,g-8)
    c: Radius(g3) = 3.5
    c: Coincident(g3,g-7)
    c: Coincident(g4,g-5)
    c: PointOnObject(g4,g-4)
    c: Coincident(g5,g4)
    c: Horizontal(g5)
    c: Coincident(g6,g4)
    c: PointOnObject(g6,g-5)
    c: Coincident(g7,g6)
    c: Vertical(g7)
    c: Coincident(g8,g-4)
    c: PointOnObject(g8,g-4)
    c: Coincident(g9,g8)
    c: Horizontal(g9)
    c: Coincident(g10,g8)
    c: PointOnObject(g10,g-3)
    c: Coincident(g11,g10)
    c: Vertical(g11)
    c: PointOnObject(g12,g-3)
    c: PointOnObject(g12,g-3)
    c: Coincident(g13,g12)
    c: Vertical(g13)
    c: Coincident(g14,g13)
    c: Horizontal(g14)
    c: Coincident(g15,g-6)
    c: PointOnObject(g15,g-5)
    c: Coincident(g16,g15)
    c: Vertical(g16)
    c: Coincident(g17,g15)
    c: Coincident(g18,g17)
    c: Horizontal(g18)
    c: Tangent(g3,g18) = -1.5708
    c: Tangent(g16,g3) = 1.5708
    c: Coincident(g19,g12)
    c: Vertical(g19)
    c: Tangent(g2,g19) = -1.5708
    c: Tangent(g2,g14) = 1.5708
    c: Tangent(g0,g7) = -1.5708
    c: Tangent(g0,g5) = 1.5708
    c: Tangent(g9,g1) = -1.5708
    c: Tangent(g1,g11) = 1.5708
    c: Tangent(g17,g13)
FEATURE [PartDesign::Pocket] Pocket001
  BaseFeature = -> Pad005
  Direction = (0,-1,2e-16)
  Length = 1.6
  Length2 = 5
  Profile = -> Sketch092
  ReferenceAxis = -> Sketch092 [N_Axis]
  Refine = true
  Suppressed = false
  Type = 0
FEATURE [PartDesign::Pad] Pad006
  BaseFeature = -> Pocket001
  Direction = (0,1,-2e-16)
  Length = 0.8
  Length2 = 10
  Profile = -> Sketch094
  ReferenceAxis = -> Sketch094 [N_Axis]
  Refine = true
  Suppressed = false
  Type = 0
FEATURE [PartDesign::Pad] Pad007
  BaseFeature = -> Pad006
  Direction = (0,1,-2e-16)
  Length = 2
  Length2 = 10
  Profile = -> Sketch095
  ReferenceAxis = -> Sketch095 [N_Axis]
  Refine = true
  Suppressed = false
  Type = 0
FEATURE [PartDesign::Pad] Pad008  label="Pad008 - forma impugnatura"
  BaseFeature = -> Pad007
  Direction = (0,1,-2e-16)
  Length = 1.6
  Length2 = 10
  Profile = -> Sketch096
  ReferenceAxis = -> Sketch096 [N_Axis]
  Refine = true
  Suppressed = false
  Type = 0
FEATURE [PartDesign::Pad] Pad009
  BaseFeature = -> Pad008
  Direction = (0,1,-2e-16)
  Length = 1.6
  Length2 = 10
  Profile = -> Sketch097
  ReferenceAxis = -> Sketch097 [N_Axis]
  Refine = true
  Suppressed = false
  Type = 0
FEATURE [Sketcher::SketchObject] Sketch098
  ArcFitTolerance = 1e-06
  AttachmentSupport = -> [Pad006]
  ExternalGeometry = -> [Binder]
  FullyConstrained = true
  MakeInternals = false
  MapMode = 5
  Placement = pos=(0,2.8,-7e-16) rot=(0,0.707107,0.707107;3.14159rad)
  sketch-geometry (4):
    g0: LineSegment StartX=118 StartY=39.2 StartZ=0 EndX=129 EndY=39.2 EndZ=0
    g1: LineSegment StartX=120.599 StartY=31.2 StartZ=0 EndX=131.599 EndY=31.2 EndZ=0
    g2: LineSegment StartX=129 StartY=39.2 StartZ=0 EndX=131.599 EndY=31.2 EndZ=0
    g3: LineSegment StartX=118 StartY=39.2 StartZ=0 EndX=120.599 EndY=31.2 EndZ=0
  constraints (12):
    c: PointOnObject(g0,g-3)
    c: PointOnObject(g0,g-3)
    c: DistanceX(g0,g0) = 11
    c: Horizontal(g1)
    c: Equal(g1,g0)
    c: Coincident(g2,g0)
    c: Coincident(g3,g0)
    c: Parallel(g-4,g2)
    c: Coincident(g1,g2)
    c: Coincident(g1,g3)
    c: DistanceY(g1,g0) = 8
    c: DistanceX(g-3,g0) = 118
FEATURE [Sketcher::SketchObject] Sketch099
  ArcFitTolerance = 1e-06
  AttachmentSupport = -> [Pad008]
  ExternalGeometry = -> [Binder]
  FullyConstrained = true
  MakeInternals = false
  MapMode = 5
  Placement = pos=(0,3.6,0) rot=(0,0.707107,0.707107;3.14159rad)
  sketch-geometry (13):
    g0: LineSegment StartX=192.176 StartY=-3.18451 StartZ=0 EndX=196.804 EndY=-13.1108 EndZ=0
    g1: LineSegment [constr] StartX=202.765 StartY=20.303 StartZ=0 EndX=181.223 EndY=20.303 EndZ=0
    g2: LineSegment [constr] StartX=181.223 StartY=20.303 StartZ=0 EndX=181.223 EndY=-3.18451 EndZ=0
    g3: ArcOfCircle CenterX=181.223 CenterY=-20.3764 CenterZ=0 NormalX=0 NormalY=0 NormalZ=1 AngleXU=0 Radius=17.1918 StartAngle=0.436332 EndAngle=1.57079
    g4: ArcOfEllipse CenterX=181.223 CenterY=8.55923 CenterZ=0 NormalX=0 NormalY=0 NormalZ=1 MajorRadius=23.4779 MinorRadius=11.7437 AngleXU=0 StartAngle=1.5708 EndAngle=4.71239
    g5: LineSegment [constr] StartX=204.701 StartY=8.55923 StartZ=0 EndX=157.745 EndY=8.55923 EndZ=0
    g6: LineSegment [constr] StartX=181.223 StartY=20.303 StartZ=0 EndX=181.223 EndY=-3.18451 EndZ=0
    g7: GeomPoint [constr] X=201.553 Y=8.55923 Z=0
    g8: GeomPoint [constr] X=160.894 Y=8.55923 Z=0
    g9: GeomPoint [constr] X=181.223 Y=-3.18451 Z=0
    g10: LineSegment StartX=181.223 StartY=20.303 StartZ=0 EndX=202.765 EndY=20.303 EndZ=0
    g11: ArcOfCircle CenterX=207.583 CenterY=4 CenterZ=0 NormalX=0 NormalY=0 NormalZ=1 AngleXU=0 Radius=17 StartAngle=1.85815 EndAngle=3.57792
    g12: LineSegment [constr] StartX=172.411 StartY=39.2 StartZ=0 EndX=192.176 EndY=-3.18451 EndZ=0
  constraints (27):
    c: Coincident(g1,g-7)
    c: Horizontal(g1)
    c: Coincident(g2,g1)
    c: Vertical(g2)
    c: Horizontal(g2,g0)
    c: Coincident(g3,g0)
    c: Coincident(g3,g2)
    c: InternalAlignment(g5-g8 -> g4) x4
    c: Horizontal(g5)
    c: PointOnObject(g4,g2)
    c: Coincident(g4,g1)
    c: DistanceX(g-3,g5) = 10.1
    c: Coincident(g4,g2)
    c: Tangent(g3,g-5)
    c: PointOnObject(g9,g4)
    c: PointOnObject(g9,g3)
    c: Tangent(g4,g3,g9) = 1.5708
    c: Coincident(g10,g1)
    c: Coincident(g10,g1)
    c: Equal(g11,g-4)
    c: Coincident(g11,g1)
    c: Coincident(g11,g0)
    c: PointOnObject(g12,g-6)
    c: PointOnObject(g1,g12)
    c: Tangent(g12,g-5) = -1.5708
    c: Tangent(g0,g-5) = -1.5708
    c: Horizontal(g9,g12)
FEATURE [Sketcher::SketchObject] Sketch106  label="Sketch106 - smusso impuniatura interno"
  ArcFitTolerance = 1e-06
  AttachmentSupport = -> [Pad008]
  ExternalGeometry = -> [Pad008]
  FullyConstrained = true
  MakeInternals = false
  MapMode = 5
  Placement = pos=(0,-1.586e-13,-80.4316) rot=(1,0,0;3.14159rad)
  sketch-geometry (9):
    g0: LineSegment StartX=-176.685 StartY=-3.6 StartZ=0 EndX=-176.685 EndY=-1.452e-13 EndZ=0
    g1: LineSegment [constr] StartX=-176.685 StartY=-1.416e-13 StartZ=0 EndX=-176.685 EndY=-1.452e-13 EndZ=0
    g2: LineSegment [constr] StartX=-186.685 StartY=-3.6 StartZ=0 EndX=-186.685 EndY=-1.452e-13 EndZ=0
    g3: ArcOfEllipse CenterX=-186.685 CenterY=-1.452e-13 CenterZ=0 NormalX=0 NormalY=0 NormalZ=1 MajorRadius=10 MinorRadius=3.6 AngleXU=3.14159 StartAngle=1.5708 EndAngle=3.14159
    g4: LineSegment [constr] StartX=-196.685 StartY=-1.416e-13 StartZ=0 EndX=-176.685 EndY=-1.416e-13 EndZ=0
    g5: LineSegment [constr] StartX=-186.685 StartY=-3.6 StartZ=0 EndX=-186.685 EndY=3.6 EndZ=0
    g6: GeomPoint [constr] X=-196.015 Y=-1.416e-13 Z=0
    g7: GeomPoint [constr] X=-177.356 Y=-1.416e-13 Z=0
    g8: LineSegment StartX=-176.685 StartY=-3.6 StartZ=0 EndX=-186.685 EndY=-3.6 EndZ=0
  constraints (15):
    c: PointOnObject(g2,g-3)
    c: Coincident(g1,g-5)
    c: DistanceY(g1,g1) = 0
    c: Coincident(g0,g1)
    c: DistanceX(g2,g-5) = 10
    c: Vertical(g2)
    c: Horizontal(g2,g0)
    c: InternalAlignment(g4-g7 -> g3) x4
    c: Coincident(g3,g2)
    c: Horizontal(g4)
    c: Coincident(g3,g0)
    c: Tangent(g0,g-5) = 1.5708
    c: Coincident(g3,g2)
    c: Coincident(g8,g0)
    c: Coincident(g8,g2)
FEATURE [Sketcher::SketchObject] Sketch107  label="Sketch107 - smusso impugnatura esterno"
  ArcFitTolerance = 1e-06
  AttachmentSupport = -> [Pad008]
  ExternalGeometry = -> [Pad008]
  FullyConstrained = true
  MakeInternals = false
  MapMode = 5
  Placement = pos=(0,-1.586e-13,-80.4316) rot=(1,0,0;3.14159rad)
  sketch-geometry (9):
    g0: LineSegment [constr] StartX=-215.932 StartY=1.79e-14 StartZ=0 EndX=-215.932 EndY=2.34e-14 EndZ=0
    g1: LineSegment StartX=-215.932 StartY=-3.6 StartZ=0 EndX=-215.932 EndY=2.35e-14 EndZ=0
    g2: LineSegment StartX=-215.932 StartY=-3.6 StartZ=0 EndX=-205.932 EndY=-3.6 EndZ=0
    g3: LineSegment [constr] StartX=-205.932 StartY=-3.6 StartZ=0 EndX=-205.932 EndY=2.35e-14 EndZ=0
    g4: ArcOfEllipse CenterX=-205.932 CenterY=2.34e-14 CenterZ=0 NormalX=0 NormalY=0 NormalZ=1 MajorRadius=10 MinorRadius=3.6 AngleXU=3.14159 StartAngle=1e-16 EndAngle=1.5708
    g5: LineSegment [constr] StartX=-215.932 StartY=1.79e-14 StartZ=0 EndX=-195.932 EndY=1.79e-14 EndZ=0
    g6: LineSegment [constr] StartX=-205.932 StartY=-3.6 StartZ=0 EndX=-205.932 EndY=3.6 EndZ=0
    g7: GeomPoint [constr] X=-215.262 Y=2.37e-14 Z=0
    g8: GeomPoint [constr] X=-196.602 Y=1.78e-14 Z=0
  constraints (16):
    c: Coincident(g0,g-6)
    c: PointOnObject(g0,g-6)
    c: DistanceY(g0,g0) = 0
    c: Coincident(g1,g-6)
    c: Coincident(g1,g0)
    c: Tangent(g2,g-3)
    c: DistanceX(g2,g2) = 10
    c: Coincident(g3,g2)
    c: Vertical(g3)
    c: Horizontal(g3,g0)
    c: InternalAlignment(g5-g8 -> g4) x4
    c: Coincident(g4,g3)
    c: Horizontal(g5)
    c: Coincident(g4,g0)
    c: Coincident(g4,g2)
    c: PointOnObject(g2,g1)
FEATURE [Sketcher::SketchObject] Sketch108
  ArcFitTolerance = 1e-06
  AttachmentOffset = pos=(0,0,-1.6) rot=(0,0,1;0rad)
  AttachmentSupport = -> [Pad008]
  ExternalGeometry = -> [Binder]
  FullyConstrained = true
  MakeInternals = false
  MapMode = 5
  Placement = pos=(0,2,4e-16) rot=(0,0.707107,0.707107;3.14159rad)
  sketch-geometry (14):
    g0: LineSegment StartX=192.176 StartY=-3.18451 StartZ=0 EndX=193.827 EndY=-6.72678 EndZ=0
    g1: LineSegment [constr] StartX=202.765 StartY=20.303 StartZ=0 EndX=181.223 EndY=20.303 EndZ=0
    g2: LineSegment [constr] StartX=181.223 StartY=20.303 StartZ=0 EndX=181.223 EndY=1.30297 EndZ=0
    g3: ArcOfCircle CenterX=181.223 CenterY=-12.6042 CenterZ=0 NormalX=0 NormalY=0 NormalZ=1 AngleXU=0 Radius=13.9072 StartAngle=0.436332 EndAngle=1.5708
    g4: ArcOfEllipse CenterX=181.223 CenterY=10.803 CenterZ=0 NormalX=0 NormalY=0 NormalZ=1 MajorRadius=14.4779 MinorRadius=9.5 AngleXU=0 StartAngle=1.5708 EndAngle=4.71239
    g5: LineSegment [constr] StartX=195.701 StartY=10.803 StartZ=0 EndX=166.745 EndY=10.803 EndZ=0
    g6: LineSegment [constr] StartX=181.223 StartY=20.303 StartZ=0 EndX=181.223 EndY=1.30297 EndZ=0
    g7: GeomPoint [constr] X=192.148 Y=10.803 Z=0
    g8: GeomPoint [constr] X=170.298 Y=10.803 Z=0
    g9: LineSegment StartX=181.223 StartY=20.303 StartZ=0 EndX=202.765 EndY=20.303 EndZ=0
    g10: ArcOfCircle CenterX=207.583 CenterY=4 CenterZ=0 NormalX=0 NormalY=0 NormalZ=1 AngleXU=0 Radius=17 StartAngle=1.85815 EndAngle=3.57792
    g11: LineSegment [constr] StartX=172.411 StartY=39.2 StartZ=0 EndX=192.176 EndY=-3.18451 EndZ=0
    g12: GeomPoint [constr] X=181.223 Y=1.30297 Z=0
    g13: GeomPoint [constr] X=181.223 Y=1.30297 Z=0
  constraints (28):
    c: Coincident(g1,g-7)
    c: Horizontal(g1)
    c: Coincident(g2,g1)
    c: Vertical(g2)
    c: Coincident(g3,g2)
    c: InternalAlignment(g5-g8 -> g4) x4
    c: Horizontal(g5)
    c: PointOnObject(g4,g2)
    c: Coincident(g4,g1)
    c: DistanceX(g-3,g5) = 19.1
    c: Coincident(g4,g2)
    c: Coincident(g9,g1)
    c: Coincident(g9,g1)
    c: Coincident(g10,g1)
    c: Coincident(g10,g0)
    c: PointOnObject(g11,g-6)
    c: PointOnObject(g1,g11)
    c: DistanceY(g2,g1) = 19
    c: Coincident(g10,g-4)
    c: PointOnObject(g12,g4)
    c: PointOnObject(g12,g3)
    c: Tangent(g11,g-5) = -1.5708
    c: Tangent(g0,g-5) = -1.5708
    c: Tangent(g3,g0) = 1.5708
    c: PointOnObject(g13,g4)
    c: PointOnObject(g13,g3)
    c: Tangent(g4,g3,g13) = 1.5708
    c: Horizontal(g11,g0)
FEATURE [Part::Part2DObjectPython] Clone2D  label="Sketch108 (2D)"  # Draft 2D object (typed FeaturePython)
  Fuse = false
  Objects = -> [Sketch108]
  Placement = pos=(0,2,4e-16) rot=(0,0.707107,0.707107;3.14159rad)
  Scale = (1,1,1)
FEATURE [Sketcher::SketchObject] Sketch109
  ArcFitTolerance = 1e-06
  AttachmentOffset = pos=(0,0,-3.5) rot=(0,0,1;0rad)
  AttachmentSupport = -> [Pad008]
  ExternalGeometry = -> [Binder]
  FullyConstrained = true
  MakeInternals = false
  MapMode = 5
  Placement = pos=(0,0.1,8e-16) rot=(0,0.707107,0.707107;3.14159rad)
  sketch-geometry (1):
    g0: GeomPoint X=197.47 Y=8.55923 Z=0
  constraints (1):
    c: Symmetric(g-7,g-5,g0)
FEATURE [PartDesign::Chamfer] Chamfer005
  Angle = 45
  Base = -> Pad009 [Edge215,Edge212]
  BaseFeature = -> Pad009
  ChamferType = 1
  FlipDirection = false
  Refine = true
  Size = 1.5
  Size2 = 2.8
  SupportTransform = false
  Suppressed = false
  UseAllEdges = false
FEATURE [Sketcher::SketchObject] Sketch111
  ArcFitTolerance = 1e-06
  AttachmentSupport = -> [Pad009]
  ExternalGeometry = -> [Pad009]
  FullyConstrained = true
  MakeInternals = false
  MapMode = 5
  Placement = pos=(0,3.6,-8e-16) rot=(0,0.707107,0.707107;3.14159rad)
  sketch-geometry (21):
    g0: LineSegment [constr] StartX=97 StartY=36.8 StartZ=0 EndX=97 EndY=26.8 EndZ=0
    g1: LineSegment StartX=97 StartY=28.6 StartZ=0 EndX=97 EndY=27.8 EndZ=0
    g2: LineSegment StartX=97 StartY=27.8 StartZ=0 EndX=108 EndY=27.8 EndZ=0
    g3: LineSegment StartX=108 StartY=27.8 StartZ=0 EndX=108 EndY=28.6 EndZ=0
    g4: LineSegment StartX=108 StartY=28.6 StartZ=0 EndX=97 EndY=28.6 EndZ=0
    g5: LineSegment StartX=97 StartY=35.8 StartZ=0 EndX=97 EndY=35 EndZ=0
    g6: LineSegment StartX=97 StartY=35 StartZ=0 EndX=108 EndY=35 EndZ=0
    g7: LineSegment StartX=108 StartY=35 StartZ=0 EndX=108 EndY=35.8 EndZ=0
    g8: LineSegment StartX=108 StartY=35.8 StartZ=0 EndX=97 EndY=35.8 EndZ=0
    g9: LineSegment StartX=97 StartY=30.4 StartZ=0 EndX=97 EndY=29.6 EndZ=0
    g10: LineSegment StartX=97 StartY=29.6 StartZ=0 EndX=108 EndY=29.6 EndZ=0
    g11: LineSegment StartX=108 StartY=29.6 StartZ=0 EndX=108 EndY=30.4 EndZ=0
    g12: LineSegment StartX=108 StartY=30.4 StartZ=0 EndX=97 EndY=30.4 EndZ=0
    g13: LineSegment StartX=97 StartY=34 StartZ=0 EndX=97 EndY=33.2 EndZ=0
    g14: LineSegment StartX=97 StartY=33.2 StartZ=0 EndX=108 EndY=33.2 EndZ=0
    g15: LineSegment StartX=108 StartY=33.2 StartZ=0 EndX=108 EndY=34 EndZ=0
    g16: LineSegment StartX=108 StartY=34 StartZ=0 EndX=97 EndY=34 EndZ=0
    g17: LineSegment StartX=97 StartY=32.2 StartZ=0 EndX=97 EndY=31.4 EndZ=0
    g18: LineSegment StartX=97 StartY=31.4 StartZ=0 EndX=108 EndY=31.4 EndZ=0
    g19: LineSegment StartX=108 StartY=31.4 StartZ=0 EndX=108 EndY=32.2 EndZ=0
    g20: LineSegment StartX=108 StartY=32.2 StartZ=0 EndX=97 EndY=32.2 EndZ=0
  constraints (54):
    c: Vertical(g0)
    c: PointOnObject(g0,g-3)
    c: PointOnObject(g0,g-4)
    c: DistanceX(g0,g-5) = 11
    c: Coincident(g1,g2)
    c: Coincident(g2,g3)
    c: Coincident(g3,g4)
    c: Coincident(g4,g1)
    c: Horizontal(g2)
    c: Horizontal(g4)
    c: Tangent(g1,g0)
    c: Tangent(g3,g-5)
    c: DistanceY(g2,g3) = 0.8
    c: Coincident(g5,g6)
    c: Coincident(g6,g7)
    c: Coincident(g7,g8)
    c: Coincident(g8,g5)
    c: Horizontal(g6)
    c: Horizontal(g8)
    c: DistanceY(g6,g7) = 0.8
    c: Coincident(g9,g10)
    c: Coincident(g10,g11)
    c: Coincident(g11,g12)
    c: Coincident(g12,g9)
    c: Horizontal(g10)
    c: Horizontal(g12)
    c: DistanceY(g10,g11) = 0.8
    c: Tangent(g5,g0)
    c: Tangent(g7,g-5)
    c: Tangent(g9,g0)
    c: Tangent(g11,g-5)
    c: Coincident(g13,g14)
    c: Coincident(g14,g15)
    c: Coincident(g15,g16)
    c: Coincident(g16,g13)
    c: Horizontal(g14)
    c: Horizontal(g16)
    c: DistanceY(g14,g15) = 0.8
    c: Tangent(g13,g0)
    c: Tangent(g15,g-5)
    c: Coincident(g17,g18)
    c: Coincident(g18,g19)
    c: Coincident(g19,g20)
    c: Coincident(g20,g17)
    c: Horizontal(g18)
    c: Horizontal(g20)
    c: DistanceY(g18,g19) = 0.8
    c: Tangent(g17,g0)
    c: Tangent(g19,g-5)
    c: DistanceY(g1,g9) = 1
    c: DistanceY(g9,g17) = 1
    c: DistanceY(g17,g13) = 1
    c: DistanceY(g13,g5) = 1
    c: DistanceY(g0,g1) = 1
FEATURE [PartDesign::Pocket] Pocket004
  BaseFeature = -> Chamfer005
  Direction = (0,-1,2e-16)
  Length = 1
  Length2 = 5
  Profile = -> Sketch111
  ReferenceAxis = -> Sketch111 [N_Axis]
  Refine = true
  Suppressed = false
  Type = 0
FEATURE [PartDesign::Pad] Pad010
  BaseFeature = -> Pocket004
  Direction = (0,1,-2e-16)
  Length = 1.2
  Length2 = 10
  Profile = -> Sketch098
  ReferenceAxis = -> Sketch098 [N_Axis]
  Refine = true
  Suppressed = false
  Type = 0
FEATURE [PartDesign::Chamfer] Chamfer006
  Angle = 45
  Base = -> Pad010 [Edge291]
  BaseFeature = -> Pad010
  ChamferType = 1
  FlipDirection = false
  Refine = true
  Size = 1
  Size2 = 6
  SupportTransform = false
  Suppressed = false
  UseAllEdges = false
FEATURE [Sketcher::SketchObject] Sketch110
  ArcFitTolerance = 1e-06
  AttachmentSupport = -> [Pad010]
  ExternalGeometry = -> [Sketch098]
  FullyConstrained = true
  MakeInternals = false
  MapMode = 5
  Placement = pos=(0,4,-9e-16) rot=(0,0.707107,0.707107;3.14159rad)
  sketch-geometry (8):
    g0: LineSegment StartX=119.69 StartY=34 StartZ=0 EndX=130.69 EndY=34 EndZ=0
    g1: LineSegment StartX=119.95 StartY=33.2 StartZ=0 EndX=130.95 EndY=33.2 EndZ=0
    g2: LineSegment StartX=119.137 StartY=35.7 StartZ=0 EndX=130.137 EndY=35.7 EndZ=0
    g3: LineSegment StartX=118.877 StartY=36.5 StartZ=0 EndX=129.877 EndY=36.5 EndZ=0
    g4: LineSegment StartX=118.877 StartY=36.5 StartZ=0 EndX=119.137 EndY=35.7 EndZ=0
    g5: LineSegment StartX=129.877 StartY=36.5 StartZ=0 EndX=130.137 EndY=35.7 EndZ=0
    g6: LineSegment StartX=119.69 StartY=34 StartZ=0 EndX=119.95 EndY=33.2 EndZ=0
    g7: LineSegment StartX=130.69 StartY=34 StartZ=0 EndX=130.95 EndY=33.2 EndZ=0
  constraints (24):
    c: Horizontal(g0)
    c: Horizontal(g1)
    c: Horizontal(g2)
    c: Horizontal(g3)
    c: Equal(g1,g-5)
    c: Equal(g0,g-5)
    c: Equal(g2,g-5)
    c: Equal(g3,g-5)
    c: PointOnObject(g0,g-3)
    c: PointOnObject(g1,g-3)
    c: PointOnObject(g2,g-3)
    c: PointOnObject(g3,g-3)
    c: Coincident(g4,g3)
    c: Coincident(g4,g2)
    c: Coincident(g5,g3)
    c: Coincident(g5,g2)
    c: Coincident(g6,g0)
    c: Coincident(g6,g1)
    c: Coincident(g7,g0)
    c: Coincident(g7,g1)
    c: DistanceY(g1,g0) = 0.8
    c: DistanceY(g2,g3) = 0.8
    c: DistanceY(g-5,g1) = 2
    c: DistanceY(g-5,g2) = 4.5
FEATURE [PartDesign::Pocket] Pocket003
  BaseFeature = -> Chamfer006
  Direction = (0,-1,2e-16)
  Length = 1
  Length2 = 5
  Profile = -> Sketch110
  ReferenceAxis = -> Sketch110 [N_Axis]
  Refine = true
  Suppressed = false
  Type = 0
FEATURE [PartDesign::SubtractivePipe] SubtractivePipe
  AuxilleryCurvelinear = true
  AuxillerySpineTangent = false
  BaseFeature = -> Pocket003
  Binormal = (0,0,0)
  Mode = 0
  Profile = -> Sketch106
  Refine = true
  Spine = -> Pad008 [Edge215]
  SpineTangent = false
  Suppressed = false
  Transformation = 0
  Transition = 0
FEATURE [PartDesign::SubtractivePipe] SubtractivePipe001
  AuxilleryCurvelinear = true
  AuxillerySpineTangent = false
  BaseFeature = -> SubtractivePipe
  Binormal = (0,0,0)
  Mode = 0
  Profile = -> Sketch107
  Refine = true
  Spine = -> Pad008 [Edge213,Edge216,Edge210]
  SpineTangent = false
  Suppressed = false
  Transformation = 0
  Transition = 0
FEATURE [PartDesign::SubtractiveLoft] SubtractiveLoft
  BaseFeature = -> SubtractivePipe001
  Closed = false
  Profile = -> Sketch099
  Refine = true
  Ruled = false
  Sections = -> [Sketch108]
  Suppressed = false
FEATURE [PartDesign::SubtractiveLoft] SubtractiveLoft001
  BaseFeature = -> SubtractiveLoft
  Closed = false
  Profile = -> Clone2D
  Refine = true
  Ruled = false
  Sections = -> [Sketch109]
  Suppressed = false
FEATURE [Sketcher::SketchObject] Sketch112
  ArcFitTolerance = 1e-06
  AttachmentSupport = -> [Pad008]
  ExternalGeometry = -> [Binder]
  FullyConstrained = true
  MakeInternals = false
  MapMode = 5
  Placement = pos=(0,3.6,0) rot=(0,0.707107,0.707107;3.14159rad)
  sketch-geometry (4):
    g0: LineSegment [constr] StartX=167.782 StartY=-53.0314 StartZ=0 EndX=215.42 EndY=-53.0314 EndZ=0
    g1: GeomPoint [constr] X=191.282 Y=-53.0314 Z=0
    g2: Circle CenterX=191.282 CenterY=-53.0314 CenterZ=0 NormalX=0 NormalY=0 NormalZ=1 AngleXU=0 Radius=11.5
    g3: Circle CenterX=191.282 CenterY=-53.0314 CenterZ=0 NormalX=0 NormalY=0 NormalZ=1 AngleXU=0 Radius=10.7
  constraints (9):
    c: Horizontal(g0)
    c: PointOnObject(g0,g-3)
    c: Diameter(g2) = 23
    c: Coincident(g2,g1)
    c: Diameter(g3) = 21.4
    c: Coincident(g3,g1)
    c: DistanceX(g0,g1) = 23.5
    c: PointOnObject(g1,g0)
    c: Coincident(g0,g-4)
FEATURE [PartDesign::Chamfer] Chamfer016
  Angle = 45
  Base = -> SubtractiveLoft001 [Edge118,Edge117,Edge119,Edge120,Edge109]
  BaseFeature = -> SubtractiveLoft001
  ChamferType = 0
  FlipDirection = false
  Refine = true
  Size = 1.5
  Size2 = 1
  SupportTransform = false
  Suppressed = false
  UseAllEdges = false
FEATURE [PartDesign::Chamfer] Chamfer017
  Angle = 45
  Base = -> Chamfer016 [Edge15]
  BaseFeature = -> Chamfer016
  ChamferType = 0
  FlipDirection = false
  Refine = true
  Size = 1.6
  Size2 = 1
  SupportTransform = false
  Suppressed = false
  UseAllEdges = false
FEATURE [PartDesign::Chamfer] Chamfer018
  Angle = 45
  Base = -> Chamfer017 [Edge10]
  BaseFeature = -> Chamfer017
  ChamferType = 0
  FlipDirection = false
  Refine = true
  Size = 3.5
  Size2 = 1
  SupportTransform = false
  Suppressed = false
  UseAllEdges = false
FEATURE [PartDesign::Chamfer] Chamfer019
  Angle = 45
  Base = -> Chamfer018 [Edge94,Edge199]
  BaseFeature = -> Chamfer018
  ChamferType = 0
  FlipDirection = false
  Refine = true
  Size = 1.9
  Size2 = 1
  SupportTransform = false
  Suppressed = false
  UseAllEdges = false
FEATURE [PartDesign::Fillet] Fillet009
  Base = -> Chamfer019 [Edge83]
  BaseFeature = -> Chamfer019
  Radius = 1.1
  Refine = true
  SupportTransform = false
  Suppressed = false
  UseAllEdges = false
FEATURE [PartDesign::Fillet] Fillet010
  Base = -> Fillet009 [Edge77]
  BaseFeature = -> Fillet009
  Radius = 1.9
  Refine = true
  SupportTransform = false
  Suppressed = false
  UseAllEdges = false
FEATURE [PartDesign::Pocket] Pocket005
  BaseFeature = -> Fillet010
  Direction = (0,-1,2e-16)
  Length = 0.8
  Length2 = 5
  Profile = -> Sketch112
  ReferenceAxis = -> Sketch112 [N_Axis]
  Refine = true
  Suppressed = false
  Type = 0
FEATURE [Part::Part2DObjectPython] ShapeString001  # Draft 2D object (typed FeaturePython)
  FontFile = <path>
  Fuse = false
  Justification = 6
  JustificationReference = 0
  KeepLeftMargin = false
  MakeFace = true
  ObliqueAngle = 0
  Placement = pos=(-183.5,3.6,-57.5) rot=(0,0.707107,0.707107;3.14159rad)
  ScaleToSize = true
  Size = 10
  String = AS
  Tracking = 0
FEATURE [PartDesign::Pocket] Pocket013
  BaseFeature = -> Pocket005
  Direction = (-1e-16,-1,2e-16)
  Length = 1
  Length2 = 5
  Profile = -> ShapeString001
  ReferenceAxis = -> ShapeString001 [N_Axis]
  Refine = true
  Suppressed = false
  Type = 0
FEATURE [PartDesign::Body] Body006  label="lato SX"
  AllowCompound = false
  Group = -> [Binder,Pad019,Chamfer015,Pocket002,Sketch133,Sketch091,Pad005,Sketch092,Pocket001,Sketch093,Sketch094,Pad006,Sketch095,Pad007,Sketch096,Pad008,Sketch097,Pad009,Chamfer005,Pocket004,Sketch098,Pad010,Chamfer006,Pocket003,SubtractivePipe,SubtractivePipe001,Sketch099,Sketch106,Sketch107,Sketch108,Clone2D,Sketch109,SubtractiveLoft,SubtractiveLoft001,Sketch110,Sketch111,Sketch112,Chamfer016,Chamfer017,+7 more]
  Origin = -> Origin006
  Tip = -> Pocket013
FEATURE [PartDesign::Pad] Pad020
  Direction = (0,-1,2e-16)
  Length = 25.2
  Length2 = 10
  Midplane = true
  Placement = pos=(0,0,0) rot=(1,0,0;1.5708rad)
  Profile = -> Sketch021
  ReferenceAxis = -> Sketch021 [N_Axis]
  Refine = true
  Suppressed = false
  Type = 0
FEATURE [PartDesign::Body] Body001  label="perno fermo rumble e driver solenoide"
  AllowCompound = false
  Group = -> [Sketch021,Pad020]
  Origin = -> Origin001
  Tip = -> Pad020
FEATURE [PartDesign::Pad] Pad021
  Direction = (0,-1,2e-16)
  Length = 16.8
  Length2 = 10
  Midplane = true
  Placement = pos=(0,0,0) rot=(1,0,0;1.5708rad)
  Profile = -> Sketch061
  ReferenceAxis = -> Sketch061 [N_Axis]
  Refine = true
  Suppressed = false
  Type = 0
FEATURE [PartDesign::Pocket] Pocket014
  BaseFeature = -> Pad021
  Direction = (0,1,-2e-16)
  Length = 12.8
  Length2 = 5
  Midplane = true
  Placement = pos=(0,0,0) rot=(1,0,0;1.5708rad)
  Profile = -> Sketch062
  ReferenceAxis = -> Sketch062 [N_Axis]
  Refine = true
  Suppressed = false
  Type = 0
FEATURE [PartDesign::Pad] Pad022
  BaseFeature = -> Pocket014
  Direction = (0,-1,2e-16)
  Length = 7.6
  Length2 = 10
  Midplane = true
  Placement = pos=(0,0,0) rot=(1,0,0;1.5708rad)
  Profile = -> Sketch063
  ReferenceAxis = -> Sketch063 [N_Axis]
  Refine = true
  Suppressed = false
  Type = 0
FEATURE [PartDesign::Body] Body003  label="blocco switch"
  AllowCompound = false
  Group = -> [Sketch061,Sketch062,Sketch063,Pad021,Pocket014,Pad022]
  Origin = -> Origin003
  Tip = -> Pad022
FEATURE [PartDesign::Pad] Pad024
  Direction = (0,-1,2e-16)
  Length = 17
  Length2 = 10
  Midplane = true
  Placement = pos=(0,0,0) rot=(1,0,0;1.5708rad)
  Profile = -> Sketch045
  ReferenceAxis = -> Sketch045 [N_Axis]
  Refine = true
  Suppressed = false
  Type = 0
FEATURE [PartDesign::Pocket] Pocket015
  BaseFeature = -> Pad024
  Direction = (-1,0,0)
  Length = 8
  Length2 = 5
  Placement = pos=(0,0,0) rot=(1,0,0;1.5708rad)
  Profile = -> Sketch047
  ReferenceAxis = -> Sketch047 [N_Axis]
  Refine = true
  Reversed = true
  Suppressed = false
  Type = 0
FEATURE [PartDesign::Pocket] Pocket016
  BaseFeature = -> Pocket015
  Direction = (-1,0,0)
  Length = 1
  Length2 = 5
  Placement = pos=(0,0,0) rot=(1,0,0;1.5708rad)
  Profile = -> Sketch046
  ReferenceAxis = -> Sketch046 [N_Axis]
  Refine = true
  Reversed = true
  Suppressed = false
  Type = 0
FEATURE [PartDesign::Pocket] Pocket017
  BaseFeature = -> Pocket016
  Direction = (0,1,-2e-16)
  Length = 17
  Length2 = 5
  Midplane = true
  Placement = pos=(0,0,0) rot=(1,0,0;1.5708rad)
  Profile = -> Sketch048
  ReferenceAxis = -> Sketch048 [N_Axis]
  Refine = true
  Suppressed = false
  Type = 0
FEATURE [PartDesign::Pad] Pad025
  BaseFeature = -> Pocket017
  Direction = (0,-1,2e-16)
  Length = 17
  Length2 = 10
  Midplane = true
  Placement = pos=(0,0,0) rot=(1,0,0;1.5708rad)
  Profile = -> Sketch049
  ReferenceAxis = -> Sketch049 [N_Axis]
  Refine = true
  Suppressed = false
  Type = 0
FEATURE [PartDesign::Pad] Pad026
  BaseFeature = -> Pad025
  Direction = (0,-1,2e-16)
  Length = 17
  Length2 = 10
  Midplane = true
  Placement = pos=(0,0,0) rot=(1,0,0;1.5708rad)
  Profile = -> Sketch066
  ReferenceAxis = -> Sketch066 [N_Axis]
  Refine = true
  Suppressed = false
  Type = 0
FEATURE [PartDesign::Pad] Pad027
  BaseFeature = -> Pad026
  Direction = (0,-1,2e-16)
  Length = 5
  Length2 = 10
  Midplane = true
  Placement = pos=(0,0,0) rot=(1,0,0;1.5708rad)
  Profile = -> Sketch064
  ReferenceAxis = -> Sketch064 [N_Axis]
  Refine = true
  Suppressed = false
  Type = 0
FEATURE [PartDesign::Pad] Pad028
  BaseFeature = -> Pad027
  Direction = (1,0,0)
  Length = 1
  Length2 = 10
  Placement = pos=(0,0,0) rot=(1,0,0;1.5708rad)
  Profile = -> Sketch068
  ReferenceAxis = -> Sketch068 [N_Axis]
  Refine = true
  Reversed = true
  Suppressed = false
  Type = 0
FEATURE [PartDesign::Chamfer] Chamfer020
  Angle = 45
  Base = -> Pad028 [Edge73,Edge75,Edge78,Edge77]
  BaseFeature = -> Pad028
  ChamferType = 0
  FlipDirection = false
  Placement = pos=(0,0,0) rot=(1,0,0;1.5708rad)
  Refine = true
  Size = 0.5
  Size2 = 1
  SupportTransform = false
  Suppressed = false
  UseAllEdges = false
FEATURE [PartDesign::Body] Body002  label="supporto per neopixel"
  AllowCompound = false
  Group = -> [Sketch045,Sketch047,Sketch046,Sketch048,Sketch049,Sketch066,Sketch064,Sketch068,Pad024,Pocket015,Pocket016,Pocket017,Pad025,Pad026,Pad027,Pad028,Chamfer020]
  Origin = -> Origin002
  Tip = -> Chamfer020
FEATURE [Sketcher::SketchObject] Sketch134  label="perno fermo rumble002"
  ArcFitTolerance = 1e-06
  AttachmentSupport = -> [XZ_Plane008]
  FullyConstrained = true
  MakeInternals = false
  MapMode = 5
  Placement = pos=(0,0,0) rot=(1,0,0;1.5708rad)
  sketch-geometry (16):
    g0: LineSegment StartX=0 StartY=0.45 StartZ=0 EndX=0 EndY=1.55 EndZ=0
    g1: LineSegment StartX=0.45 StartY=2 StartZ=0 EndX=1.55 EndY=2 EndZ=0
    g2: LineSegment StartX=2 StartY=1.55 StartZ=0 EndX=2 EndY=0.45 EndZ=0
    g3: LineSegment StartX=1.55 StartY=0 StartZ=0 EndX=0.45 EndY=0 EndZ=0
    g4: ArcOfCircle [constr] CenterX=0.45 CenterY=1.55 CenterZ=0 NormalX=0 NormalY=0 NormalZ=1 AngleXU=0 Radius=0.45 StartAngle=1.5708 EndAngle=3.14159
    g5: GeomPoint [constr] X=0 Y=2 Z=0
    g6: LineSegment StartX=0.45 StartY=2 StartZ=0 EndX=0 EndY=1.55 EndZ=0
    g7: ArcOfCircle [constr] CenterX=1.55 CenterY=1.55 CenterZ=0 NormalX=0 NormalY=0 NormalZ=1 AngleXU=0 Radius=0.45 StartAngle=0 EndAngle=1.5708
    g8: GeomPoint [constr] X=2 Y=2 Z=0
    g9: LineSegment StartX=2 StartY=1.55 StartZ=0 EndX=1.55 EndY=2 EndZ=0
    g10: ArcOfCircle [constr] CenterX=1.55 CenterY=0.45 CenterZ=0 NormalX=0 NormalY=0 NormalZ=1 AngleXU=0 Radius=0.45 StartAngle=4.71239 EndAngle=6.28319
    g11: GeomPoint [constr] X=2 Y=0 Z=0
    g12: LineSegment StartX=1.55 StartY=0 StartZ=0 EndX=2 EndY=0.45 EndZ=0
    g13: ArcOfCircle [constr] CenterX=0.45 CenterY=0.45 CenterZ=0 NormalX=0 NormalY=0 NormalZ=1 AngleXU=0 Radius=0.45 StartAngle=3.14159 EndAngle=4.71239
    g14: GeomPoint [constr] X=0 Y=0 Z=0
    g15: LineSegment StartX=0 StartY=0.45 StartZ=0 EndX=0.45 EndY=0 EndZ=0
  constraints (35):
    c: Coincident(g14,g-1)
    c: PointOnObject(g5,g-2)
    c: Horizontal(g1)
    c: Vertical(g2)
    c: Horizontal(g3)
    c: DistanceX(g5,g8) = 2
    c: DistanceY(g11,g8) = 2
    c: PointOnObject(g5,g0)
    c: PointOnObject(g5,g1)
    c: Tangent(g0,g4) = 1.5708
    c: Tangent(g1,g4) = 1.5708
    c: Coincident(g6,g0)
    c: Coincident(g6,g1)
    c: PointOnObject(g8,g2)
    c: PointOnObject(g8,g1)
    c: Tangent(g2,g7) = 1.5708
    c: Tangent(g1,g7) = 1.5708
    c: Coincident(g9,g2)
    c: Coincident(g9,g1)
    c: PointOnObject(g11,g2)
    c: PointOnObject(g11,g3)
    c: Tangent(g2,g10) = 1.5708
    c: Tangent(g3,g10) = 1.5708
    c: Coincident(g12,g2)
    c: Coincident(g12,g3)
    c: PointOnObject(g14,g0)
    c: PointOnObject(g14,g3)
    c: Tangent(g0,g13) = 1.5708
    c: Tangent(g3,g13) = 1.5708
    c: Coincident(g15,g0)
    c: Coincident(g15,g3)
    c: Equal(g6,g9)
    c: Equal(g9,g12)
    c: Equal(g12,g15)
    c: DistanceX(g14,g3) = 0.45
FEATURE [PartDesign::Pad] Pad029
  Direction = (0,-1,2e-16)
  Length = 17
  Length2 = 10
  Midplane = true
  Placement = pos=(0,0,0) rot=(1,0,0;1.5708rad)
  Profile = -> Sketch134
  ReferenceAxis = -> Sketch134 [N_Axis]
  Refine = true
  Suppressed = false
  Type = 0
FEATURE [PartDesign::Body] Body008  label="perno fermo neopixel"
  AllowCompound = false
  Group = -> [Sketch134,Pad029]
  Origin = -> Origin008
  Tip = -> Pad029
FEATURE [Sketcher::SketchObject] Sketch135  label="perno fermo rumble003"
  ArcFitTolerance = 1e-06
  AttachmentSupport = -> [XZ_Plane009]
  FullyConstrained = true
  MakeInternals = false
  MapMode = 5
  Placement = pos=(0,0,0) rot=(1,0,0;1.5708rad)
  sketch-geometry (16):
    g0: LineSegment StartX=4.69e-14 StartY=0.8 StartZ=0 EndX=-3.04e-14 EndY=3.1 EndZ=0
    g1: LineSegment StartX=0.8 StartY=3.9 StartZ=0 EndX=3.1 EndY=3.9 EndZ=0
    g2: LineSegment StartX=3.9 StartY=3.1 StartZ=0 EndX=3.9 EndY=0.8 EndZ=0
    g3: LineSegment StartX=3.1 StartY=0 StartZ=0 EndX=0.8 EndY=0 EndZ=0
    g4: ArcOfCircle [constr] CenterX=0.8 CenterY=3.1 CenterZ=0 NormalX=0 NormalY=0 NormalZ=1 AngleXU=0 Radius=0.8 StartAngle=1.5708 EndAngle=3.14159
    g5: GeomPoint [constr] X=0 Y=3.9 Z=0
    g6: LineSegment StartX=0.8 StartY=3.9 StartZ=0 EndX=-3.04e-14 EndY=3.1 EndZ=0
    g7: ArcOfCircle [constr] CenterX=3.1 CenterY=3.1 CenterZ=0 NormalX=0 NormalY=0 NormalZ=1 AngleXU=0 Radius=0.8 StartAngle=-2.4e-14 EndAngle=1.5708
    g8: GeomPoint [constr] X=3.9 Y=3.9 Z=0
    g9: LineSegment StartX=3.9 StartY=3.1 StartZ=0 EndX=3.1 EndY=3.9 EndZ=0
    g10: ArcOfCircle [constr] CenterX=3.1 CenterY=0.8 CenterZ=0 NormalX=0 NormalY=0 NormalZ=1 AngleXU=0 Radius=0.8 StartAngle=4.71239 EndAngle=6.28319
    g11: GeomPoint [constr] X=3.9 Y=0 Z=0
    g12: LineSegment StartX=3.1 StartY=0 StartZ=0 EndX=3.9 EndY=0.8 EndZ=0
    g13: ArcOfCircle [constr] CenterX=0.8 CenterY=0.8 CenterZ=0 NormalX=0 NormalY=0 NormalZ=1 AngleXU=0 Radius=0.8 StartAngle=3.14159 EndAngle=4.71239
    g14: GeomPoint [constr] X=0 Y=0 Z=0
    g15: LineSegment StartX=4.69e-14 StartY=0.8 StartZ=0 EndX=0.8 EndY=0 EndZ=0
  constraints (35):
    c: Coincident(g14,g-1)
    c: PointOnObject(g5,g-2)
    c: Horizontal(g1)
    c: Vertical(g2)
    c: Horizontal(g3)
    c: DistanceX(g5,g8) = 3.9
    c: DistanceY(g11,g8) = 3.9
    c: PointOnObject(g5,g0)
    c: PointOnObject(g5,g1)
    c: Tangent(g0,g4) = 1.5708
    c: Tangent(g1,g4) = 1.5708
    c: Coincident(g6,g0)
    c: Coincident(g6,g1)
    c: PointOnObject(g8,g2)
    c: PointOnObject(g8,g1)
    c: Tangent(g2,g7) = 1.5708
    c: Tangent(g1,g7) = 1.5708
    c: Coincident(g9,g2)
    c: Coincident(g9,g1)
    c: PointOnObject(g11,g2)
    c: PointOnObject(g11,g3)
    c: Tangent(g2,g10) = 1.5708
    c: Tangent(g3,g10) = 1.5708
    c: Coincident(g12,g2)
    c: Coincident(g12,g3)
    c: PointOnObject(g14,g0)
    c: PointOnObject(g14,g3)
    c: Tangent(g0,g13) = 1.5708
    c: Tangent(g3,g13) = 1.5708
    c: Coincident(g15,g0)
    c: Coincident(g15,g3)
    c: Equal(g6,g9)
    c: Equal(g9,g12)
    c: Equal(g12,g15)
    c: DistanceX(g14,g3) = 0.8
FEATURE [PartDesign::Pad] Pad030
  Direction = (0,-1,2e-16)
  Length = 25.2
  Length2 = 10
  Midplane = true
  Placement = pos=(0,0,0) rot=(1,0,0;1.5708rad)
  Profile = -> Sketch135
  ReferenceAxis = -> Sketch135 [N_Axis]
  Refine = true
  Suppressed = false
  Type = 0
FEATURE [PartDesign::Body] Body009  label="perno fermo switch - caricabatterie - grilletto"
  AllowCompound = false
  Group = -> [Sketch135,Pad030]
  Origin = -> Origin009
  Tip = -> Pad030
FEATURE [Sketcher::SketchObject] Sketch136  label="scavo_rele"
  ArcFitTolerance = 1e-06
  AttachmentSupport = -> [XZ_Plane]
  ExternalGeometry = -> [Sketch]
  FullyConstrained = true
  MakeInternals = false
  MapMode = 5
  Placement = pos=(0,0,0) rot=(1,0,0;1.5708rad)
  sketch-geometry (7):
    g0: LineSegment [constr] StartX=-168.686 StartY=-49.3292 StartZ=0 EndX=-170.664 EndY=-55.416 EndZ=0
    g1: LineSegment [constr] StartX=-168.686 StartY=-49.3292 StartZ=0 EndX=-164.882 EndY=-50.5653 EndZ=0
    g2: LineSegment [constr] StartX=-168.686 StartY=-49.3292 StartZ=0 EndX=-172.3 EndY=-48.155 EndZ=0
    g3: LineSegment StartX=-172.3 StartY=-48.155 StartZ=0 EndX=-164.882 EndY=-50.5653 EndZ=0
    g4: LineSegment StartX=-172.3 StartY=-48.155 StartZ=0 EndX=-174.278 EndY=-54.2417 EndZ=0
    g5: LineSegment StartX=-164.882 StartY=-50.5653 StartZ=0 EndX=-166.86 EndY=-56.6521 EndZ=0
    g6: LineSegment StartX=-174.278 StartY=-54.2417 StartZ=0 EndX=-166.86 EndY=-56.6521 EndZ=0
  constraints (19):
    c: Tangent(g0,g-3)
    c: Distance(g0,g-3) = 75
    c: Distance(g0,g0) = 6.4
    c: Coincident(g1,g0)
    c: Coincident(g2,g0)
    c: Distance(g2) = 3.8
    c: Distance(g1) = 4
    c: Perpendicular(g0,g1)
    c: Perpendicular(g0,g2)
    c: Coincident(g3,g2)
    c: Coincident(g3,g1)
    c: Equal(g4,g0)
    c: Equal(g5,g0)
    c: Parallel(g4,g0)
    c: Parallel(g5,g0)
    c: Coincident(g4,g2)
    c: Coincident(g5,g1)
    c: Coincident(g6,g4)
    c: Coincident(g6,g5)
FEATURE [Part::Extrusion] Extrude076  label="Extrude076 - scavo_rele"
  Base = -> Sketch136
  Dir = (0,-1,2e-16)
  DirMode = 2
  FaceMakerClass = Part::FaceMakerBullseye
  FaceMakerMode = 3
  LengthFwd = 10.4
  LengthRev = 0
  Solid = true
  Symmetric = true
FEATURE [Sketcher::SketchObject] Sketch137  label="scavo_nuovo_driver"
  ArcFitTolerance = 1e-06
  AttachmentSupport = -> [XZ_Plane]
  ExternalGeometry = -> [Sketch]
  FullyConstrained = true
  MakeInternals = false
  MapMode = 5
  Placement = pos=(0,0,0) rot=(1,0,0;1.5708rad)
  sketch-geometry (7):
    g0: LineSegment [constr] StartX=-171.776 StartY=-58.8398 StartZ=0 EndX=-175.794 EndY=-71.2035 EndZ=0
    g1: LineSegment [constr] StartX=-171.776 StartY=-58.8398 StartZ=0 EndX=-170.255 EndY=-59.3342 EndZ=0
    g2: LineSegment [constr] StartX=-171.776 StartY=-58.8398 StartZ=0 EndX=-175.39 EndY=-57.6655 EndZ=0
    g3: LineSegment StartX=-175.39 StartY=-57.6655 StartZ=0 EndX=-170.255 EndY=-59.3342 EndZ=0
    g4: LineSegment StartX=-175.39 StartY=-57.6655 StartZ=0 EndX=-179.408 EndY=-70.0293 EndZ=0
    g5: LineSegment StartX=-170.255 StartY=-59.3342 StartZ=0 EndX=-174.272 EndY=-71.698 EndZ=0
    g6: LineSegment StartX=-179.408 StartY=-70.0293 StartZ=0 EndX=-174.272 EndY=-71.698 EndZ=0
  constraints (19):
    c: Distance(g0,g-3) = 85
    c: Distance(g0) = 13
    c: Tangent(g0,g-3)
    c: Coincident(g1,g0)
    c: Coincident(g2,g0)
    c: Distance(g1) = 1.6
    c: Distance(g2) = 3.8
    c: Perpendicular(g0,g1)
    c: Perpendicular(g0,g2)
    c: Coincident(g3,g2)
    c: Coincident(g3,g1)
    c: Equal(g4,g0)
    c: Equal(g5,g0)
    c: Parallel(g4,g0)
    c: Parallel(g5,g0)
    c: Coincident(g4,g2)
    c: Coincident(g5,g1)
    c: Coincident(g6,g4)
    c: Coincident(g6,g5)
FEATURE [PartDesign::Body] Body  label="Struttura pistola"
  AllowCompound = false
  Group = -> [Sketch,Sketch002,Sketch004,DatumPlane,Sketch005,DatumPlane001,CopyCut,Sketch008,Sketch009,Sketch010,Sketch011,Sketch012,Sketch013,Sketch014,Sketch015,Sketch016,Sketch017,Sketch018,Sketch019,Sketch020,Sketch022,Sketch023,Sketch024,Sketch025,Sketch026,Sketch027,Sketch029,Sketch030,Sketch031,Sketch032,Sketch033,Sketch034,Sketch035,Sketch036,Sketch037,Sketch038,Sketch039,Sketch040,Sketch041,Sketch042,+17 more]
  Origin = -> Origin
FEATURE [Part::Extrusion] Extrude077  label="Extrude077 - scavo_nuovo_driver"
  Base = -> Sketch137
  Dir = (0,-1,2e-16)
  DirMode = 2
  FaceMakerClass = Part::FaceMakerBullseye
  FaceMakerMode = 3
  LengthFwd = 16.8
  LengthRev = 0
  Solid = true
  Symmetric = true
FEATURE [Part::Cut] Cut044
  Base = -> Cut043
  Refine = true
  Tool = -> Extrude076
FEATURE [Part::Cut] Cut045
  Base = -> Cut044
  Refine = true
  Tool = -> Extrude077
note: 2 file-system paths scrubbed to <path> (originals preserved in the JSON sidecar)
